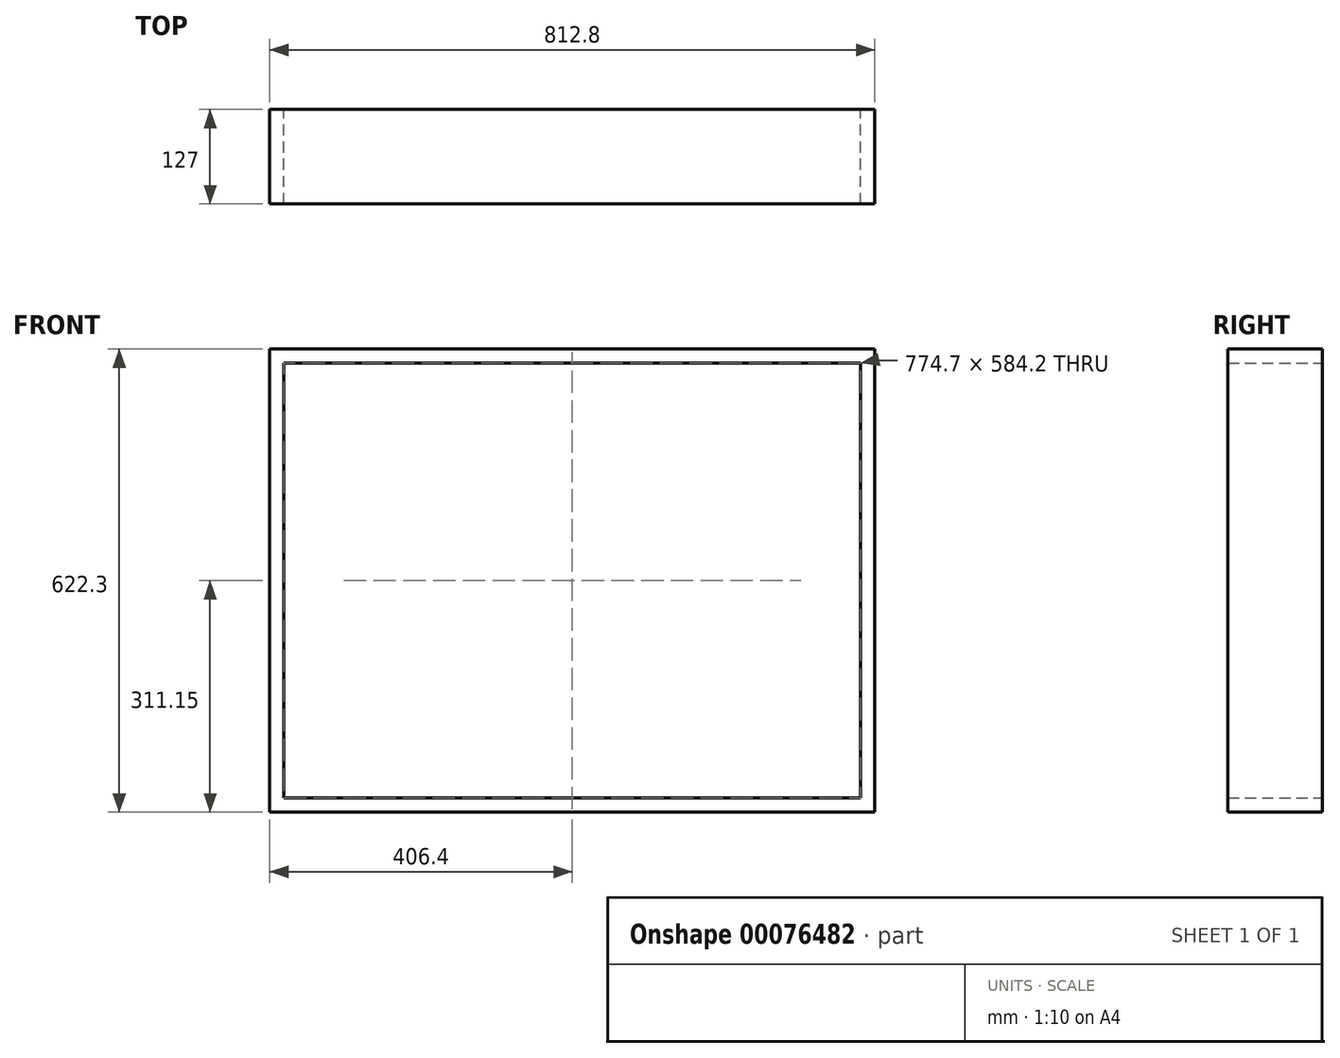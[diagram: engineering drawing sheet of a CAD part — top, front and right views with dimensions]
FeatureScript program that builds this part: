
annotation { "Feature Type Name" : "Feature", "Feature Type Description" : "" }
export const myFeature = defineFeature(function(context is Context, id is Id, definition is map)
    precondition{}
    {
        {
            var Q0;
            Q0=qCreatedBy(makeId("Front.planeOp"),FACE);
            var sketch = newSketch(context, id + "F0", { "sketchPlane" : qUnion([Q0])});
            skLineSegment(sketch, "E0.bottom", {"start": v(0, 0) * mm, "end": v(812.8, 0) * mm});
            skLineSegment(sketch, "E0.top", {"start": v(0, 622.3) * mm, "end": v(812.8, 622.3) * mm});
            skLineSegment(sketch, "E0.left", {"start": v(0, 0) * mm, "end": v(0, 622.3) * mm});
            skLineSegment(sketch, "E0.right", {"start": v(812.8, 0) * mm, "end": v(812.8, 622.3) * mm});
            skLineSegment(sketch, "E1.bottom", {"start": v(19.05, 19.05) * mm, "end": v(793.75, 19.05) * mm});
            skLineSegment(sketch, "E1.top", {"start": v(19.05, 603.25) * mm, "end": v(793.75, 603.25) * mm});
            skLineSegment(sketch, "E1.left", {"start": v(19.05, 19.05) * mm, "end": v(19.05, 603.25) * mm});
            skLineSegment(sketch, "E1.right", {"start": v(793.75, 19.05) * mm, "end": v(793.75, 603.25) * mm});
            skPoint(sketch, "E2", {"position": v(35.15, 34.19) * mm});
            skPoint(sketch, "E3.0.1.0", {"position": v(35.15, 45.97) * mm});
            skPoint(sketch, "E3.0.2.0", {"position": v(35.15, 57.76) * mm});
            skPoint(sketch, "E3.1.0.0", {"position": v(46.94, 34.19) * mm});
            skPoint(sketch, "E3.1.1.0", {"position": v(46.94, 45.97) * mm});
            skPoint(sketch, "E3.1.2.0", {"position": v(46.94, 57.76) * mm});
            skPoint(sketch, "E3.2.0.0", {"position": v(58.72, 34.19) * mm});
            skPoint(sketch, "E3.2.1.0", {"position": v(58.72, 45.97) * mm});
            skPoint(sketch, "E3.2.2.0", {"position": v(58.72, 57.76) * mm});
            skLineSegment(sketch, "E3.direction1", {"start": v(35.15, 34.19) * mm, "end": v(46.94, 34.19) * mm, "construction": true});
            skLineSegment(sketch, "E3.direction2", {"start": v(35.15, 34.19) * mm, "end": v(35.15, 45.97) * mm, "construction": true});
            skPoint(sketch, "E4.0.0.3", {"position": v(35.15, 69.54) * mm});
            skPoint(sketch, "E4.0.0.4", {"position": v(35.15, 81.33) * mm});
            skPoint(sketch, "E4.0.0.5", {"position": v(35.15, 93.11) * mm});
            skPoint(sketch, "E4.0.0.6", {"position": v(35.15, 104.9) * mm});
            skPoint(sketch, "E4.0.0.7", {"position": v(35.15, 116.68) * mm});
            skPoint(sketch, "E4.0.0.8", {"position": v(35.15, 128.47) * mm});
            skPoint(sketch, "E4.0.0.9", {"position": v(35.15, 140.25) * mm});
            skPoint(sketch, "E4.0.0.10", {"position": v(35.15, 152.04) * mm});
            skPoint(sketch, "E4.0.0.11", {"position": v(35.15, 163.82) * mm});
            skPoint(sketch, "E4.0.0.12", {"position": v(35.15, 175.6) * mm});
            skPoint(sketch, "E4.0.0.13", {"position": v(35.15, 187.4) * mm});
            skPoint(sketch, "E4.0.0.14", {"position": v(35.15, 199.18) * mm});
            skPoint(sketch, "E4.0.0.15", {"position": v(35.15, 210.97) * mm});
            skPoint(sketch, "E4.0.0.16", {"position": v(35.15, 222.75) * mm});
            skPoint(sketch, "E4.0.0.17", {"position": v(35.15, 234.54) * mm});
            skPoint(sketch, "E4.0.0.18", {"position": v(35.15, 246.32) * mm});
            skPoint(sketch, "E4.0.0.19", {"position": v(35.15, 258.1) * mm});
            skPoint(sketch, "E4.0.0.20", {"position": v(35.15, 269.9) * mm});
            skPoint(sketch, "E4.0.0.21", {"position": v(35.15, 281.68) * mm});
            skPoint(sketch, "E4.0.0.22", {"position": v(35.15, 293.46) * mm});
            skPoint(sketch, "E4.0.0.23", {"position": v(35.15, 305.25) * mm});
            skPoint(sketch, "E4.0.0.24", {"position": v(35.15, 317.03) * mm});
            skPoint(sketch, "E4.0.0.25", {"position": v(35.15, 328.82) * mm});
            skPoint(sketch, "E4.0.0.26", {"position": v(35.15, 340.6) * mm});
            skPoint(sketch, "E4.0.0.27", {"position": v(35.15, 352.39) * mm});
            skPoint(sketch, "E4.0.0.28", {"position": v(35.15, 364.17) * mm});
            skPoint(sketch, "E4.0.0.29", {"position": v(35.15, 375.96) * mm});
            skPoint(sketch, "E4.0.0.30", {"position": v(35.15, 387.74) * mm});
            skPoint(sketch, "E4.0.0.31", {"position": v(35.15, 399.53) * mm});
            skPoint(sketch, "E4.0.0.32", {"position": v(35.15, 411.31) * mm});
            skPoint(sketch, "E4.0.0.33", {"position": v(35.15, 423.1) * mm});
            skPoint(sketch, "E4.0.0.34", {"position": v(35.15, 434.88) * mm});
            skPoint(sketch, "E4.0.0.35", {"position": v(35.15, 446.67) * mm});
            skPoint(sketch, "E4.0.0.36", {"position": v(35.15, 458.45) * mm});
            skPoint(sketch, "E4.0.0.37", {"position": v(35.15, 470.24) * mm});
            skPoint(sketch, "E4.0.0.38", {"position": v(35.15, 482.02) * mm});
            skPoint(sketch, "E4.0.0.39", {"position": v(35.15, 493.8) * mm});
            skPoint(sketch, "E4.0.0.40", {"position": v(35.15, 505.6) * mm});
            skPoint(sketch, "E4.0.0.41", {"position": v(35.15, 517.38) * mm});
            skPoint(sketch, "E4.0.0.42", {"position": v(35.15, 529.16) * mm});
            skPoint(sketch, "E4.0.0.43", {"position": v(35.15, 540.95) * mm});
            skPoint(sketch, "E4.0.0.44", {"position": v(35.15, 552.73) * mm});
            skPoint(sketch, "E4.0.0.45", {"position": v(35.15, 564.52) * mm});
            skPoint(sketch, "E4.0.0.46", {"position": v(35.15, 576.3) * mm});
            skPoint(sketch, "E4.0.0.47", {"position": v(35.15, 588.09) * mm});
            skPoint(sketch, "E4.0.1.3", {"position": v(46.94, 69.54) * mm});
            skPoint(sketch, "E4.0.1.4", {"position": v(46.94, 81.33) * mm});
            skPoint(sketch, "E4.0.1.5", {"position": v(46.94, 93.11) * mm});
            skPoint(sketch, "E4.0.1.6", {"position": v(46.94, 104.9) * mm});
            skPoint(sketch, "E4.0.1.7", {"position": v(46.94, 116.68) * mm});
            skPoint(sketch, "E4.0.1.8", {"position": v(46.94, 128.47) * mm});
            skPoint(sketch, "E4.0.1.9", {"position": v(46.94, 140.25) * mm});
            skPoint(sketch, "E4.0.1.10", {"position": v(46.94, 152.04) * mm});
            skPoint(sketch, "E4.0.1.11", {"position": v(46.94, 163.82) * mm});
            skPoint(sketch, "E4.0.1.12", {"position": v(46.94, 175.6) * mm});
            skPoint(sketch, "E4.0.1.13", {"position": v(46.94, 187.4) * mm});
            skPoint(sketch, "E4.0.1.14", {"position": v(46.94, 199.18) * mm});
            skPoint(sketch, "E4.0.1.15", {"position": v(46.94, 210.97) * mm});
            skPoint(sketch, "E4.0.1.16", {"position": v(46.94, 222.75) * mm});
            skPoint(sketch, "E4.0.1.17", {"position": v(46.94, 234.54) * mm});
            skPoint(sketch, "E4.0.1.18", {"position": v(46.94, 246.32) * mm});
            skPoint(sketch, "E4.0.1.19", {"position": v(46.94, 258.1) * mm});
            skPoint(sketch, "E4.0.1.20", {"position": v(46.94, 269.9) * mm});
            skPoint(sketch, "E4.0.1.21", {"position": v(46.94, 281.68) * mm});
            skPoint(sketch, "E4.0.1.22", {"position": v(46.94, 293.46) * mm});
            skPoint(sketch, "E4.0.1.23", {"position": v(46.94, 305.25) * mm});
            skPoint(sketch, "E4.0.1.24", {"position": v(46.94, 317.03) * mm});
            skPoint(sketch, "E4.0.1.25", {"position": v(46.94, 328.82) * mm});
            skPoint(sketch, "E4.0.1.26", {"position": v(46.94, 340.6) * mm});
            skPoint(sketch, "E4.0.1.27", {"position": v(46.94, 352.39) * mm});
            skPoint(sketch, "E4.0.1.28", {"position": v(46.94, 364.17) * mm});
            skPoint(sketch, "E4.0.1.29", {"position": v(46.94, 375.96) * mm});
            skPoint(sketch, "E4.0.1.30", {"position": v(46.94, 387.74) * mm});
            skPoint(sketch, "E4.0.1.31", {"position": v(46.94, 399.53) * mm});
            skPoint(sketch, "E4.0.1.32", {"position": v(46.94, 411.31) * mm});
            skPoint(sketch, "E4.0.1.33", {"position": v(46.94, 423.1) * mm});
            skPoint(sketch, "E4.0.1.34", {"position": v(46.94, 434.88) * mm});
            skPoint(sketch, "E4.0.1.35", {"position": v(46.94, 446.67) * mm});
            skPoint(sketch, "E4.0.1.36", {"position": v(46.94, 458.45) * mm});
            skPoint(sketch, "E4.0.1.37", {"position": v(46.94, 470.24) * mm});
            skPoint(sketch, "E4.0.1.38", {"position": v(46.94, 482.02) * mm});
            skPoint(sketch, "E4.0.1.39", {"position": v(46.94, 493.8) * mm});
            skPoint(sketch, "E4.0.1.40", {"position": v(46.94, 505.6) * mm});
            skPoint(sketch, "E4.0.1.41", {"position": v(46.94, 517.38) * mm});
            skPoint(sketch, "E4.0.1.42", {"position": v(46.94, 529.16) * mm});
            skPoint(sketch, "E4.0.1.43", {"position": v(46.94, 540.95) * mm});
            skPoint(sketch, "E4.0.1.44", {"position": v(46.94, 552.73) * mm});
            skPoint(sketch, "E4.0.1.45", {"position": v(46.94, 564.52) * mm});
            skPoint(sketch, "E4.0.1.46", {"position": v(46.94, 576.3) * mm});
            skPoint(sketch, "E4.0.1.47", {"position": v(46.94, 588.09) * mm});
            skPoint(sketch, "E4.0.2.3", {"position": v(58.72, 69.54) * mm});
            skPoint(sketch, "E4.0.2.4", {"position": v(58.72, 81.33) * mm});
            skPoint(sketch, "E4.0.2.5", {"position": v(58.72, 93.11) * mm});
            skPoint(sketch, "E4.0.2.6", {"position": v(58.72, 104.9) * mm});
            skPoint(sketch, "E4.0.2.7", {"position": v(58.72, 116.68) * mm});
            skPoint(sketch, "E4.0.2.8", {"position": v(58.72, 128.47) * mm});
            skPoint(sketch, "E4.0.2.9", {"position": v(58.72, 140.25) * mm});
            skPoint(sketch, "E4.0.2.10", {"position": v(58.72, 152.04) * mm});
            skPoint(sketch, "E4.0.2.11", {"position": v(58.72, 163.82) * mm});
            skPoint(sketch, "E4.0.2.12", {"position": v(58.72, 175.6) * mm});
            skPoint(sketch, "E4.0.2.13", {"position": v(58.72, 187.4) * mm});
            skPoint(sketch, "E4.0.2.14", {"position": v(58.72, 199.18) * mm});
            skPoint(sketch, "E4.0.2.15", {"position": v(58.72, 210.97) * mm});
            skPoint(sketch, "E4.0.2.16", {"position": v(58.72, 222.75) * mm});
            skPoint(sketch, "E4.0.2.17", {"position": v(58.72, 234.54) * mm});
            skPoint(sketch, "E4.0.2.18", {"position": v(58.72, 246.32) * mm});
            skPoint(sketch, "E4.0.2.19", {"position": v(58.72, 258.1) * mm});
            skPoint(sketch, "E4.0.2.20", {"position": v(58.72, 269.9) * mm});
            skPoint(sketch, "E4.0.2.21", {"position": v(58.72, 281.68) * mm});
            skPoint(sketch, "E4.0.2.22", {"position": v(58.72, 293.46) * mm});
            skPoint(sketch, "E4.0.2.23", {"position": v(58.72, 305.25) * mm});
            skPoint(sketch, "E4.0.2.24", {"position": v(58.72, 317.03) * mm});
            skPoint(sketch, "E4.0.2.25", {"position": v(58.72, 328.82) * mm});
            skPoint(sketch, "E4.0.2.26", {"position": v(58.72, 340.6) * mm});
            skPoint(sketch, "E4.0.2.27", {"position": v(58.72, 352.39) * mm});
            skPoint(sketch, "E4.0.2.28", {"position": v(58.72, 364.17) * mm});
            skPoint(sketch, "E4.0.2.29", {"position": v(58.72, 375.96) * mm});
            skPoint(sketch, "E4.0.2.30", {"position": v(58.72, 387.74) * mm});
            skPoint(sketch, "E4.0.2.31", {"position": v(58.72, 399.53) * mm});
            skPoint(sketch, "E4.0.2.32", {"position": v(58.72, 411.31) * mm});
            skPoint(sketch, "E4.0.2.33", {"position": v(58.72, 423.1) * mm});
            skPoint(sketch, "E4.0.2.34", {"position": v(58.72, 434.88) * mm});
            skPoint(sketch, "E4.0.2.35", {"position": v(58.72, 446.67) * mm});
            skPoint(sketch, "E4.0.2.36", {"position": v(58.72, 458.45) * mm});
            skPoint(sketch, "E4.0.2.37", {"position": v(58.72, 470.24) * mm});
            skPoint(sketch, "E4.0.2.38", {"position": v(58.72, 482.02) * mm});
            skPoint(sketch, "E4.0.2.39", {"position": v(58.72, 493.8) * mm});
            skPoint(sketch, "E4.0.2.40", {"position": v(58.72, 505.6) * mm});
            skPoint(sketch, "E4.0.2.41", {"position": v(58.72, 517.38) * mm});
            skPoint(sketch, "E4.0.2.42", {"position": v(58.72, 529.16) * mm});
            skPoint(sketch, "E4.0.2.43", {"position": v(58.72, 540.95) * mm});
            skPoint(sketch, "E4.0.2.44", {"position": v(58.72, 552.73) * mm});
            skPoint(sketch, "E4.0.2.45", {"position": v(58.72, 564.52) * mm});
            skPoint(sketch, "E4.0.2.46", {"position": v(58.72, 576.3) * mm});
            skPoint(sketch, "E4.0.2.47", {"position": v(58.72, 588.09) * mm});
            skPoint(sketch, "E5.0.3.0", {"position": v(70.5, 34.19) * mm});
            skPoint(sketch, "E5.0.3.1", {"position": v(70.5, 45.97) * mm});
            skPoint(sketch, "E5.0.3.2", {"position": v(70.5, 57.76) * mm});
            skPoint(sketch, "E5.0.3.3", {"position": v(70.5, 69.54) * mm});
            skPoint(sketch, "E5.0.3.4", {"position": v(70.5, 81.33) * mm});
            skPoint(sketch, "E5.0.3.5", {"position": v(70.5, 93.11) * mm});
            skPoint(sketch, "E5.0.3.6", {"position": v(70.5, 104.9) * mm});
            skPoint(sketch, "E5.0.3.7", {"position": v(70.5, 116.68) * mm});
            skPoint(sketch, "E5.0.3.8", {"position": v(70.5, 128.47) * mm});
            skPoint(sketch, "E5.0.3.9", {"position": v(70.5, 140.25) * mm});
            skPoint(sketch, "E5.0.3.10", {"position": v(70.5, 152.04) * mm});
            skPoint(sketch, "E5.0.3.11", {"position": v(70.5, 163.82) * mm});
            skPoint(sketch, "E5.0.3.12", {"position": v(70.5, 175.6) * mm});
            skPoint(sketch, "E5.0.3.13", {"position": v(70.5, 187.4) * mm});
            skPoint(sketch, "E5.0.3.14", {"position": v(70.5, 199.18) * mm});
            skPoint(sketch, "E5.0.3.15", {"position": v(70.5, 210.97) * mm});
            skPoint(sketch, "E5.0.3.16", {"position": v(70.5, 222.75) * mm});
            skPoint(sketch, "E5.0.3.17", {"position": v(70.5, 234.54) * mm});
            skPoint(sketch, "E5.0.3.18", {"position": v(70.5, 246.32) * mm});
            skPoint(sketch, "E5.0.3.19", {"position": v(70.5, 258.1) * mm});
            skPoint(sketch, "E5.0.3.20", {"position": v(70.5, 269.9) * mm});
            skPoint(sketch, "E5.0.3.21", {"position": v(70.5, 281.68) * mm});
            skPoint(sketch, "E5.0.3.22", {"position": v(70.5, 293.46) * mm});
            skPoint(sketch, "E5.0.3.23", {"position": v(70.5, 305.25) * mm});
            skPoint(sketch, "E5.0.3.24", {"position": v(70.5, 317.03) * mm});
            skPoint(sketch, "E5.0.3.25", {"position": v(70.5, 328.82) * mm});
            skPoint(sketch, "E5.0.3.26", {"position": v(70.5, 340.6) * mm});
            skPoint(sketch, "E5.0.3.27", {"position": v(70.5, 352.39) * mm});
            skPoint(sketch, "E5.0.3.28", {"position": v(70.5, 364.17) * mm});
            skPoint(sketch, "E5.0.3.29", {"position": v(70.5, 375.96) * mm});
            skPoint(sketch, "E5.0.3.30", {"position": v(70.5, 387.74) * mm});
            skPoint(sketch, "E5.0.3.31", {"position": v(70.5, 399.53) * mm});
            skPoint(sketch, "E5.0.3.32", {"position": v(70.5, 411.31) * mm});
            skPoint(sketch, "E5.0.3.33", {"position": v(70.5, 423.1) * mm});
            skPoint(sketch, "E5.0.3.34", {"position": v(70.5, 434.88) * mm});
            skPoint(sketch, "E5.0.3.35", {"position": v(70.5, 446.67) * mm});
            skPoint(sketch, "E5.0.3.36", {"position": v(70.5, 458.45) * mm});
            skPoint(sketch, "E5.0.3.37", {"position": v(70.5, 470.24) * mm});
            skPoint(sketch, "E5.0.3.38", {"position": v(70.5, 482.02) * mm});
            skPoint(sketch, "E5.0.3.39", {"position": v(70.5, 493.8) * mm});
            skPoint(sketch, "E5.0.3.40", {"position": v(70.5, 505.6) * mm});
            skPoint(sketch, "E5.0.3.41", {"position": v(70.5, 517.38) * mm});
            skPoint(sketch, "E5.0.3.42", {"position": v(70.5, 529.16) * mm});
            skPoint(sketch, "E5.0.3.43", {"position": v(70.5, 540.95) * mm});
            skPoint(sketch, "E5.0.3.44", {"position": v(70.5, 552.73) * mm});
            skPoint(sketch, "E5.0.3.45", {"position": v(70.5, 564.52) * mm});
            skPoint(sketch, "E5.0.3.46", {"position": v(70.5, 576.3) * mm});
            skPoint(sketch, "E5.0.3.47", {"position": v(70.5, 588.09) * mm});
            skPoint(sketch, "E5.0.4.0", {"position": v(82.3, 34.19) * mm});
            skPoint(sketch, "E5.0.4.1", {"position": v(82.3, 45.97) * mm});
            skPoint(sketch, "E5.0.4.2", {"position": v(82.3, 57.76) * mm});
            skPoint(sketch, "E5.0.4.3", {"position": v(82.3, 69.54) * mm});
            skPoint(sketch, "E5.0.4.4", {"position": v(82.3, 81.33) * mm});
            skPoint(sketch, "E5.0.4.5", {"position": v(82.3, 93.11) * mm});
            skPoint(sketch, "E5.0.4.6", {"position": v(82.3, 104.9) * mm});
            skPoint(sketch, "E5.0.4.7", {"position": v(82.3, 116.68) * mm});
            skPoint(sketch, "E5.0.4.8", {"position": v(82.3, 128.47) * mm});
            skPoint(sketch, "E5.0.4.9", {"position": v(82.3, 140.25) * mm});
            skPoint(sketch, "E5.0.4.10", {"position": v(82.3, 152.04) * mm});
            skPoint(sketch, "E5.0.4.11", {"position": v(82.3, 163.82) * mm});
            skPoint(sketch, "E5.0.4.12", {"position": v(82.3, 175.6) * mm});
            skPoint(sketch, "E5.0.4.13", {"position": v(82.3, 187.4) * mm});
            skPoint(sketch, "E5.0.4.14", {"position": v(82.3, 199.18) * mm});
            skPoint(sketch, "E5.0.4.15", {"position": v(82.3, 210.97) * mm});
            skPoint(sketch, "E5.0.4.16", {"position": v(82.3, 222.75) * mm});
            skPoint(sketch, "E5.0.4.17", {"position": v(82.3, 234.54) * mm});
            skPoint(sketch, "E5.0.4.18", {"position": v(82.3, 246.32) * mm});
            skPoint(sketch, "E5.0.4.19", {"position": v(82.3, 258.1) * mm});
            skPoint(sketch, "E5.0.4.20", {"position": v(82.3, 269.9) * mm});
            skPoint(sketch, "E5.0.4.21", {"position": v(82.3, 281.68) * mm});
            skPoint(sketch, "E5.0.4.22", {"position": v(82.3, 293.46) * mm});
            skPoint(sketch, "E5.0.4.23", {"position": v(82.3, 305.25) * mm});
            skPoint(sketch, "E5.0.4.24", {"position": v(82.3, 317.03) * mm});
            skPoint(sketch, "E5.0.4.25", {"position": v(82.3, 328.82) * mm});
            skPoint(sketch, "E5.0.4.26", {"position": v(82.3, 340.6) * mm});
            skPoint(sketch, "E5.0.4.27", {"position": v(82.3, 352.39) * mm});
            skPoint(sketch, "E5.0.4.28", {"position": v(82.3, 364.17) * mm});
            skPoint(sketch, "E5.0.4.29", {"position": v(82.3, 375.96) * mm});
            skPoint(sketch, "E5.0.4.30", {"position": v(82.3, 387.74) * mm});
            skPoint(sketch, "E5.0.4.31", {"position": v(82.3, 399.53) * mm});
            skPoint(sketch, "E5.0.4.32", {"position": v(82.3, 411.31) * mm});
            skPoint(sketch, "E5.0.4.33", {"position": v(82.3, 423.1) * mm});
            skPoint(sketch, "E5.0.4.34", {"position": v(82.3, 434.88) * mm});
            skPoint(sketch, "E5.0.4.35", {"position": v(82.3, 446.67) * mm});
            skPoint(sketch, "E5.0.4.36", {"position": v(82.3, 458.45) * mm});
            skPoint(sketch, "E5.0.4.37", {"position": v(82.3, 470.24) * mm});
            skPoint(sketch, "E5.0.4.38", {"position": v(82.3, 482.02) * mm});
            skPoint(sketch, "E5.0.4.39", {"position": v(82.3, 493.8) * mm});
            skPoint(sketch, "E5.0.4.40", {"position": v(82.3, 505.6) * mm});
            skPoint(sketch, "E5.0.4.41", {"position": v(82.3, 517.38) * mm});
            skPoint(sketch, "E5.0.4.42", {"position": v(82.3, 529.16) * mm});
            skPoint(sketch, "E5.0.4.43", {"position": v(82.3, 540.95) * mm});
            skPoint(sketch, "E5.0.4.44", {"position": v(82.3, 552.73) * mm});
            skPoint(sketch, "E5.0.4.45", {"position": v(82.3, 564.52) * mm});
            skPoint(sketch, "E5.0.4.46", {"position": v(82.3, 576.3) * mm});
            skPoint(sketch, "E5.0.4.47", {"position": v(82.3, 588.09) * mm});
            skPoint(sketch, "E5.0.5.0", {"position": v(94.08, 34.19) * mm});
            skPoint(sketch, "E5.0.5.1", {"position": v(94.08, 45.97) * mm});
            skPoint(sketch, "E5.0.5.2", {"position": v(94.08, 57.76) * mm});
            skPoint(sketch, "E5.0.5.3", {"position": v(94.08, 69.54) * mm});
            skPoint(sketch, "E5.0.5.4", {"position": v(94.08, 81.33) * mm});
            skPoint(sketch, "E5.0.5.5", {"position": v(94.08, 93.11) * mm});
            skPoint(sketch, "E5.0.5.6", {"position": v(94.08, 104.9) * mm});
            skPoint(sketch, "E5.0.5.7", {"position": v(94.08, 116.68) * mm});
            skPoint(sketch, "E5.0.5.8", {"position": v(94.08, 128.47) * mm});
            skPoint(sketch, "E5.0.5.9", {"position": v(94.08, 140.25) * mm});
            skPoint(sketch, "E5.0.5.10", {"position": v(94.08, 152.04) * mm});
            skPoint(sketch, "E5.0.5.11", {"position": v(94.08, 163.82) * mm});
            skPoint(sketch, "E5.0.5.12", {"position": v(94.08, 175.6) * mm});
            skPoint(sketch, "E5.0.5.13", {"position": v(94.08, 187.4) * mm});
            skPoint(sketch, "E5.0.5.14", {"position": v(94.08, 199.18) * mm});
            skPoint(sketch, "E5.0.5.15", {"position": v(94.08, 210.97) * mm});
            skPoint(sketch, "E5.0.5.16", {"position": v(94.08, 222.75) * mm});
            skPoint(sketch, "E5.0.5.17", {"position": v(94.08, 234.54) * mm});
            skPoint(sketch, "E5.0.5.18", {"position": v(94.08, 246.32) * mm});
            skPoint(sketch, "E5.0.5.19", {"position": v(94.08, 258.1) * mm});
            skPoint(sketch, "E5.0.5.20", {"position": v(94.08, 269.9) * mm});
            skPoint(sketch, "E5.0.5.21", {"position": v(94.08, 281.68) * mm});
            skPoint(sketch, "E5.0.5.22", {"position": v(94.08, 293.46) * mm});
            skPoint(sketch, "E5.0.5.23", {"position": v(94.08, 305.25) * mm});
            skPoint(sketch, "E5.0.5.24", {"position": v(94.08, 317.03) * mm});
            skPoint(sketch, "E5.0.5.25", {"position": v(94.08, 328.82) * mm});
            skPoint(sketch, "E5.0.5.26", {"position": v(94.08, 340.6) * mm});
            skPoint(sketch, "E5.0.5.27", {"position": v(94.08, 352.39) * mm});
            skPoint(sketch, "E5.0.5.28", {"position": v(94.08, 364.17) * mm});
            skPoint(sketch, "E5.0.5.29", {"position": v(94.08, 375.96) * mm});
            skPoint(sketch, "E5.0.5.30", {"position": v(94.08, 387.74) * mm});
            skPoint(sketch, "E5.0.5.31", {"position": v(94.08, 399.53) * mm});
            skPoint(sketch, "E5.0.5.32", {"position": v(94.08, 411.31) * mm});
            skPoint(sketch, "E5.0.5.33", {"position": v(94.08, 423.1) * mm});
            skPoint(sketch, "E5.0.5.34", {"position": v(94.08, 434.88) * mm});
            skPoint(sketch, "E5.0.5.35", {"position": v(94.08, 446.67) * mm});
            skPoint(sketch, "E5.0.5.36", {"position": v(94.08, 458.45) * mm});
            skPoint(sketch, "E5.0.5.37", {"position": v(94.08, 470.24) * mm});
            skPoint(sketch, "E5.0.5.38", {"position": v(94.08, 482.02) * mm});
            skPoint(sketch, "E5.0.5.39", {"position": v(94.08, 493.8) * mm});
            skPoint(sketch, "E5.0.5.40", {"position": v(94.08, 505.6) * mm});
            skPoint(sketch, "E5.0.5.41", {"position": v(94.08, 517.38) * mm});
            skPoint(sketch, "E5.0.5.42", {"position": v(94.08, 529.16) * mm});
            skPoint(sketch, "E5.0.5.43", {"position": v(94.08, 540.95) * mm});
            skPoint(sketch, "E5.0.5.44", {"position": v(94.08, 552.73) * mm});
            skPoint(sketch, "E5.0.5.45", {"position": v(94.08, 564.52) * mm});
            skPoint(sketch, "E5.0.5.46", {"position": v(94.08, 576.3) * mm});
            skPoint(sketch, "E5.0.5.47", {"position": v(94.08, 588.09) * mm});
            skPoint(sketch, "E5.0.6.0", {"position": v(105.86, 34.19) * mm});
            skPoint(sketch, "E5.0.6.1", {"position": v(105.86, 45.97) * mm});
            skPoint(sketch, "E5.0.6.2", {"position": v(105.86, 57.76) * mm});
            skPoint(sketch, "E5.0.6.3", {"position": v(105.86, 69.54) * mm});
            skPoint(sketch, "E5.0.6.4", {"position": v(105.86, 81.33) * mm});
            skPoint(sketch, "E5.0.6.5", {"position": v(105.86, 93.11) * mm});
            skPoint(sketch, "E5.0.6.6", {"position": v(105.86, 104.9) * mm});
            skPoint(sketch, "E5.0.6.7", {"position": v(105.86, 116.68) * mm});
            skPoint(sketch, "E5.0.6.8", {"position": v(105.86, 128.47) * mm});
            skPoint(sketch, "E5.0.6.9", {"position": v(105.86, 140.25) * mm});
            skPoint(sketch, "E5.0.6.10", {"position": v(105.86, 152.04) * mm});
            skPoint(sketch, "E5.0.6.11", {"position": v(105.86, 163.82) * mm});
            skPoint(sketch, "E5.0.6.12", {"position": v(105.86, 175.6) * mm});
            skPoint(sketch, "E5.0.6.13", {"position": v(105.86, 187.4) * mm});
            skPoint(sketch, "E5.0.6.14", {"position": v(105.86, 199.18) * mm});
            skPoint(sketch, "E5.0.6.15", {"position": v(105.86, 210.97) * mm});
            skPoint(sketch, "E5.0.6.16", {"position": v(105.86, 222.75) * mm});
            skPoint(sketch, "E5.0.6.17", {"position": v(105.86, 234.54) * mm});
            skPoint(sketch, "E5.0.6.18", {"position": v(105.86, 246.32) * mm});
            skPoint(sketch, "E5.0.6.19", {"position": v(105.86, 258.1) * mm});
            skPoint(sketch, "E5.0.6.20", {"position": v(105.86, 269.9) * mm});
            skPoint(sketch, "E5.0.6.21", {"position": v(105.86, 281.68) * mm});
            skPoint(sketch, "E5.0.6.22", {"position": v(105.86, 293.46) * mm});
            skPoint(sketch, "E5.0.6.23", {"position": v(105.86, 305.25) * mm});
            skPoint(sketch, "E5.0.6.24", {"position": v(105.86, 317.03) * mm});
            skPoint(sketch, "E5.0.6.25", {"position": v(105.86, 328.82) * mm});
            skPoint(sketch, "E5.0.6.26", {"position": v(105.86, 340.6) * mm});
            skPoint(sketch, "E5.0.6.27", {"position": v(105.86, 352.39) * mm});
            skPoint(sketch, "E5.0.6.28", {"position": v(105.86, 364.17) * mm});
            skPoint(sketch, "E5.0.6.29", {"position": v(105.86, 375.96) * mm});
            skPoint(sketch, "E5.0.6.30", {"position": v(105.86, 387.74) * mm});
            skPoint(sketch, "E5.0.6.31", {"position": v(105.86, 399.53) * mm});
            skPoint(sketch, "E5.0.6.32", {"position": v(105.86, 411.31) * mm});
            skPoint(sketch, "E5.0.6.33", {"position": v(105.86, 423.1) * mm});
            skPoint(sketch, "E5.0.6.34", {"position": v(105.86, 434.88) * mm});
            skPoint(sketch, "E5.0.6.35", {"position": v(105.86, 446.67) * mm});
            skPoint(sketch, "E5.0.6.36", {"position": v(105.86, 458.45) * mm});
            skPoint(sketch, "E5.0.6.37", {"position": v(105.86, 470.24) * mm});
            skPoint(sketch, "E5.0.6.38", {"position": v(105.86, 482.02) * mm});
            skPoint(sketch, "E5.0.6.39", {"position": v(105.86, 493.8) * mm});
            skPoint(sketch, "E5.0.6.40", {"position": v(105.86, 505.6) * mm});
            skPoint(sketch, "E5.0.6.41", {"position": v(105.86, 517.38) * mm});
            skPoint(sketch, "E5.0.6.42", {"position": v(105.86, 529.16) * mm});
            skPoint(sketch, "E5.0.6.43", {"position": v(105.86, 540.95) * mm});
            skPoint(sketch, "E5.0.6.44", {"position": v(105.86, 552.73) * mm});
            skPoint(sketch, "E5.0.6.45", {"position": v(105.86, 564.52) * mm});
            skPoint(sketch, "E5.0.6.46", {"position": v(105.86, 576.3) * mm});
            skPoint(sketch, "E5.0.6.47", {"position": v(105.86, 588.09) * mm});
            skPoint(sketch, "E5.0.7.0", {"position": v(117.65, 34.19) * mm});
            skPoint(sketch, "E5.0.7.1", {"position": v(117.65, 45.97) * mm});
            skPoint(sketch, "E5.0.7.2", {"position": v(117.65, 57.76) * mm});
            skPoint(sketch, "E5.0.7.3", {"position": v(117.65, 69.54) * mm});
            skPoint(sketch, "E5.0.7.4", {"position": v(117.65, 81.33) * mm});
            skPoint(sketch, "E5.0.7.5", {"position": v(117.65, 93.11) * mm});
            skPoint(sketch, "E5.0.7.6", {"position": v(117.65, 104.9) * mm});
            skPoint(sketch, "E5.0.7.7", {"position": v(117.65, 116.68) * mm});
            skPoint(sketch, "E5.0.7.8", {"position": v(117.65, 128.47) * mm});
            skPoint(sketch, "E5.0.7.9", {"position": v(117.65, 140.25) * mm});
            skPoint(sketch, "E5.0.7.10", {"position": v(117.65, 152.04) * mm});
            skPoint(sketch, "E5.0.7.11", {"position": v(117.65, 163.82) * mm});
            skPoint(sketch, "E5.0.7.12", {"position": v(117.65, 175.6) * mm});
            skPoint(sketch, "E5.0.7.13", {"position": v(117.65, 187.4) * mm});
            skPoint(sketch, "E5.0.7.14", {"position": v(117.65, 199.18) * mm});
            skPoint(sketch, "E5.0.7.15", {"position": v(117.65, 210.97) * mm});
            skPoint(sketch, "E5.0.7.16", {"position": v(117.65, 222.75) * mm});
            skPoint(sketch, "E5.0.7.17", {"position": v(117.65, 234.54) * mm});
            skPoint(sketch, "E5.0.7.18", {"position": v(117.65, 246.32) * mm});
            skPoint(sketch, "E5.0.7.19", {"position": v(117.65, 258.1) * mm});
            skPoint(sketch, "E5.0.7.20", {"position": v(117.65, 269.9) * mm});
            skPoint(sketch, "E5.0.7.21", {"position": v(117.65, 281.68) * mm});
            skPoint(sketch, "E5.0.7.22", {"position": v(117.65, 293.46) * mm});
            skPoint(sketch, "E5.0.7.23", {"position": v(117.65, 305.25) * mm});
            skPoint(sketch, "E5.0.7.24", {"position": v(117.65, 317.03) * mm});
            skPoint(sketch, "E5.0.7.25", {"position": v(117.65, 328.82) * mm});
            skPoint(sketch, "E5.0.7.26", {"position": v(117.65, 340.6) * mm});
            skPoint(sketch, "E5.0.7.27", {"position": v(117.65, 352.39) * mm});
            skPoint(sketch, "E5.0.7.28", {"position": v(117.65, 364.17) * mm});
            skPoint(sketch, "E5.0.7.29", {"position": v(117.65, 375.96) * mm});
            skPoint(sketch, "E5.0.7.30", {"position": v(117.65, 387.74) * mm});
            skPoint(sketch, "E5.0.7.31", {"position": v(117.65, 399.53) * mm});
            skPoint(sketch, "E5.0.7.32", {"position": v(117.65, 411.31) * mm});
            skPoint(sketch, "E5.0.7.33", {"position": v(117.65, 423.1) * mm});
            skPoint(sketch, "E5.0.7.34", {"position": v(117.65, 434.88) * mm});
            skPoint(sketch, "E5.0.7.35", {"position": v(117.65, 446.67) * mm});
            skPoint(sketch, "E5.0.7.36", {"position": v(117.65, 458.45) * mm});
            skPoint(sketch, "E5.0.7.37", {"position": v(117.65, 470.24) * mm});
            skPoint(sketch, "E5.0.7.38", {"position": v(117.65, 482.02) * mm});
            skPoint(sketch, "E5.0.7.39", {"position": v(117.65, 493.8) * mm});
            skPoint(sketch, "E5.0.7.40", {"position": v(117.65, 505.6) * mm});
            skPoint(sketch, "E5.0.7.41", {"position": v(117.65, 517.38) * mm});
            skPoint(sketch, "E5.0.7.42", {"position": v(117.65, 529.16) * mm});
            skPoint(sketch, "E5.0.7.43", {"position": v(117.65, 540.95) * mm});
            skPoint(sketch, "E5.0.7.44", {"position": v(117.65, 552.73) * mm});
            skPoint(sketch, "E5.0.7.45", {"position": v(117.65, 564.52) * mm});
            skPoint(sketch, "E5.0.7.46", {"position": v(117.65, 576.3) * mm});
            skPoint(sketch, "E5.0.7.47", {"position": v(117.65, 588.09) * mm});
            skPoint(sketch, "E5.0.8.0", {"position": v(129.43, 34.19) * mm});
            skPoint(sketch, "E5.0.8.1", {"position": v(129.43, 45.97) * mm});
            skPoint(sketch, "E5.0.8.2", {"position": v(129.43, 57.76) * mm});
            skPoint(sketch, "E5.0.8.3", {"position": v(129.43, 69.54) * mm});
            skPoint(sketch, "E5.0.8.4", {"position": v(129.43, 81.33) * mm});
            skPoint(sketch, "E5.0.8.5", {"position": v(129.43, 93.11) * mm});
            skPoint(sketch, "E5.0.8.6", {"position": v(129.43, 104.9) * mm});
            skPoint(sketch, "E5.0.8.7", {"position": v(129.43, 116.68) * mm});
            skPoint(sketch, "E5.0.8.8", {"position": v(129.43, 128.47) * mm});
            skPoint(sketch, "E5.0.8.9", {"position": v(129.43, 140.25) * mm});
            skPoint(sketch, "E5.0.8.10", {"position": v(129.43, 152.04) * mm});
            skPoint(sketch, "E5.0.8.11", {"position": v(129.43, 163.82) * mm});
            skPoint(sketch, "E5.0.8.12", {"position": v(129.43, 175.6) * mm});
            skPoint(sketch, "E5.0.8.13", {"position": v(129.43, 187.4) * mm});
            skPoint(sketch, "E5.0.8.14", {"position": v(129.43, 199.18) * mm});
            skPoint(sketch, "E5.0.8.15", {"position": v(129.43, 210.97) * mm});
            skPoint(sketch, "E5.0.8.16", {"position": v(129.43, 222.75) * mm});
            skPoint(sketch, "E5.0.8.17", {"position": v(129.43, 234.54) * mm});
            skPoint(sketch, "E5.0.8.18", {"position": v(129.43, 246.32) * mm});
            skPoint(sketch, "E5.0.8.19", {"position": v(129.43, 258.1) * mm});
            skPoint(sketch, "E5.0.8.20", {"position": v(129.43, 269.9) * mm});
            skPoint(sketch, "E5.0.8.21", {"position": v(129.43, 281.68) * mm});
            skPoint(sketch, "E5.0.8.22", {"position": v(129.43, 293.46) * mm});
            skPoint(sketch, "E5.0.8.23", {"position": v(129.43, 305.25) * mm});
            skPoint(sketch, "E5.0.8.24", {"position": v(129.43, 317.03) * mm});
            skPoint(sketch, "E5.0.8.25", {"position": v(129.43, 328.82) * mm});
            skPoint(sketch, "E5.0.8.26", {"position": v(129.43, 340.6) * mm});
            skPoint(sketch, "E5.0.8.27", {"position": v(129.43, 352.39) * mm});
            skPoint(sketch, "E5.0.8.28", {"position": v(129.43, 364.17) * mm});
            skPoint(sketch, "E5.0.8.29", {"position": v(129.43, 375.96) * mm});
            skPoint(sketch, "E5.0.8.30", {"position": v(129.43, 387.74) * mm});
            skPoint(sketch, "E5.0.8.31", {"position": v(129.43, 399.53) * mm});
            skPoint(sketch, "E5.0.8.32", {"position": v(129.43, 411.31) * mm});
            skPoint(sketch, "E5.0.8.33", {"position": v(129.43, 423.1) * mm});
            skPoint(sketch, "E5.0.8.34", {"position": v(129.43, 434.88) * mm});
            skPoint(sketch, "E5.0.8.35", {"position": v(129.43, 446.67) * mm});
            skPoint(sketch, "E5.0.8.36", {"position": v(129.43, 458.45) * mm});
            skPoint(sketch, "E5.0.8.37", {"position": v(129.43, 470.24) * mm});
            skPoint(sketch, "E5.0.8.38", {"position": v(129.43, 482.02) * mm});
            skPoint(sketch, "E5.0.8.39", {"position": v(129.43, 493.8) * mm});
            skPoint(sketch, "E5.0.8.40", {"position": v(129.43, 505.6) * mm});
            skPoint(sketch, "E5.0.8.41", {"position": v(129.43, 517.38) * mm});
            skPoint(sketch, "E5.0.8.42", {"position": v(129.43, 529.16) * mm});
            skPoint(sketch, "E5.0.8.43", {"position": v(129.43, 540.95) * mm});
            skPoint(sketch, "E5.0.8.44", {"position": v(129.43, 552.73) * mm});
            skPoint(sketch, "E5.0.8.45", {"position": v(129.43, 564.52) * mm});
            skPoint(sketch, "E5.0.8.46", {"position": v(129.43, 576.3) * mm});
            skPoint(sketch, "E5.0.8.47", {"position": v(129.43, 588.09) * mm});
            skPoint(sketch, "E5.0.9.0", {"position": v(141.22, 34.19) * mm});
            skPoint(sketch, "E5.0.9.1", {"position": v(141.22, 45.97) * mm});
            skPoint(sketch, "E5.0.9.2", {"position": v(141.22, 57.76) * mm});
            skPoint(sketch, "E5.0.9.3", {"position": v(141.22, 69.54) * mm});
            skPoint(sketch, "E5.0.9.4", {"position": v(141.22, 81.33) * mm});
            skPoint(sketch, "E5.0.9.5", {"position": v(141.22, 93.11) * mm});
            skPoint(sketch, "E5.0.9.6", {"position": v(141.22, 104.9) * mm});
            skPoint(sketch, "E5.0.9.7", {"position": v(141.22, 116.68) * mm});
            skPoint(sketch, "E5.0.9.8", {"position": v(141.22, 128.47) * mm});
            skPoint(sketch, "E5.0.9.9", {"position": v(141.22, 140.25) * mm});
            skPoint(sketch, "E5.0.9.10", {"position": v(141.22, 152.04) * mm});
            skPoint(sketch, "E5.0.9.11", {"position": v(141.22, 163.82) * mm});
            skPoint(sketch, "E5.0.9.12", {"position": v(141.22, 175.6) * mm});
            skPoint(sketch, "E5.0.9.13", {"position": v(141.22, 187.4) * mm});
            skPoint(sketch, "E5.0.9.14", {"position": v(141.22, 199.18) * mm});
            skPoint(sketch, "E5.0.9.15", {"position": v(141.22, 210.97) * mm});
            skPoint(sketch, "E5.0.9.16", {"position": v(141.22, 222.75) * mm});
            skPoint(sketch, "E5.0.9.17", {"position": v(141.22, 234.54) * mm});
            skPoint(sketch, "E5.0.9.18", {"position": v(141.22, 246.32) * mm});
            skPoint(sketch, "E5.0.9.19", {"position": v(141.22, 258.1) * mm});
            skPoint(sketch, "E5.0.9.20", {"position": v(141.22, 269.9) * mm});
            skPoint(sketch, "E5.0.9.21", {"position": v(141.22, 281.68) * mm});
            skPoint(sketch, "E5.0.9.22", {"position": v(141.22, 293.46) * mm});
            skPoint(sketch, "E5.0.9.23", {"position": v(141.22, 305.25) * mm});
            skPoint(sketch, "E5.0.9.24", {"position": v(141.22, 317.03) * mm});
            skPoint(sketch, "E5.0.9.25", {"position": v(141.22, 328.82) * mm});
            skPoint(sketch, "E5.0.9.26", {"position": v(141.22, 340.6) * mm});
            skPoint(sketch, "E5.0.9.27", {"position": v(141.22, 352.39) * mm});
            skPoint(sketch, "E5.0.9.28", {"position": v(141.22, 364.17) * mm});
            skPoint(sketch, "E5.0.9.29", {"position": v(141.22, 375.96) * mm});
            skPoint(sketch, "E5.0.9.30", {"position": v(141.22, 387.74) * mm});
            skPoint(sketch, "E5.0.9.31", {"position": v(141.22, 399.53) * mm});
            skPoint(sketch, "E5.0.9.32", {"position": v(141.22, 411.31) * mm});
            skPoint(sketch, "E5.0.9.33", {"position": v(141.22, 423.1) * mm});
            skPoint(sketch, "E5.0.9.34", {"position": v(141.22, 434.88) * mm});
            skPoint(sketch, "E5.0.9.35", {"position": v(141.22, 446.67) * mm});
            skPoint(sketch, "E5.0.9.36", {"position": v(141.22, 458.45) * mm});
            skPoint(sketch, "E5.0.9.37", {"position": v(141.22, 470.24) * mm});
            skPoint(sketch, "E5.0.9.38", {"position": v(141.22, 482.02) * mm});
            skPoint(sketch, "E5.0.9.39", {"position": v(141.22, 493.8) * mm});
            skPoint(sketch, "E5.0.9.40", {"position": v(141.22, 505.6) * mm});
            skPoint(sketch, "E5.0.9.41", {"position": v(141.22, 517.38) * mm});
            skPoint(sketch, "E5.0.9.42", {"position": v(141.22, 529.16) * mm});
            skPoint(sketch, "E5.0.9.43", {"position": v(141.22, 540.95) * mm});
            skPoint(sketch, "E5.0.9.44", {"position": v(141.22, 552.73) * mm});
            skPoint(sketch, "E5.0.9.45", {"position": v(141.22, 564.52) * mm});
            skPoint(sketch, "E5.0.9.46", {"position": v(141.22, 576.3) * mm});
            skPoint(sketch, "E5.0.9.47", {"position": v(141.22, 588.09) * mm});
            skPoint(sketch, "E5.0.10.0", {"position": v(153, 34.19) * mm});
            skPoint(sketch, "E5.0.10.1", {"position": v(153, 45.97) * mm});
            skPoint(sketch, "E5.0.10.2", {"position": v(153, 57.76) * mm});
            skPoint(sketch, "E5.0.10.3", {"position": v(153, 69.54) * mm});
            skPoint(sketch, "E5.0.10.4", {"position": v(153, 81.33) * mm});
            skPoint(sketch, "E5.0.10.5", {"position": v(153, 93.11) * mm});
            skPoint(sketch, "E5.0.10.6", {"position": v(153, 104.9) * mm});
            skPoint(sketch, "E5.0.10.7", {"position": v(153, 116.68) * mm});
            skPoint(sketch, "E5.0.10.8", {"position": v(153, 128.47) * mm});
            skPoint(sketch, "E5.0.10.9", {"position": v(153, 140.25) * mm});
            skPoint(sketch, "E5.0.10.10", {"position": v(153, 152.04) * mm});
            skPoint(sketch, "E5.0.10.11", {"position": v(153, 163.82) * mm});
            skPoint(sketch, "E5.0.10.12", {"position": v(153, 175.6) * mm});
            skPoint(sketch, "E5.0.10.13", {"position": v(153, 187.4) * mm});
            skPoint(sketch, "E5.0.10.14", {"position": v(153, 199.18) * mm});
            skPoint(sketch, "E5.0.10.15", {"position": v(153, 210.97) * mm});
            skPoint(sketch, "E5.0.10.16", {"position": v(153, 222.75) * mm});
            skPoint(sketch, "E5.0.10.17", {"position": v(153, 234.54) * mm});
            skPoint(sketch, "E5.0.10.18", {"position": v(153, 246.32) * mm});
            skPoint(sketch, "E5.0.10.19", {"position": v(153, 258.1) * mm});
            skPoint(sketch, "E5.0.10.20", {"position": v(153, 269.9) * mm});
            skPoint(sketch, "E5.0.10.21", {"position": v(153, 281.68) * mm});
            skPoint(sketch, "E5.0.10.22", {"position": v(153, 293.46) * mm});
            skPoint(sketch, "E5.0.10.23", {"position": v(153, 305.25) * mm});
            skPoint(sketch, "E5.0.10.24", {"position": v(153, 317.03) * mm});
            skPoint(sketch, "E5.0.10.25", {"position": v(153, 328.82) * mm});
            skPoint(sketch, "E5.0.10.26", {"position": v(153, 340.6) * mm});
            skPoint(sketch, "E5.0.10.27", {"position": v(153, 352.39) * mm});
            skPoint(sketch, "E5.0.10.28", {"position": v(153, 364.17) * mm});
            skPoint(sketch, "E5.0.10.29", {"position": v(153, 375.96) * mm});
            skPoint(sketch, "E5.0.10.30", {"position": v(153, 387.74) * mm});
            skPoint(sketch, "E5.0.10.31", {"position": v(153, 399.53) * mm});
            skPoint(sketch, "E5.0.10.32", {"position": v(153, 411.31) * mm});
            skPoint(sketch, "E5.0.10.33", {"position": v(153, 423.1) * mm});
            skPoint(sketch, "E5.0.10.34", {"position": v(153, 434.88) * mm});
            skPoint(sketch, "E5.0.10.35", {"position": v(153, 446.67) * mm});
            skPoint(sketch, "E5.0.10.36", {"position": v(153, 458.45) * mm});
            skPoint(sketch, "E5.0.10.37", {"position": v(153, 470.24) * mm});
            skPoint(sketch, "E5.0.10.38", {"position": v(153, 482.02) * mm});
            skPoint(sketch, "E5.0.10.39", {"position": v(153, 493.8) * mm});
            skPoint(sketch, "E5.0.10.40", {"position": v(153, 505.6) * mm});
            skPoint(sketch, "E5.0.10.41", {"position": v(153, 517.38) * mm});
            skPoint(sketch, "E5.0.10.42", {"position": v(153, 529.16) * mm});
            skPoint(sketch, "E5.0.10.43", {"position": v(153, 540.95) * mm});
            skPoint(sketch, "E5.0.10.44", {"position": v(153, 552.73) * mm});
            skPoint(sketch, "E5.0.10.45", {"position": v(153, 564.52) * mm});
            skPoint(sketch, "E5.0.10.46", {"position": v(153, 576.3) * mm});
            skPoint(sketch, "E5.0.10.47", {"position": v(153, 588.09) * mm});
            skPoint(sketch, "E5.0.11.0", {"position": v(164.79, 34.19) * mm});
            skPoint(sketch, "E5.0.11.1", {"position": v(164.79, 45.97) * mm});
            skPoint(sketch, "E5.0.11.2", {"position": v(164.79, 57.76) * mm});
            skPoint(sketch, "E5.0.11.3", {"position": v(164.79, 69.54) * mm});
            skPoint(sketch, "E5.0.11.4", {"position": v(164.79, 81.33) * mm});
            skPoint(sketch, "E5.0.11.5", {"position": v(164.79, 93.11) * mm});
            skPoint(sketch, "E5.0.11.6", {"position": v(164.79, 104.9) * mm});
            skPoint(sketch, "E5.0.11.7", {"position": v(164.79, 116.68) * mm});
            skPoint(sketch, "E5.0.11.8", {"position": v(164.79, 128.47) * mm});
            skPoint(sketch, "E5.0.11.9", {"position": v(164.79, 140.25) * mm});
            skPoint(sketch, "E5.0.11.10", {"position": v(164.79, 152.04) * mm});
            skPoint(sketch, "E5.0.11.11", {"position": v(164.79, 163.82) * mm});
            skPoint(sketch, "E5.0.11.12", {"position": v(164.79, 175.6) * mm});
            skPoint(sketch, "E5.0.11.13", {"position": v(164.79, 187.4) * mm});
            skPoint(sketch, "E5.0.11.14", {"position": v(164.79, 199.18) * mm});
            skPoint(sketch, "E5.0.11.15", {"position": v(164.79, 210.97) * mm});
            skPoint(sketch, "E5.0.11.16", {"position": v(164.79, 222.75) * mm});
            skPoint(sketch, "E5.0.11.17", {"position": v(164.79, 234.54) * mm});
            skPoint(sketch, "E5.0.11.18", {"position": v(164.79, 246.32) * mm});
            skPoint(sketch, "E5.0.11.19", {"position": v(164.79, 258.1) * mm});
            skPoint(sketch, "E5.0.11.20", {"position": v(164.79, 269.9) * mm});
            skPoint(sketch, "E5.0.11.21", {"position": v(164.79, 281.68) * mm});
            skPoint(sketch, "E5.0.11.22", {"position": v(164.79, 293.46) * mm});
            skPoint(sketch, "E5.0.11.23", {"position": v(164.79, 305.25) * mm});
            skPoint(sketch, "E5.0.11.24", {"position": v(164.79, 317.03) * mm});
            skPoint(sketch, "E5.0.11.25", {"position": v(164.79, 328.82) * mm});
            skPoint(sketch, "E5.0.11.26", {"position": v(164.79, 340.6) * mm});
            skPoint(sketch, "E5.0.11.27", {"position": v(164.79, 352.39) * mm});
            skPoint(sketch, "E5.0.11.28", {"position": v(164.79, 364.17) * mm});
            skPoint(sketch, "E5.0.11.29", {"position": v(164.79, 375.96) * mm});
            skPoint(sketch, "E5.0.11.30", {"position": v(164.79, 387.74) * mm});
            skPoint(sketch, "E5.0.11.31", {"position": v(164.79, 399.53) * mm});
            skPoint(sketch, "E5.0.11.32", {"position": v(164.79, 411.31) * mm});
            skPoint(sketch, "E5.0.11.33", {"position": v(164.79, 423.1) * mm});
            skPoint(sketch, "E5.0.11.34", {"position": v(164.79, 434.88) * mm});
            skPoint(sketch, "E5.0.11.35", {"position": v(164.79, 446.67) * mm});
            skPoint(sketch, "E5.0.11.36", {"position": v(164.79, 458.45) * mm});
            skPoint(sketch, "E5.0.11.37", {"position": v(164.79, 470.24) * mm});
            skPoint(sketch, "E5.0.11.38", {"position": v(164.79, 482.02) * mm});
            skPoint(sketch, "E5.0.11.39", {"position": v(164.79, 493.8) * mm});
            skPoint(sketch, "E5.0.11.40", {"position": v(164.79, 505.6) * mm});
            skPoint(sketch, "E5.0.11.41", {"position": v(164.79, 517.38) * mm});
            skPoint(sketch, "E5.0.11.42", {"position": v(164.79, 529.16) * mm});
            skPoint(sketch, "E5.0.11.43", {"position": v(164.79, 540.95) * mm});
            skPoint(sketch, "E5.0.11.44", {"position": v(164.79, 552.73) * mm});
            skPoint(sketch, "E5.0.11.45", {"position": v(164.79, 564.52) * mm});
            skPoint(sketch, "E5.0.11.46", {"position": v(164.79, 576.3) * mm});
            skPoint(sketch, "E5.0.11.47", {"position": v(164.79, 588.09) * mm});
            skPoint(sketch, "E5.0.12.0", {"position": v(176.57, 34.19) * mm});
            skPoint(sketch, "E5.0.12.1", {"position": v(176.57, 45.97) * mm});
            skPoint(sketch, "E5.0.12.2", {"position": v(176.57, 57.76) * mm});
            skPoint(sketch, "E5.0.12.3", {"position": v(176.57, 69.54) * mm});
            skPoint(sketch, "E5.0.12.4", {"position": v(176.57, 81.33) * mm});
            skPoint(sketch, "E5.0.12.5", {"position": v(176.57, 93.11) * mm});
            skPoint(sketch, "E5.0.12.6", {"position": v(176.57, 104.9) * mm});
            skPoint(sketch, "E5.0.12.7", {"position": v(176.57, 116.68) * mm});
            skPoint(sketch, "E5.0.12.8", {"position": v(176.57, 128.47) * mm});
            skPoint(sketch, "E5.0.12.9", {"position": v(176.57, 140.25) * mm});
            skPoint(sketch, "E5.0.12.10", {"position": v(176.57, 152.04) * mm});
            skPoint(sketch, "E5.0.12.11", {"position": v(176.57, 163.82) * mm});
            skPoint(sketch, "E5.0.12.12", {"position": v(176.57, 175.6) * mm});
            skPoint(sketch, "E5.0.12.13", {"position": v(176.57, 187.4) * mm});
            skPoint(sketch, "E5.0.12.14", {"position": v(176.57, 199.18) * mm});
            skPoint(sketch, "E5.0.12.15", {"position": v(176.57, 210.97) * mm});
            skPoint(sketch, "E5.0.12.16", {"position": v(176.57, 222.75) * mm});
            skPoint(sketch, "E5.0.12.17", {"position": v(176.57, 234.54) * mm});
            skPoint(sketch, "E5.0.12.18", {"position": v(176.57, 246.32) * mm});
            skPoint(sketch, "E5.0.12.19", {"position": v(176.57, 258.1) * mm});
            skPoint(sketch, "E5.0.12.20", {"position": v(176.57, 269.9) * mm});
            skPoint(sketch, "E5.0.12.21", {"position": v(176.57, 281.68) * mm});
            skPoint(sketch, "E5.0.12.22", {"position": v(176.57, 293.46) * mm});
            skPoint(sketch, "E5.0.12.23", {"position": v(176.57, 305.25) * mm});
            skPoint(sketch, "E5.0.12.24", {"position": v(176.57, 317.03) * mm});
            skPoint(sketch, "E5.0.12.25", {"position": v(176.57, 328.82) * mm});
            skPoint(sketch, "E5.0.12.26", {"position": v(176.57, 340.6) * mm});
            skPoint(sketch, "E5.0.12.27", {"position": v(176.57, 352.39) * mm});
            skPoint(sketch, "E5.0.12.28", {"position": v(176.57, 364.17) * mm});
            skPoint(sketch, "E5.0.12.29", {"position": v(176.57, 375.96) * mm});
            skPoint(sketch, "E5.0.12.30", {"position": v(176.57, 387.74) * mm});
            skPoint(sketch, "E5.0.12.31", {"position": v(176.57, 399.53) * mm});
            skPoint(sketch, "E5.0.12.32", {"position": v(176.57, 411.31) * mm});
            skPoint(sketch, "E5.0.12.33", {"position": v(176.57, 423.1) * mm});
            skPoint(sketch, "E5.0.12.34", {"position": v(176.57, 434.88) * mm});
            skPoint(sketch, "E5.0.12.35", {"position": v(176.57, 446.67) * mm});
            skPoint(sketch, "E5.0.12.36", {"position": v(176.57, 458.45) * mm});
            skPoint(sketch, "E5.0.12.37", {"position": v(176.57, 470.24) * mm});
            skPoint(sketch, "E5.0.12.38", {"position": v(176.57, 482.02) * mm});
            skPoint(sketch, "E5.0.12.39", {"position": v(176.57, 493.8) * mm});
            skPoint(sketch, "E5.0.12.40", {"position": v(176.57, 505.6) * mm});
            skPoint(sketch, "E5.0.12.41", {"position": v(176.57, 517.38) * mm});
            skPoint(sketch, "E5.0.12.42", {"position": v(176.57, 529.16) * mm});
            skPoint(sketch, "E5.0.12.43", {"position": v(176.57, 540.95) * mm});
            skPoint(sketch, "E5.0.12.44", {"position": v(176.57, 552.73) * mm});
            skPoint(sketch, "E5.0.12.45", {"position": v(176.57, 564.52) * mm});
            skPoint(sketch, "E5.0.12.46", {"position": v(176.57, 576.3) * mm});
            skPoint(sketch, "E5.0.12.47", {"position": v(176.57, 588.09) * mm});
            skPoint(sketch, "E5.0.13.0", {"position": v(188.36, 34.19) * mm});
            skPoint(sketch, "E5.0.13.1", {"position": v(188.36, 45.97) * mm});
            skPoint(sketch, "E5.0.13.2", {"position": v(188.36, 57.76) * mm});
            skPoint(sketch, "E5.0.13.3", {"position": v(188.36, 69.54) * mm});
            skPoint(sketch, "E5.0.13.4", {"position": v(188.36, 81.33) * mm});
            skPoint(sketch, "E5.0.13.5", {"position": v(188.36, 93.11) * mm});
            skPoint(sketch, "E5.0.13.6", {"position": v(188.36, 104.9) * mm});
            skPoint(sketch, "E5.0.13.7", {"position": v(188.36, 116.68) * mm});
            skPoint(sketch, "E5.0.13.8", {"position": v(188.36, 128.47) * mm});
            skPoint(sketch, "E5.0.13.9", {"position": v(188.36, 140.25) * mm});
            skPoint(sketch, "E5.0.13.10", {"position": v(188.36, 152.04) * mm});
            skPoint(sketch, "E5.0.13.11", {"position": v(188.36, 163.82) * mm});
            skPoint(sketch, "E5.0.13.12", {"position": v(188.36, 175.6) * mm});
            skPoint(sketch, "E5.0.13.13", {"position": v(188.36, 187.4) * mm});
            skPoint(sketch, "E5.0.13.14", {"position": v(188.36, 199.18) * mm});
            skPoint(sketch, "E5.0.13.15", {"position": v(188.36, 210.97) * mm});
            skPoint(sketch, "E5.0.13.16", {"position": v(188.36, 222.75) * mm});
            skPoint(sketch, "E5.0.13.17", {"position": v(188.36, 234.54) * mm});
            skPoint(sketch, "E5.0.13.18", {"position": v(188.36, 246.32) * mm});
            skPoint(sketch, "E5.0.13.19", {"position": v(188.36, 258.1) * mm});
            skPoint(sketch, "E5.0.13.20", {"position": v(188.36, 269.9) * mm});
            skPoint(sketch, "E5.0.13.21", {"position": v(188.36, 281.68) * mm});
            skPoint(sketch, "E5.0.13.22", {"position": v(188.36, 293.46) * mm});
            skPoint(sketch, "E5.0.13.23", {"position": v(188.36, 305.25) * mm});
            skPoint(sketch, "E5.0.13.24", {"position": v(188.36, 317.03) * mm});
            skPoint(sketch, "E5.0.13.25", {"position": v(188.36, 328.82) * mm});
            skPoint(sketch, "E5.0.13.26", {"position": v(188.36, 340.6) * mm});
            skPoint(sketch, "E5.0.13.27", {"position": v(188.36, 352.39) * mm});
            skPoint(sketch, "E5.0.13.28", {"position": v(188.36, 364.17) * mm});
            skPoint(sketch, "E5.0.13.29", {"position": v(188.36, 375.96) * mm});
            skPoint(sketch, "E5.0.13.30", {"position": v(188.36, 387.74) * mm});
            skPoint(sketch, "E5.0.13.31", {"position": v(188.36, 399.53) * mm});
            skPoint(sketch, "E5.0.13.32", {"position": v(188.36, 411.31) * mm});
            skPoint(sketch, "E5.0.13.33", {"position": v(188.36, 423.1) * mm});
            skPoint(sketch, "E5.0.13.34", {"position": v(188.36, 434.88) * mm});
            skPoint(sketch, "E5.0.13.35", {"position": v(188.36, 446.67) * mm});
            skPoint(sketch, "E5.0.13.36", {"position": v(188.36, 458.45) * mm});
            skPoint(sketch, "E5.0.13.37", {"position": v(188.36, 470.24) * mm});
            skPoint(sketch, "E5.0.13.38", {"position": v(188.36, 482.02) * mm});
            skPoint(sketch, "E5.0.13.39", {"position": v(188.36, 493.8) * mm});
            skPoint(sketch, "E5.0.13.40", {"position": v(188.36, 505.6) * mm});
            skPoint(sketch, "E5.0.13.41", {"position": v(188.36, 517.38) * mm});
            skPoint(sketch, "E5.0.13.42", {"position": v(188.36, 529.16) * mm});
            skPoint(sketch, "E5.0.13.43", {"position": v(188.36, 540.95) * mm});
            skPoint(sketch, "E5.0.13.44", {"position": v(188.36, 552.73) * mm});
            skPoint(sketch, "E5.0.13.45", {"position": v(188.36, 564.52) * mm});
            skPoint(sketch, "E5.0.13.46", {"position": v(188.36, 576.3) * mm});
            skPoint(sketch, "E5.0.13.47", {"position": v(188.36, 588.09) * mm});
            skPoint(sketch, "E5.0.14.0", {"position": v(200.15, 34.19) * mm});
            skPoint(sketch, "E5.0.14.1", {"position": v(200.15, 45.97) * mm});
            skPoint(sketch, "E5.0.14.2", {"position": v(200.15, 57.76) * mm});
            skPoint(sketch, "E5.0.14.3", {"position": v(200.15, 69.54) * mm});
            skPoint(sketch, "E5.0.14.4", {"position": v(200.15, 81.33) * mm});
            skPoint(sketch, "E5.0.14.5", {"position": v(200.15, 93.11) * mm});
            skPoint(sketch, "E5.0.14.6", {"position": v(200.15, 104.9) * mm});
            skPoint(sketch, "E5.0.14.7", {"position": v(200.15, 116.68) * mm});
            skPoint(sketch, "E5.0.14.8", {"position": v(200.15, 128.47) * mm});
            skPoint(sketch, "E5.0.14.9", {"position": v(200.15, 140.25) * mm});
            skPoint(sketch, "E5.0.14.10", {"position": v(200.15, 152.04) * mm});
            skPoint(sketch, "E5.0.14.11", {"position": v(200.15, 163.82) * mm});
            skPoint(sketch, "E5.0.14.12", {"position": v(200.15, 175.6) * mm});
            skPoint(sketch, "E5.0.14.13", {"position": v(200.15, 187.4) * mm});
            skPoint(sketch, "E5.0.14.14", {"position": v(200.15, 199.18) * mm});
            skPoint(sketch, "E5.0.14.15", {"position": v(200.15, 210.97) * mm});
            skPoint(sketch, "E5.0.14.16", {"position": v(200.15, 222.75) * mm});
            skPoint(sketch, "E5.0.14.17", {"position": v(200.15, 234.54) * mm});
            skPoint(sketch, "E5.0.14.18", {"position": v(200.15, 246.32) * mm});
            skPoint(sketch, "E5.0.14.19", {"position": v(200.15, 258.1) * mm});
            skPoint(sketch, "E5.0.14.20", {"position": v(200.15, 269.9) * mm});
            skPoint(sketch, "E5.0.14.21", {"position": v(200.15, 281.68) * mm});
            skPoint(sketch, "E5.0.14.22", {"position": v(200.15, 293.46) * mm});
            skPoint(sketch, "E5.0.14.23", {"position": v(200.15, 305.25) * mm});
            skPoint(sketch, "E5.0.14.24", {"position": v(200.15, 317.03) * mm});
            skPoint(sketch, "E5.0.14.25", {"position": v(200.15, 328.82) * mm});
            skPoint(sketch, "E5.0.14.26", {"position": v(200.15, 340.6) * mm});
            skPoint(sketch, "E5.0.14.27", {"position": v(200.15, 352.39) * mm});
            skPoint(sketch, "E5.0.14.28", {"position": v(200.15, 364.17) * mm});
            skPoint(sketch, "E5.0.14.29", {"position": v(200.15, 375.96) * mm});
            skPoint(sketch, "E5.0.14.30", {"position": v(200.15, 387.74) * mm});
            skPoint(sketch, "E5.0.14.31", {"position": v(200.15, 399.53) * mm});
            skPoint(sketch, "E5.0.14.32", {"position": v(200.15, 411.31) * mm});
            skPoint(sketch, "E5.0.14.33", {"position": v(200.15, 423.1) * mm});
            skPoint(sketch, "E5.0.14.34", {"position": v(200.15, 434.88) * mm});
            skPoint(sketch, "E5.0.14.35", {"position": v(200.15, 446.67) * mm});
            skPoint(sketch, "E5.0.14.36", {"position": v(200.15, 458.45) * mm});
            skPoint(sketch, "E5.0.14.37", {"position": v(200.15, 470.24) * mm});
            skPoint(sketch, "E5.0.14.38", {"position": v(200.15, 482.02) * mm});
            skPoint(sketch, "E5.0.14.39", {"position": v(200.15, 493.8) * mm});
            skPoint(sketch, "E5.0.14.40", {"position": v(200.15, 505.6) * mm});
            skPoint(sketch, "E5.0.14.41", {"position": v(200.15, 517.38) * mm});
            skPoint(sketch, "E5.0.14.42", {"position": v(200.15, 529.16) * mm});
            skPoint(sketch, "E5.0.14.43", {"position": v(200.15, 540.95) * mm});
            skPoint(sketch, "E5.0.14.44", {"position": v(200.15, 552.73) * mm});
            skPoint(sketch, "E5.0.14.45", {"position": v(200.15, 564.52) * mm});
            skPoint(sketch, "E5.0.14.46", {"position": v(200.15, 576.3) * mm});
            skPoint(sketch, "E5.0.14.47", {"position": v(200.15, 588.09) * mm});
            skPoint(sketch, "E5.0.15.0", {"position": v(211.93, 34.19) * mm});
            skPoint(sketch, "E5.0.15.1", {"position": v(211.93, 45.97) * mm});
            skPoint(sketch, "E5.0.15.2", {"position": v(211.93, 57.76) * mm});
            skPoint(sketch, "E5.0.15.3", {"position": v(211.93, 69.54) * mm});
            skPoint(sketch, "E5.0.15.4", {"position": v(211.93, 81.33) * mm});
            skPoint(sketch, "E5.0.15.5", {"position": v(211.93, 93.11) * mm});
            skPoint(sketch, "E5.0.15.6", {"position": v(211.93, 104.9) * mm});
            skPoint(sketch, "E5.0.15.7", {"position": v(211.93, 116.68) * mm});
            skPoint(sketch, "E5.0.15.8", {"position": v(211.93, 128.47) * mm});
            skPoint(sketch, "E5.0.15.9", {"position": v(211.93, 140.25) * mm});
            skPoint(sketch, "E5.0.15.10", {"position": v(211.93, 152.04) * mm});
            skPoint(sketch, "E5.0.15.11", {"position": v(211.93, 163.82) * mm});
            skPoint(sketch, "E5.0.15.12", {"position": v(211.93, 175.6) * mm});
            skPoint(sketch, "E5.0.15.13", {"position": v(211.93, 187.4) * mm});
            skPoint(sketch, "E5.0.15.14", {"position": v(211.93, 199.18) * mm});
            skPoint(sketch, "E5.0.15.15", {"position": v(211.93, 210.97) * mm});
            skPoint(sketch, "E5.0.15.16", {"position": v(211.93, 222.75) * mm});
            skPoint(sketch, "E5.0.15.17", {"position": v(211.93, 234.54) * mm});
            skPoint(sketch, "E5.0.15.18", {"position": v(211.93, 246.32) * mm});
            skPoint(sketch, "E5.0.15.19", {"position": v(211.93, 258.1) * mm});
            skPoint(sketch, "E5.0.15.20", {"position": v(211.93, 269.9) * mm});
            skPoint(sketch, "E5.0.15.21", {"position": v(211.93, 281.68) * mm});
            skPoint(sketch, "E5.0.15.22", {"position": v(211.93, 293.46) * mm});
            skPoint(sketch, "E5.0.15.23", {"position": v(211.93, 305.25) * mm});
            skPoint(sketch, "E5.0.15.24", {"position": v(211.93, 317.03) * mm});
            skPoint(sketch, "E5.0.15.25", {"position": v(211.93, 328.82) * mm});
            skPoint(sketch, "E5.0.15.26", {"position": v(211.93, 340.6) * mm});
            skPoint(sketch, "E5.0.15.27", {"position": v(211.93, 352.39) * mm});
            skPoint(sketch, "E5.0.15.28", {"position": v(211.93, 364.17) * mm});
            skPoint(sketch, "E5.0.15.29", {"position": v(211.93, 375.96) * mm});
            skPoint(sketch, "E5.0.15.30", {"position": v(211.93, 387.74) * mm});
            skPoint(sketch, "E5.0.15.31", {"position": v(211.93, 399.53) * mm});
            skPoint(sketch, "E5.0.15.32", {"position": v(211.93, 411.31) * mm});
            skPoint(sketch, "E5.0.15.33", {"position": v(211.93, 423.1) * mm});
            skPoint(sketch, "E5.0.15.34", {"position": v(211.93, 434.88) * mm});
            skPoint(sketch, "E5.0.15.35", {"position": v(211.93, 446.67) * mm});
            skPoint(sketch, "E5.0.15.36", {"position": v(211.93, 458.45) * mm});
            skPoint(sketch, "E5.0.15.37", {"position": v(211.93, 470.24) * mm});
            skPoint(sketch, "E5.0.15.38", {"position": v(211.93, 482.02) * mm});
            skPoint(sketch, "E5.0.15.39", {"position": v(211.93, 493.8) * mm});
            skPoint(sketch, "E5.0.15.40", {"position": v(211.93, 505.6) * mm});
            skPoint(sketch, "E5.0.15.41", {"position": v(211.93, 517.38) * mm});
            skPoint(sketch, "E5.0.15.42", {"position": v(211.93, 529.16) * mm});
            skPoint(sketch, "E5.0.15.43", {"position": v(211.93, 540.95) * mm});
            skPoint(sketch, "E5.0.15.44", {"position": v(211.93, 552.73) * mm});
            skPoint(sketch, "E5.0.15.45", {"position": v(211.93, 564.52) * mm});
            skPoint(sketch, "E5.0.15.46", {"position": v(211.93, 576.3) * mm});
            skPoint(sketch, "E5.0.15.47", {"position": v(211.93, 588.09) * mm});
            skPoint(sketch, "E5.0.16.0", {"position": v(223.72, 34.19) * mm});
            skPoint(sketch, "E5.0.16.1", {"position": v(223.72, 45.97) * mm});
            skPoint(sketch, "E5.0.16.2", {"position": v(223.72, 57.76) * mm});
            skPoint(sketch, "E5.0.16.3", {"position": v(223.72, 69.54) * mm});
            skPoint(sketch, "E5.0.16.4", {"position": v(223.72, 81.33) * mm});
            skPoint(sketch, "E5.0.16.5", {"position": v(223.72, 93.11) * mm});
            skPoint(sketch, "E5.0.16.6", {"position": v(223.72, 104.9) * mm});
            skPoint(sketch, "E5.0.16.7", {"position": v(223.72, 116.68) * mm});
            skPoint(sketch, "E5.0.16.8", {"position": v(223.72, 128.47) * mm});
            skPoint(sketch, "E5.0.16.9", {"position": v(223.72, 140.25) * mm});
            skPoint(sketch, "E5.0.16.10", {"position": v(223.72, 152.04) * mm});
            skPoint(sketch, "E5.0.16.11", {"position": v(223.72, 163.82) * mm});
            skPoint(sketch, "E5.0.16.12", {"position": v(223.72, 175.6) * mm});
            skPoint(sketch, "E5.0.16.13", {"position": v(223.72, 187.4) * mm});
            skPoint(sketch, "E5.0.16.14", {"position": v(223.72, 199.18) * mm});
            skPoint(sketch, "E5.0.16.15", {"position": v(223.72, 210.97) * mm});
            skPoint(sketch, "E5.0.16.16", {"position": v(223.72, 222.75) * mm});
            skPoint(sketch, "E5.0.16.17", {"position": v(223.72, 234.54) * mm});
            skPoint(sketch, "E5.0.16.18", {"position": v(223.72, 246.32) * mm});
            skPoint(sketch, "E5.0.16.19", {"position": v(223.72, 258.1) * mm});
            skPoint(sketch, "E5.0.16.20", {"position": v(223.72, 269.9) * mm});
            skPoint(sketch, "E5.0.16.21", {"position": v(223.72, 281.68) * mm});
            skPoint(sketch, "E5.0.16.22", {"position": v(223.72, 293.46) * mm});
            skPoint(sketch, "E5.0.16.23", {"position": v(223.72, 305.25) * mm});
            skPoint(sketch, "E5.0.16.24", {"position": v(223.72, 317.03) * mm});
            skPoint(sketch, "E5.0.16.25", {"position": v(223.72, 328.82) * mm});
            skPoint(sketch, "E5.0.16.26", {"position": v(223.72, 340.6) * mm});
            skPoint(sketch, "E5.0.16.27", {"position": v(223.72, 352.39) * mm});
            skPoint(sketch, "E5.0.16.28", {"position": v(223.72, 364.17) * mm});
            skPoint(sketch, "E5.0.16.29", {"position": v(223.72, 375.96) * mm});
            skPoint(sketch, "E5.0.16.30", {"position": v(223.72, 387.74) * mm});
            skPoint(sketch, "E5.0.16.31", {"position": v(223.72, 399.53) * mm});
            skPoint(sketch, "E5.0.16.32", {"position": v(223.72, 411.31) * mm});
            skPoint(sketch, "E5.0.16.33", {"position": v(223.72, 423.1) * mm});
            skPoint(sketch, "E5.0.16.34", {"position": v(223.72, 434.88) * mm});
            skPoint(sketch, "E5.0.16.35", {"position": v(223.72, 446.67) * mm});
            skPoint(sketch, "E5.0.16.36", {"position": v(223.72, 458.45) * mm});
            skPoint(sketch, "E5.0.16.37", {"position": v(223.72, 470.24) * mm});
            skPoint(sketch, "E5.0.16.38", {"position": v(223.72, 482.02) * mm});
            skPoint(sketch, "E5.0.16.39", {"position": v(223.72, 493.8) * mm});
            skPoint(sketch, "E5.0.16.40", {"position": v(223.72, 505.6) * mm});
            skPoint(sketch, "E5.0.16.41", {"position": v(223.72, 517.38) * mm});
            skPoint(sketch, "E5.0.16.42", {"position": v(223.72, 529.16) * mm});
            skPoint(sketch, "E5.0.16.43", {"position": v(223.72, 540.95) * mm});
            skPoint(sketch, "E5.0.16.44", {"position": v(223.72, 552.73) * mm});
            skPoint(sketch, "E5.0.16.45", {"position": v(223.72, 564.52) * mm});
            skPoint(sketch, "E5.0.16.46", {"position": v(223.72, 576.3) * mm});
            skPoint(sketch, "E5.0.16.47", {"position": v(223.72, 588.09) * mm});
            skPoint(sketch, "E5.0.17.0", {"position": v(235.5, 34.19) * mm});
            skPoint(sketch, "E5.0.17.1", {"position": v(235.5, 45.97) * mm});
            skPoint(sketch, "E5.0.17.2", {"position": v(235.5, 57.76) * mm});
            skPoint(sketch, "E5.0.17.3", {"position": v(235.5, 69.54) * mm});
            skPoint(sketch, "E5.0.17.4", {"position": v(235.5, 81.33) * mm});
            skPoint(sketch, "E5.0.17.5", {"position": v(235.5, 93.11) * mm});
            skPoint(sketch, "E5.0.17.6", {"position": v(235.5, 104.9) * mm});
            skPoint(sketch, "E5.0.17.7", {"position": v(235.5, 116.68) * mm});
            skPoint(sketch, "E5.0.17.8", {"position": v(235.5, 128.47) * mm});
            skPoint(sketch, "E5.0.17.9", {"position": v(235.5, 140.25) * mm});
            skPoint(sketch, "E5.0.17.10", {"position": v(235.5, 152.04) * mm});
            skPoint(sketch, "E5.0.17.11", {"position": v(235.5, 163.82) * mm});
            skPoint(sketch, "E5.0.17.12", {"position": v(235.5, 175.6) * mm});
            skPoint(sketch, "E5.0.17.13", {"position": v(235.5, 187.4) * mm});
            skPoint(sketch, "E5.0.17.14", {"position": v(235.5, 199.18) * mm});
            skPoint(sketch, "E5.0.17.15", {"position": v(235.5, 210.97) * mm});
            skPoint(sketch, "E5.0.17.16", {"position": v(235.5, 222.75) * mm});
            skPoint(sketch, "E5.0.17.17", {"position": v(235.5, 234.54) * mm});
            skPoint(sketch, "E5.0.17.18", {"position": v(235.5, 246.32) * mm});
            skPoint(sketch, "E5.0.17.19", {"position": v(235.5, 258.1) * mm});
            skPoint(sketch, "E5.0.17.20", {"position": v(235.5, 269.9) * mm});
            skPoint(sketch, "E5.0.17.21", {"position": v(235.5, 281.68) * mm});
            skPoint(sketch, "E5.0.17.22", {"position": v(235.5, 293.46) * mm});
            skPoint(sketch, "E5.0.17.23", {"position": v(235.5, 305.25) * mm});
            skPoint(sketch, "E5.0.17.24", {"position": v(235.5, 317.03) * mm});
            skPoint(sketch, "E5.0.17.25", {"position": v(235.5, 328.82) * mm});
            skPoint(sketch, "E5.0.17.26", {"position": v(235.5, 340.6) * mm});
            skPoint(sketch, "E5.0.17.27", {"position": v(235.5, 352.39) * mm});
            skPoint(sketch, "E5.0.17.28", {"position": v(235.5, 364.17) * mm});
            skPoint(sketch, "E5.0.17.29", {"position": v(235.5, 375.96) * mm});
            skPoint(sketch, "E5.0.17.30", {"position": v(235.5, 387.74) * mm});
            skPoint(sketch, "E5.0.17.31", {"position": v(235.5, 399.53) * mm});
            skPoint(sketch, "E5.0.17.32", {"position": v(235.5, 411.31) * mm});
            skPoint(sketch, "E5.0.17.33", {"position": v(235.5, 423.1) * mm});
            skPoint(sketch, "E5.0.17.34", {"position": v(235.5, 434.88) * mm});
            skPoint(sketch, "E5.0.17.35", {"position": v(235.5, 446.67) * mm});
            skPoint(sketch, "E5.0.17.36", {"position": v(235.5, 458.45) * mm});
            skPoint(sketch, "E5.0.17.37", {"position": v(235.5, 470.24) * mm});
            skPoint(sketch, "E5.0.17.38", {"position": v(235.5, 482.02) * mm});
            skPoint(sketch, "E5.0.17.39", {"position": v(235.5, 493.8) * mm});
            skPoint(sketch, "E5.0.17.40", {"position": v(235.5, 505.6) * mm});
            skPoint(sketch, "E5.0.17.41", {"position": v(235.5, 517.38) * mm});
            skPoint(sketch, "E5.0.17.42", {"position": v(235.5, 529.16) * mm});
            skPoint(sketch, "E5.0.17.43", {"position": v(235.5, 540.95) * mm});
            skPoint(sketch, "E5.0.17.44", {"position": v(235.5, 552.73) * mm});
            skPoint(sketch, "E5.0.17.45", {"position": v(235.5, 564.52) * mm});
            skPoint(sketch, "E5.0.17.46", {"position": v(235.5, 576.3) * mm});
            skPoint(sketch, "E5.0.17.47", {"position": v(235.5, 588.09) * mm});
            skPoint(sketch, "E5.0.18.0", {"position": v(247.29, 34.19) * mm});
            skPoint(sketch, "E5.0.18.1", {"position": v(247.29, 45.97) * mm});
            skPoint(sketch, "E5.0.18.2", {"position": v(247.29, 57.76) * mm});
            skPoint(sketch, "E5.0.18.3", {"position": v(247.29, 69.54) * mm});
            skPoint(sketch, "E5.0.18.4", {"position": v(247.29, 81.33) * mm});
            skPoint(sketch, "E5.0.18.5", {"position": v(247.29, 93.11) * mm});
            skPoint(sketch, "E5.0.18.6", {"position": v(247.29, 104.9) * mm});
            skPoint(sketch, "E5.0.18.7", {"position": v(247.29, 116.68) * mm});
            skPoint(sketch, "E5.0.18.8", {"position": v(247.29, 128.47) * mm});
            skPoint(sketch, "E5.0.18.9", {"position": v(247.29, 140.25) * mm});
            skPoint(sketch, "E5.0.18.10", {"position": v(247.29, 152.04) * mm});
            skPoint(sketch, "E5.0.18.11", {"position": v(247.29, 163.82) * mm});
            skPoint(sketch, "E5.0.18.12", {"position": v(247.29, 175.6) * mm});
            skPoint(sketch, "E5.0.18.13", {"position": v(247.29, 187.4) * mm});
            skPoint(sketch, "E5.0.18.14", {"position": v(247.29, 199.18) * mm});
            skPoint(sketch, "E5.0.18.15", {"position": v(247.29, 210.97) * mm});
            skPoint(sketch, "E5.0.18.16", {"position": v(247.29, 222.75) * mm});
            skPoint(sketch, "E5.0.18.17", {"position": v(247.29, 234.54) * mm});
            skPoint(sketch, "E5.0.18.18", {"position": v(247.29, 246.32) * mm});
            skPoint(sketch, "E5.0.18.19", {"position": v(247.29, 258.1) * mm});
            skPoint(sketch, "E5.0.18.20", {"position": v(247.29, 269.9) * mm});
            skPoint(sketch, "E5.0.18.21", {"position": v(247.29, 281.68) * mm});
            skPoint(sketch, "E5.0.18.22", {"position": v(247.29, 293.46) * mm});
            skPoint(sketch, "E5.0.18.23", {"position": v(247.29, 305.25) * mm});
            skPoint(sketch, "E5.0.18.24", {"position": v(247.29, 317.03) * mm});
            skPoint(sketch, "E5.0.18.25", {"position": v(247.29, 328.82) * mm});
            skPoint(sketch, "E5.0.18.26", {"position": v(247.29, 340.6) * mm});
            skPoint(sketch, "E5.0.18.27", {"position": v(247.29, 352.39) * mm});
            skPoint(sketch, "E5.0.18.28", {"position": v(247.29, 364.17) * mm});
            skPoint(sketch, "E5.0.18.29", {"position": v(247.29, 375.96) * mm});
            skPoint(sketch, "E5.0.18.30", {"position": v(247.29, 387.74) * mm});
            skPoint(sketch, "E5.0.18.31", {"position": v(247.29, 399.53) * mm});
            skPoint(sketch, "E5.0.18.32", {"position": v(247.29, 411.31) * mm});
            skPoint(sketch, "E5.0.18.33", {"position": v(247.29, 423.1) * mm});
            skPoint(sketch, "E5.0.18.34", {"position": v(247.29, 434.88) * mm});
            skPoint(sketch, "E5.0.18.35", {"position": v(247.29, 446.67) * mm});
            skPoint(sketch, "E5.0.18.36", {"position": v(247.29, 458.45) * mm});
            skPoint(sketch, "E5.0.18.37", {"position": v(247.29, 470.24) * mm});
            skPoint(sketch, "E5.0.18.38", {"position": v(247.29, 482.02) * mm});
            skPoint(sketch, "E5.0.18.39", {"position": v(247.29, 493.8) * mm});
            skPoint(sketch, "E5.0.18.40", {"position": v(247.29, 505.6) * mm});
            skPoint(sketch, "E5.0.18.41", {"position": v(247.29, 517.38) * mm});
            skPoint(sketch, "E5.0.18.42", {"position": v(247.29, 529.16) * mm});
            skPoint(sketch, "E5.0.18.43", {"position": v(247.29, 540.95) * mm});
            skPoint(sketch, "E5.0.18.44", {"position": v(247.29, 552.73) * mm});
            skPoint(sketch, "E5.0.18.45", {"position": v(247.29, 564.52) * mm});
            skPoint(sketch, "E5.0.18.46", {"position": v(247.29, 576.3) * mm});
            skPoint(sketch, "E5.0.18.47", {"position": v(247.29, 588.09) * mm});
            skPoint(sketch, "E5.0.19.0", {"position": v(259.07, 34.19) * mm});
            skPoint(sketch, "E5.0.19.1", {"position": v(259.07, 45.97) * mm});
            skPoint(sketch, "E5.0.19.2", {"position": v(259.07, 57.76) * mm});
            skPoint(sketch, "E5.0.19.3", {"position": v(259.07, 69.54) * mm});
            skPoint(sketch, "E5.0.19.4", {"position": v(259.07, 81.33) * mm});
            skPoint(sketch, "E5.0.19.5", {"position": v(259.07, 93.11) * mm});
            skPoint(sketch, "E5.0.19.6", {"position": v(259.07, 104.9) * mm});
            skPoint(sketch, "E5.0.19.7", {"position": v(259.07, 116.68) * mm});
            skPoint(sketch, "E5.0.19.8", {"position": v(259.07, 128.47) * mm});
            skPoint(sketch, "E5.0.19.9", {"position": v(259.07, 140.25) * mm});
            skPoint(sketch, "E5.0.19.10", {"position": v(259.07, 152.04) * mm});
            skPoint(sketch, "E5.0.19.11", {"position": v(259.07, 163.82) * mm});
            skPoint(sketch, "E5.0.19.12", {"position": v(259.07, 175.6) * mm});
            skPoint(sketch, "E5.0.19.13", {"position": v(259.07, 187.4) * mm});
            skPoint(sketch, "E5.0.19.14", {"position": v(259.07, 199.18) * mm});
            skPoint(sketch, "E5.0.19.15", {"position": v(259.07, 210.97) * mm});
            skPoint(sketch, "E5.0.19.16", {"position": v(259.07, 222.75) * mm});
            skPoint(sketch, "E5.0.19.17", {"position": v(259.07, 234.54) * mm});
            skPoint(sketch, "E5.0.19.18", {"position": v(259.07, 246.32) * mm});
            skPoint(sketch, "E5.0.19.19", {"position": v(259.07, 258.1) * mm});
            skPoint(sketch, "E5.0.19.20", {"position": v(259.07, 269.9) * mm});
            skPoint(sketch, "E5.0.19.21", {"position": v(259.07, 281.68) * mm});
            skPoint(sketch, "E5.0.19.22", {"position": v(259.07, 293.46) * mm});
            skPoint(sketch, "E5.0.19.23", {"position": v(259.07, 305.25) * mm});
            skPoint(sketch, "E5.0.19.24", {"position": v(259.07, 317.03) * mm});
            skPoint(sketch, "E5.0.19.25", {"position": v(259.07, 328.82) * mm});
            skPoint(sketch, "E5.0.19.26", {"position": v(259.07, 340.6) * mm});
            skPoint(sketch, "E5.0.19.27", {"position": v(259.07, 352.39) * mm});
            skPoint(sketch, "E5.0.19.28", {"position": v(259.07, 364.17) * mm});
            skPoint(sketch, "E5.0.19.29", {"position": v(259.07, 375.96) * mm});
            skPoint(sketch, "E5.0.19.30", {"position": v(259.07, 387.74) * mm});
            skPoint(sketch, "E5.0.19.31", {"position": v(259.07, 399.53) * mm});
            skPoint(sketch, "E5.0.19.32", {"position": v(259.07, 411.31) * mm});
            skPoint(sketch, "E5.0.19.33", {"position": v(259.07, 423.1) * mm});
            skPoint(sketch, "E5.0.19.34", {"position": v(259.07, 434.88) * mm});
            skPoint(sketch, "E5.0.19.35", {"position": v(259.07, 446.67) * mm});
            skPoint(sketch, "E5.0.19.36", {"position": v(259.07, 458.45) * mm});
            skPoint(sketch, "E5.0.19.37", {"position": v(259.07, 470.24) * mm});
            skPoint(sketch, "E5.0.19.38", {"position": v(259.07, 482.02) * mm});
            skPoint(sketch, "E5.0.19.39", {"position": v(259.07, 493.8) * mm});
            skPoint(sketch, "E5.0.19.40", {"position": v(259.07, 505.6) * mm});
            skPoint(sketch, "E5.0.19.41", {"position": v(259.07, 517.38) * mm});
            skPoint(sketch, "E5.0.19.42", {"position": v(259.07, 529.16) * mm});
            skPoint(sketch, "E5.0.19.43", {"position": v(259.07, 540.95) * mm});
            skPoint(sketch, "E5.0.19.44", {"position": v(259.07, 552.73) * mm});
            skPoint(sketch, "E5.0.19.45", {"position": v(259.07, 564.52) * mm});
            skPoint(sketch, "E5.0.19.46", {"position": v(259.07, 576.3) * mm});
            skPoint(sketch, "E5.0.19.47", {"position": v(259.07, 588.09) * mm});
            skPoint(sketch, "E5.0.20.0", {"position": v(270.86, 34.19) * mm});
            skPoint(sketch, "E5.0.20.1", {"position": v(270.86, 45.97) * mm});
            skPoint(sketch, "E5.0.20.2", {"position": v(270.86, 57.76) * mm});
            skPoint(sketch, "E5.0.20.3", {"position": v(270.86, 69.54) * mm});
            skPoint(sketch, "E5.0.20.4", {"position": v(270.86, 81.33) * mm});
            skPoint(sketch, "E5.0.20.5", {"position": v(270.86, 93.11) * mm});
            skPoint(sketch, "E5.0.20.6", {"position": v(270.86, 104.9) * mm});
            skPoint(sketch, "E5.0.20.7", {"position": v(270.86, 116.68) * mm});
            skPoint(sketch, "E5.0.20.8", {"position": v(270.86, 128.47) * mm});
            skPoint(sketch, "E5.0.20.9", {"position": v(270.86, 140.25) * mm});
            skPoint(sketch, "E5.0.20.10", {"position": v(270.86, 152.04) * mm});
            skPoint(sketch, "E5.0.20.11", {"position": v(270.86, 163.82) * mm});
            skPoint(sketch, "E5.0.20.12", {"position": v(270.86, 175.6) * mm});
            skPoint(sketch, "E5.0.20.13", {"position": v(270.86, 187.4) * mm});
            skPoint(sketch, "E5.0.20.14", {"position": v(270.86, 199.18) * mm});
            skPoint(sketch, "E5.0.20.15", {"position": v(270.86, 210.97) * mm});
            skPoint(sketch, "E5.0.20.16", {"position": v(270.86, 222.75) * mm});
            skPoint(sketch, "E5.0.20.17", {"position": v(270.86, 234.54) * mm});
            skPoint(sketch, "E5.0.20.18", {"position": v(270.86, 246.32) * mm});
            skPoint(sketch, "E5.0.20.19", {"position": v(270.86, 258.1) * mm});
            skPoint(sketch, "E5.0.20.20", {"position": v(270.86, 269.9) * mm});
            skPoint(sketch, "E5.0.20.21", {"position": v(270.86, 281.68) * mm});
            skPoint(sketch, "E5.0.20.22", {"position": v(270.86, 293.46) * mm});
            skPoint(sketch, "E5.0.20.23", {"position": v(270.86, 305.25) * mm});
            skPoint(sketch, "E5.0.20.24", {"position": v(270.86, 317.03) * mm});
            skPoint(sketch, "E5.0.20.25", {"position": v(270.86, 328.82) * mm});
            skPoint(sketch, "E5.0.20.26", {"position": v(270.86, 340.6) * mm});
            skPoint(sketch, "E5.0.20.27", {"position": v(270.86, 352.39) * mm});
            skPoint(sketch, "E5.0.20.28", {"position": v(270.86, 364.17) * mm});
            skPoint(sketch, "E5.0.20.29", {"position": v(270.86, 375.96) * mm});
            skPoint(sketch, "E5.0.20.30", {"position": v(270.86, 387.74) * mm});
            skPoint(sketch, "E5.0.20.31", {"position": v(270.86, 399.53) * mm});
            skPoint(sketch, "E5.0.20.32", {"position": v(270.86, 411.31) * mm});
            skPoint(sketch, "E5.0.20.33", {"position": v(270.86, 423.1) * mm});
            skPoint(sketch, "E5.0.20.34", {"position": v(270.86, 434.88) * mm});
            skPoint(sketch, "E5.0.20.35", {"position": v(270.86, 446.67) * mm});
            skPoint(sketch, "E5.0.20.36", {"position": v(270.86, 458.45) * mm});
            skPoint(sketch, "E5.0.20.37", {"position": v(270.86, 470.24) * mm});
            skPoint(sketch, "E5.0.20.38", {"position": v(270.86, 482.02) * mm});
            skPoint(sketch, "E5.0.20.39", {"position": v(270.86, 493.8) * mm});
            skPoint(sketch, "E5.0.20.40", {"position": v(270.86, 505.6) * mm});
            skPoint(sketch, "E5.0.20.41", {"position": v(270.86, 517.38) * mm});
            skPoint(sketch, "E5.0.20.42", {"position": v(270.86, 529.16) * mm});
            skPoint(sketch, "E5.0.20.43", {"position": v(270.86, 540.95) * mm});
            skPoint(sketch, "E5.0.20.44", {"position": v(270.86, 552.73) * mm});
            skPoint(sketch, "E5.0.20.45", {"position": v(270.86, 564.52) * mm});
            skPoint(sketch, "E5.0.20.46", {"position": v(270.86, 576.3) * mm});
            skPoint(sketch, "E5.0.20.47", {"position": v(270.86, 588.09) * mm});
            skPoint(sketch, "E5.0.21.0", {"position": v(282.64, 34.19) * mm});
            skPoint(sketch, "E5.0.21.1", {"position": v(282.64, 45.97) * mm});
            skPoint(sketch, "E5.0.21.2", {"position": v(282.64, 57.76) * mm});
            skPoint(sketch, "E5.0.21.3", {"position": v(282.64, 69.54) * mm});
            skPoint(sketch, "E5.0.21.4", {"position": v(282.64, 81.33) * mm});
            skPoint(sketch, "E5.0.21.5", {"position": v(282.64, 93.11) * mm});
            skPoint(sketch, "E5.0.21.6", {"position": v(282.64, 104.9) * mm});
            skPoint(sketch, "E5.0.21.7", {"position": v(282.64, 116.68) * mm});
            skPoint(sketch, "E5.0.21.8", {"position": v(282.64, 128.47) * mm});
            skPoint(sketch, "E5.0.21.9", {"position": v(282.64, 140.25) * mm});
            skPoint(sketch, "E5.0.21.10", {"position": v(282.64, 152.04) * mm});
            skPoint(sketch, "E5.0.21.11", {"position": v(282.64, 163.82) * mm});
            skPoint(sketch, "E5.0.21.12", {"position": v(282.64, 175.6) * mm});
            skPoint(sketch, "E5.0.21.13", {"position": v(282.64, 187.4) * mm});
            skPoint(sketch, "E5.0.21.14", {"position": v(282.64, 199.18) * mm});
            skPoint(sketch, "E5.0.21.15", {"position": v(282.64, 210.97) * mm});
            skPoint(sketch, "E5.0.21.16", {"position": v(282.64, 222.75) * mm});
            skPoint(sketch, "E5.0.21.17", {"position": v(282.64, 234.54) * mm});
            skPoint(sketch, "E5.0.21.18", {"position": v(282.64, 246.32) * mm});
            skPoint(sketch, "E5.0.21.19", {"position": v(282.64, 258.1) * mm});
            skPoint(sketch, "E5.0.21.20", {"position": v(282.64, 269.9) * mm});
            skPoint(sketch, "E5.0.21.21", {"position": v(282.64, 281.68) * mm});
            skPoint(sketch, "E5.0.21.22", {"position": v(282.64, 293.46) * mm});
            skPoint(sketch, "E5.0.21.23", {"position": v(282.64, 305.25) * mm});
            skPoint(sketch, "E5.0.21.24", {"position": v(282.64, 317.03) * mm});
            skPoint(sketch, "E5.0.21.25", {"position": v(282.64, 328.82) * mm});
            skPoint(sketch, "E5.0.21.26", {"position": v(282.64, 340.6) * mm});
            skPoint(sketch, "E5.0.21.27", {"position": v(282.64, 352.39) * mm});
            skPoint(sketch, "E5.0.21.28", {"position": v(282.64, 364.17) * mm});
            skPoint(sketch, "E5.0.21.29", {"position": v(282.64, 375.96) * mm});
            skPoint(sketch, "E5.0.21.30", {"position": v(282.64, 387.74) * mm});
            skPoint(sketch, "E5.0.21.31", {"position": v(282.64, 399.53) * mm});
            skPoint(sketch, "E5.0.21.32", {"position": v(282.64, 411.31) * mm});
            skPoint(sketch, "E5.0.21.33", {"position": v(282.64, 423.1) * mm});
            skPoint(sketch, "E5.0.21.34", {"position": v(282.64, 434.88) * mm});
            skPoint(sketch, "E5.0.21.35", {"position": v(282.64, 446.67) * mm});
            skPoint(sketch, "E5.0.21.36", {"position": v(282.64, 458.45) * mm});
            skPoint(sketch, "E5.0.21.37", {"position": v(282.64, 470.24) * mm});
            skPoint(sketch, "E5.0.21.38", {"position": v(282.64, 482.02) * mm});
            skPoint(sketch, "E5.0.21.39", {"position": v(282.64, 493.8) * mm});
            skPoint(sketch, "E5.0.21.40", {"position": v(282.64, 505.6) * mm});
            skPoint(sketch, "E5.0.21.41", {"position": v(282.64, 517.38) * mm});
            skPoint(sketch, "E5.0.21.42", {"position": v(282.64, 529.16) * mm});
            skPoint(sketch, "E5.0.21.43", {"position": v(282.64, 540.95) * mm});
            skPoint(sketch, "E5.0.21.44", {"position": v(282.64, 552.73) * mm});
            skPoint(sketch, "E5.0.21.45", {"position": v(282.64, 564.52) * mm});
            skPoint(sketch, "E5.0.21.46", {"position": v(282.64, 576.3) * mm});
            skPoint(sketch, "E5.0.21.47", {"position": v(282.64, 588.09) * mm});
            skPoint(sketch, "E5.0.22.0", {"position": v(294.43, 34.19) * mm});
            skPoint(sketch, "E5.0.22.1", {"position": v(294.43, 45.97) * mm});
            skPoint(sketch, "E5.0.22.2", {"position": v(294.43, 57.76) * mm});
            skPoint(sketch, "E5.0.22.3", {"position": v(294.43, 69.54) * mm});
            skPoint(sketch, "E5.0.22.4", {"position": v(294.43, 81.33) * mm});
            skPoint(sketch, "E5.0.22.5", {"position": v(294.43, 93.11) * mm});
            skPoint(sketch, "E5.0.22.6", {"position": v(294.43, 104.9) * mm});
            skPoint(sketch, "E5.0.22.7", {"position": v(294.43, 116.68) * mm});
            skPoint(sketch, "E5.0.22.8", {"position": v(294.43, 128.47) * mm});
            skPoint(sketch, "E5.0.22.9", {"position": v(294.43, 140.25) * mm});
            skPoint(sketch, "E5.0.22.10", {"position": v(294.43, 152.04) * mm});
            skPoint(sketch, "E5.0.22.11", {"position": v(294.43, 163.82) * mm});
            skPoint(sketch, "E5.0.22.12", {"position": v(294.43, 175.6) * mm});
            skPoint(sketch, "E5.0.22.13", {"position": v(294.43, 187.4) * mm});
            skPoint(sketch, "E5.0.22.14", {"position": v(294.43, 199.18) * mm});
            skPoint(sketch, "E5.0.22.15", {"position": v(294.43, 210.97) * mm});
            skPoint(sketch, "E5.0.22.16", {"position": v(294.43, 222.75) * mm});
            skPoint(sketch, "E5.0.22.17", {"position": v(294.43, 234.54) * mm});
            skPoint(sketch, "E5.0.22.18", {"position": v(294.43, 246.32) * mm});
            skPoint(sketch, "E5.0.22.19", {"position": v(294.43, 258.1) * mm});
            skPoint(sketch, "E5.0.22.20", {"position": v(294.43, 269.9) * mm});
            skPoint(sketch, "E5.0.22.21", {"position": v(294.43, 281.68) * mm});
            skPoint(sketch, "E5.0.22.22", {"position": v(294.43, 293.46) * mm});
            skPoint(sketch, "E5.0.22.23", {"position": v(294.43, 305.25) * mm});
            skPoint(sketch, "E5.0.22.24", {"position": v(294.43, 317.03) * mm});
            skPoint(sketch, "E5.0.22.25", {"position": v(294.43, 328.82) * mm});
            skPoint(sketch, "E5.0.22.26", {"position": v(294.43, 340.6) * mm});
            skPoint(sketch, "E5.0.22.27", {"position": v(294.43, 352.39) * mm});
            skPoint(sketch, "E5.0.22.28", {"position": v(294.43, 364.17) * mm});
            skPoint(sketch, "E5.0.22.29", {"position": v(294.43, 375.96) * mm});
            skPoint(sketch, "E5.0.22.30", {"position": v(294.43, 387.74) * mm});
            skPoint(sketch, "E5.0.22.31", {"position": v(294.43, 399.53) * mm});
            skPoint(sketch, "E5.0.22.32", {"position": v(294.43, 411.31) * mm});
            skPoint(sketch, "E5.0.22.33", {"position": v(294.43, 423.1) * mm});
            skPoint(sketch, "E5.0.22.34", {"position": v(294.43, 434.88) * mm});
            skPoint(sketch, "E5.0.22.35", {"position": v(294.43, 446.67) * mm});
            skPoint(sketch, "E5.0.22.36", {"position": v(294.43, 458.45) * mm});
            skPoint(sketch, "E5.0.22.37", {"position": v(294.43, 470.24) * mm});
            skPoint(sketch, "E5.0.22.38", {"position": v(294.43, 482.02) * mm});
            skPoint(sketch, "E5.0.22.39", {"position": v(294.43, 493.8) * mm});
            skPoint(sketch, "E5.0.22.40", {"position": v(294.43, 505.6) * mm});
            skPoint(sketch, "E5.0.22.41", {"position": v(294.43, 517.38) * mm});
            skPoint(sketch, "E5.0.22.42", {"position": v(294.43, 529.16) * mm});
            skPoint(sketch, "E5.0.22.43", {"position": v(294.43, 540.95) * mm});
            skPoint(sketch, "E5.0.22.44", {"position": v(294.43, 552.73) * mm});
            skPoint(sketch, "E5.0.22.45", {"position": v(294.43, 564.52) * mm});
            skPoint(sketch, "E5.0.22.46", {"position": v(294.43, 576.3) * mm});
            skPoint(sketch, "E5.0.22.47", {"position": v(294.43, 588.09) * mm});
            skPoint(sketch, "E5.0.23.0", {"position": v(306.21, 34.19) * mm});
            skPoint(sketch, "E5.0.23.1", {"position": v(306.21, 45.97) * mm});
            skPoint(sketch, "E5.0.23.2", {"position": v(306.21, 57.76) * mm});
            skPoint(sketch, "E5.0.23.3", {"position": v(306.21, 69.54) * mm});
            skPoint(sketch, "E5.0.23.4", {"position": v(306.21, 81.33) * mm});
            skPoint(sketch, "E5.0.23.5", {"position": v(306.21, 93.11) * mm});
            skPoint(sketch, "E5.0.23.6", {"position": v(306.21, 104.9) * mm});
            skPoint(sketch, "E5.0.23.7", {"position": v(306.21, 116.68) * mm});
            skPoint(sketch, "E5.0.23.8", {"position": v(306.21, 128.47) * mm});
            skPoint(sketch, "E5.0.23.9", {"position": v(306.21, 140.25) * mm});
            skPoint(sketch, "E5.0.23.10", {"position": v(306.21, 152.04) * mm});
            skPoint(sketch, "E5.0.23.11", {"position": v(306.21, 163.82) * mm});
            skPoint(sketch, "E5.0.23.12", {"position": v(306.21, 175.6) * mm});
            skPoint(sketch, "E5.0.23.13", {"position": v(306.21, 187.4) * mm});
            skPoint(sketch, "E5.0.23.14", {"position": v(306.21, 199.18) * mm});
            skPoint(sketch, "E5.0.23.15", {"position": v(306.21, 210.97) * mm});
            skPoint(sketch, "E5.0.23.16", {"position": v(306.21, 222.75) * mm});
            skPoint(sketch, "E5.0.23.17", {"position": v(306.21, 234.54) * mm});
            skPoint(sketch, "E5.0.23.18", {"position": v(306.21, 246.32) * mm});
            skPoint(sketch, "E5.0.23.19", {"position": v(306.21, 258.1) * mm});
            skPoint(sketch, "E5.0.23.20", {"position": v(306.21, 269.9) * mm});
            skPoint(sketch, "E5.0.23.21", {"position": v(306.21, 281.68) * mm});
            skPoint(sketch, "E5.0.23.22", {"position": v(306.21, 293.46) * mm});
            skPoint(sketch, "E5.0.23.23", {"position": v(306.21, 305.25) * mm});
            skPoint(sketch, "E5.0.23.24", {"position": v(306.21, 317.03) * mm});
            skPoint(sketch, "E5.0.23.25", {"position": v(306.21, 328.82) * mm});
            skPoint(sketch, "E5.0.23.26", {"position": v(306.21, 340.6) * mm});
            skPoint(sketch, "E5.0.23.27", {"position": v(306.21, 352.39) * mm});
            skPoint(sketch, "E5.0.23.28", {"position": v(306.21, 364.17) * mm});
            skPoint(sketch, "E5.0.23.29", {"position": v(306.21, 375.96) * mm});
            skPoint(sketch, "E5.0.23.30", {"position": v(306.21, 387.74) * mm});
            skPoint(sketch, "E5.0.23.31", {"position": v(306.21, 399.53) * mm});
            skPoint(sketch, "E5.0.23.32", {"position": v(306.21, 411.31) * mm});
            skPoint(sketch, "E5.0.23.33", {"position": v(306.21, 423.1) * mm});
            skPoint(sketch, "E5.0.23.34", {"position": v(306.21, 434.88) * mm});
            skPoint(sketch, "E5.0.23.35", {"position": v(306.21, 446.67) * mm});
            skPoint(sketch, "E5.0.23.36", {"position": v(306.21, 458.45) * mm});
            skPoint(sketch, "E5.0.23.37", {"position": v(306.21, 470.24) * mm});
            skPoint(sketch, "E5.0.23.38", {"position": v(306.21, 482.02) * mm});
            skPoint(sketch, "E5.0.23.39", {"position": v(306.21, 493.8) * mm});
            skPoint(sketch, "E5.0.23.40", {"position": v(306.21, 505.6) * mm});
            skPoint(sketch, "E5.0.23.41", {"position": v(306.21, 517.38) * mm});
            skPoint(sketch, "E5.0.23.42", {"position": v(306.21, 529.16) * mm});
            skPoint(sketch, "E5.0.23.43", {"position": v(306.21, 540.95) * mm});
            skPoint(sketch, "E5.0.23.44", {"position": v(306.21, 552.73) * mm});
            skPoint(sketch, "E5.0.23.45", {"position": v(306.21, 564.52) * mm});
            skPoint(sketch, "E5.0.23.46", {"position": v(306.21, 576.3) * mm});
            skPoint(sketch, "E5.0.23.47", {"position": v(306.21, 588.09) * mm});
            skPoint(sketch, "E5.0.24.0", {"position": v(318, 34.19) * mm});
            skPoint(sketch, "E5.0.24.1", {"position": v(318, 45.97) * mm});
            skPoint(sketch, "E5.0.24.2", {"position": v(318, 57.76) * mm});
            skPoint(sketch, "E5.0.24.3", {"position": v(318, 69.54) * mm});
            skPoint(sketch, "E5.0.24.4", {"position": v(318, 81.33) * mm});
            skPoint(sketch, "E5.0.24.5", {"position": v(318, 93.11) * mm});
            skPoint(sketch, "E5.0.24.6", {"position": v(318, 104.9) * mm});
            skPoint(sketch, "E5.0.24.7", {"position": v(318, 116.68) * mm});
            skPoint(sketch, "E5.0.24.8", {"position": v(318, 128.47) * mm});
            skPoint(sketch, "E5.0.24.9", {"position": v(318, 140.25) * mm});
            skPoint(sketch, "E5.0.24.10", {"position": v(318, 152.04) * mm});
            skPoint(sketch, "E5.0.24.11", {"position": v(318, 163.82) * mm});
            skPoint(sketch, "E5.0.24.12", {"position": v(318, 175.6) * mm});
            skPoint(sketch, "E5.0.24.13", {"position": v(318, 187.4) * mm});
            skPoint(sketch, "E5.0.24.14", {"position": v(318, 199.18) * mm});
            skPoint(sketch, "E5.0.24.15", {"position": v(318, 210.97) * mm});
            skPoint(sketch, "E5.0.24.16", {"position": v(318, 222.75) * mm});
            skPoint(sketch, "E5.0.24.17", {"position": v(318, 234.54) * mm});
            skPoint(sketch, "E5.0.24.18", {"position": v(318, 246.32) * mm});
            skPoint(sketch, "E5.0.24.19", {"position": v(318, 258.1) * mm});
            skPoint(sketch, "E5.0.24.20", {"position": v(318, 269.9) * mm});
            skPoint(sketch, "E5.0.24.21", {"position": v(318, 281.68) * mm});
            skPoint(sketch, "E5.0.24.22", {"position": v(318, 293.46) * mm});
            skPoint(sketch, "E5.0.24.23", {"position": v(318, 305.25) * mm});
            skPoint(sketch, "E5.0.24.24", {"position": v(318, 317.03) * mm});
            skPoint(sketch, "E5.0.24.25", {"position": v(318, 328.82) * mm});
            skPoint(sketch, "E5.0.24.26", {"position": v(318, 340.6) * mm});
            skPoint(sketch, "E5.0.24.27", {"position": v(318, 352.39) * mm});
            skPoint(sketch, "E5.0.24.28", {"position": v(318, 364.17) * mm});
            skPoint(sketch, "E5.0.24.29", {"position": v(318, 375.96) * mm});
            skPoint(sketch, "E5.0.24.30", {"position": v(318, 387.74) * mm});
            skPoint(sketch, "E5.0.24.31", {"position": v(318, 399.53) * mm});
            skPoint(sketch, "E5.0.24.32", {"position": v(318, 411.31) * mm});
            skPoint(sketch, "E5.0.24.33", {"position": v(318, 423.1) * mm});
            skPoint(sketch, "E5.0.24.34", {"position": v(318, 434.88) * mm});
            skPoint(sketch, "E5.0.24.35", {"position": v(318, 446.67) * mm});
            skPoint(sketch, "E5.0.24.36", {"position": v(318, 458.45) * mm});
            skPoint(sketch, "E5.0.24.37", {"position": v(318, 470.24) * mm});
            skPoint(sketch, "E5.0.24.38", {"position": v(318, 482.02) * mm});
            skPoint(sketch, "E5.0.24.39", {"position": v(318, 493.8) * mm});
            skPoint(sketch, "E5.0.24.40", {"position": v(318, 505.6) * mm});
            skPoint(sketch, "E5.0.24.41", {"position": v(318, 517.38) * mm});
            skPoint(sketch, "E5.0.24.42", {"position": v(318, 529.16) * mm});
            skPoint(sketch, "E5.0.24.43", {"position": v(318, 540.95) * mm});
            skPoint(sketch, "E5.0.24.44", {"position": v(318, 552.73) * mm});
            skPoint(sketch, "E5.0.24.45", {"position": v(318, 564.52) * mm});
            skPoint(sketch, "E5.0.24.46", {"position": v(318, 576.3) * mm});
            skPoint(sketch, "E5.0.24.47", {"position": v(318, 588.09) * mm});
            skPoint(sketch, "E5.0.25.0", {"position": v(329.78, 34.19) * mm});
            skPoint(sketch, "E5.0.25.1", {"position": v(329.78, 45.97) * mm});
            skPoint(sketch, "E5.0.25.2", {"position": v(329.78, 57.76) * mm});
            skPoint(sketch, "E5.0.25.3", {"position": v(329.78, 69.54) * mm});
            skPoint(sketch, "E5.0.25.4", {"position": v(329.78, 81.33) * mm});
            skPoint(sketch, "E5.0.25.5", {"position": v(329.78, 93.11) * mm});
            skPoint(sketch, "E5.0.25.6", {"position": v(329.78, 104.9) * mm});
            skPoint(sketch, "E5.0.25.7", {"position": v(329.78, 116.68) * mm});
            skPoint(sketch, "E5.0.25.8", {"position": v(329.78, 128.47) * mm});
            skPoint(sketch, "E5.0.25.9", {"position": v(329.78, 140.25) * mm});
            skPoint(sketch, "E5.0.25.10", {"position": v(329.78, 152.04) * mm});
            skPoint(sketch, "E5.0.25.11", {"position": v(329.78, 163.82) * mm});
            skPoint(sketch, "E5.0.25.12", {"position": v(329.78, 175.6) * mm});
            skPoint(sketch, "E5.0.25.13", {"position": v(329.78, 187.4) * mm});
            skPoint(sketch, "E5.0.25.14", {"position": v(329.78, 199.18) * mm});
            skPoint(sketch, "E5.0.25.15", {"position": v(329.78, 210.97) * mm});
            skPoint(sketch, "E5.0.25.16", {"position": v(329.78, 222.75) * mm});
            skPoint(sketch, "E5.0.25.17", {"position": v(329.78, 234.54) * mm});
            skPoint(sketch, "E5.0.25.18", {"position": v(329.78, 246.32) * mm});
            skPoint(sketch, "E5.0.25.19", {"position": v(329.78, 258.1) * mm});
            skPoint(sketch, "E5.0.25.20", {"position": v(329.78, 269.9) * mm});
            skPoint(sketch, "E5.0.25.21", {"position": v(329.78, 281.68) * mm});
            skPoint(sketch, "E5.0.25.22", {"position": v(329.78, 293.46) * mm});
            skPoint(sketch, "E5.0.25.23", {"position": v(329.78, 305.25) * mm});
            skPoint(sketch, "E5.0.25.24", {"position": v(329.78, 317.03) * mm});
            skPoint(sketch, "E5.0.25.25", {"position": v(329.78, 328.82) * mm});
            skPoint(sketch, "E5.0.25.26", {"position": v(329.78, 340.6) * mm});
            skPoint(sketch, "E5.0.25.27", {"position": v(329.78, 352.39) * mm});
            skPoint(sketch, "E5.0.25.28", {"position": v(329.78, 364.17) * mm});
            skPoint(sketch, "E5.0.25.29", {"position": v(329.78, 375.96) * mm});
            skPoint(sketch, "E5.0.25.30", {"position": v(329.78, 387.74) * mm});
            skPoint(sketch, "E5.0.25.31", {"position": v(329.78, 399.53) * mm});
            skPoint(sketch, "E5.0.25.32", {"position": v(329.78, 411.31) * mm});
            skPoint(sketch, "E5.0.25.33", {"position": v(329.78, 423.1) * mm});
            skPoint(sketch, "E5.0.25.34", {"position": v(329.78, 434.88) * mm});
            skPoint(sketch, "E5.0.25.35", {"position": v(329.78, 446.67) * mm});
            skPoint(sketch, "E5.0.25.36", {"position": v(329.78, 458.45) * mm});
            skPoint(sketch, "E5.0.25.37", {"position": v(329.78, 470.24) * mm});
            skPoint(sketch, "E5.0.25.38", {"position": v(329.78, 482.02) * mm});
            skPoint(sketch, "E5.0.25.39", {"position": v(329.78, 493.8) * mm});
            skPoint(sketch, "E5.0.25.40", {"position": v(329.78, 505.6) * mm});
            skPoint(sketch, "E5.0.25.41", {"position": v(329.78, 517.38) * mm});
            skPoint(sketch, "E5.0.25.42", {"position": v(329.78, 529.16) * mm});
            skPoint(sketch, "E5.0.25.43", {"position": v(329.78, 540.95) * mm});
            skPoint(sketch, "E5.0.25.44", {"position": v(329.78, 552.73) * mm});
            skPoint(sketch, "E5.0.25.45", {"position": v(329.78, 564.52) * mm});
            skPoint(sketch, "E5.0.25.46", {"position": v(329.78, 576.3) * mm});
            skPoint(sketch, "E5.0.25.47", {"position": v(329.78, 588.09) * mm});
            skPoint(sketch, "E5.0.26.0", {"position": v(341.57, 34.19) * mm});
            skPoint(sketch, "E5.0.26.1", {"position": v(341.57, 45.97) * mm});
            skPoint(sketch, "E5.0.26.2", {"position": v(341.57, 57.76) * mm});
            skPoint(sketch, "E5.0.26.3", {"position": v(341.57, 69.54) * mm});
            skPoint(sketch, "E5.0.26.4", {"position": v(341.57, 81.33) * mm});
            skPoint(sketch, "E5.0.26.5", {"position": v(341.57, 93.11) * mm});
            skPoint(sketch, "E5.0.26.6", {"position": v(341.57, 104.9) * mm});
            skPoint(sketch, "E5.0.26.7", {"position": v(341.57, 116.68) * mm});
            skPoint(sketch, "E5.0.26.8", {"position": v(341.57, 128.47) * mm});
            skPoint(sketch, "E5.0.26.9", {"position": v(341.57, 140.25) * mm});
            skPoint(sketch, "E5.0.26.10", {"position": v(341.57, 152.04) * mm});
            skPoint(sketch, "E5.0.26.11", {"position": v(341.57, 163.82) * mm});
            skPoint(sketch, "E5.0.26.12", {"position": v(341.57, 175.6) * mm});
            skPoint(sketch, "E5.0.26.13", {"position": v(341.57, 187.4) * mm});
            skPoint(sketch, "E5.0.26.14", {"position": v(341.57, 199.18) * mm});
            skPoint(sketch, "E5.0.26.15", {"position": v(341.57, 210.97) * mm});
            skPoint(sketch, "E5.0.26.16", {"position": v(341.57, 222.75) * mm});
            skPoint(sketch, "E5.0.26.17", {"position": v(341.57, 234.54) * mm});
            skPoint(sketch, "E5.0.26.18", {"position": v(341.57, 246.32) * mm});
            skPoint(sketch, "E5.0.26.19", {"position": v(341.57, 258.1) * mm});
            skPoint(sketch, "E5.0.26.20", {"position": v(341.57, 269.9) * mm});
            skPoint(sketch, "E5.0.26.21", {"position": v(341.57, 281.68) * mm});
            skPoint(sketch, "E5.0.26.22", {"position": v(341.57, 293.46) * mm});
            skPoint(sketch, "E5.0.26.23", {"position": v(341.57, 305.25) * mm});
            skPoint(sketch, "E5.0.26.24", {"position": v(341.57, 317.03) * mm});
            skPoint(sketch, "E5.0.26.25", {"position": v(341.57, 328.82) * mm});
            skPoint(sketch, "E5.0.26.26", {"position": v(341.57, 340.6) * mm});
            skPoint(sketch, "E5.0.26.27", {"position": v(341.57, 352.39) * mm});
            skPoint(sketch, "E5.0.26.28", {"position": v(341.57, 364.17) * mm});
            skPoint(sketch, "E5.0.26.29", {"position": v(341.57, 375.96) * mm});
            skPoint(sketch, "E5.0.26.30", {"position": v(341.57, 387.74) * mm});
            skPoint(sketch, "E5.0.26.31", {"position": v(341.57, 399.53) * mm});
            skPoint(sketch, "E5.0.26.32", {"position": v(341.57, 411.31) * mm});
            skPoint(sketch, "E5.0.26.33", {"position": v(341.57, 423.1) * mm});
            skPoint(sketch, "E5.0.26.34", {"position": v(341.57, 434.88) * mm});
            skPoint(sketch, "E5.0.26.35", {"position": v(341.57, 446.67) * mm});
            skPoint(sketch, "E5.0.26.36", {"position": v(341.57, 458.45) * mm});
            skPoint(sketch, "E5.0.26.37", {"position": v(341.57, 470.24) * mm});
            skPoint(sketch, "E5.0.26.38", {"position": v(341.57, 482.02) * mm});
            skPoint(sketch, "E5.0.26.39", {"position": v(341.57, 493.8) * mm});
            skPoint(sketch, "E5.0.26.40", {"position": v(341.57, 505.6) * mm});
            skPoint(sketch, "E5.0.26.41", {"position": v(341.57, 517.38) * mm});
            skPoint(sketch, "E5.0.26.42", {"position": v(341.57, 529.16) * mm});
            skPoint(sketch, "E5.0.26.43", {"position": v(341.57, 540.95) * mm});
            skPoint(sketch, "E5.0.26.44", {"position": v(341.57, 552.73) * mm});
            skPoint(sketch, "E5.0.26.45", {"position": v(341.57, 564.52) * mm});
            skPoint(sketch, "E5.0.26.46", {"position": v(341.57, 576.3) * mm});
            skPoint(sketch, "E5.0.26.47", {"position": v(341.57, 588.09) * mm});
            skPoint(sketch, "E5.0.27.0", {"position": v(353.35, 34.19) * mm});
            skPoint(sketch, "E5.0.27.1", {"position": v(353.35, 45.97) * mm});
            skPoint(sketch, "E5.0.27.2", {"position": v(353.35, 57.76) * mm});
            skPoint(sketch, "E5.0.27.3", {"position": v(353.35, 69.54) * mm});
            skPoint(sketch, "E5.0.27.4", {"position": v(353.35, 81.33) * mm});
            skPoint(sketch, "E5.0.27.5", {"position": v(353.35, 93.11) * mm});
            skPoint(sketch, "E5.0.27.6", {"position": v(353.35, 104.9) * mm});
            skPoint(sketch, "E5.0.27.7", {"position": v(353.35, 116.68) * mm});
            skPoint(sketch, "E5.0.27.8", {"position": v(353.35, 128.47) * mm});
            skPoint(sketch, "E5.0.27.9", {"position": v(353.35, 140.25) * mm});
            skPoint(sketch, "E5.0.27.10", {"position": v(353.35, 152.04) * mm});
            skPoint(sketch, "E5.0.27.11", {"position": v(353.35, 163.82) * mm});
            skPoint(sketch, "E5.0.27.12", {"position": v(353.35, 175.6) * mm});
            skPoint(sketch, "E5.0.27.13", {"position": v(353.35, 187.4) * mm});
            skPoint(sketch, "E5.0.27.14", {"position": v(353.35, 199.18) * mm});
            skPoint(sketch, "E5.0.27.15", {"position": v(353.35, 210.97) * mm});
            skPoint(sketch, "E5.0.27.16", {"position": v(353.35, 222.75) * mm});
            skPoint(sketch, "E5.0.27.17", {"position": v(353.35, 234.54) * mm});
            skPoint(sketch, "E5.0.27.18", {"position": v(353.35, 246.32) * mm});
            skPoint(sketch, "E5.0.27.19", {"position": v(353.35, 258.1) * mm});
            skPoint(sketch, "E5.0.27.20", {"position": v(353.35, 269.9) * mm});
            skPoint(sketch, "E5.0.27.21", {"position": v(353.35, 281.68) * mm});
            skPoint(sketch, "E5.0.27.22", {"position": v(353.35, 293.46) * mm});
            skPoint(sketch, "E5.0.27.23", {"position": v(353.35, 305.25) * mm});
            skPoint(sketch, "E5.0.27.24", {"position": v(353.35, 317.03) * mm});
            skPoint(sketch, "E5.0.27.25", {"position": v(353.35, 328.82) * mm});
            skPoint(sketch, "E5.0.27.26", {"position": v(353.35, 340.6) * mm});
            skPoint(sketch, "E5.0.27.27", {"position": v(353.35, 352.39) * mm});
            skPoint(sketch, "E5.0.27.28", {"position": v(353.35, 364.17) * mm});
            skPoint(sketch, "E5.0.27.29", {"position": v(353.35, 375.96) * mm});
            skPoint(sketch, "E5.0.27.30", {"position": v(353.35, 387.74) * mm});
            skPoint(sketch, "E5.0.27.31", {"position": v(353.35, 399.53) * mm});
            skPoint(sketch, "E5.0.27.32", {"position": v(353.35, 411.31) * mm});
            skPoint(sketch, "E5.0.27.33", {"position": v(353.35, 423.1) * mm});
            skPoint(sketch, "E5.0.27.34", {"position": v(353.35, 434.88) * mm});
            skPoint(sketch, "E5.0.27.35", {"position": v(353.35, 446.67) * mm});
            skPoint(sketch, "E5.0.27.36", {"position": v(353.35, 458.45) * mm});
            skPoint(sketch, "E5.0.27.37", {"position": v(353.35, 470.24) * mm});
            skPoint(sketch, "E5.0.27.38", {"position": v(353.35, 482.02) * mm});
            skPoint(sketch, "E5.0.27.39", {"position": v(353.35, 493.8) * mm});
            skPoint(sketch, "E5.0.27.40", {"position": v(353.35, 505.6) * mm});
            skPoint(sketch, "E5.0.27.41", {"position": v(353.35, 517.38) * mm});
            skPoint(sketch, "E5.0.27.42", {"position": v(353.35, 529.16) * mm});
            skPoint(sketch, "E5.0.27.43", {"position": v(353.35, 540.95) * mm});
            skPoint(sketch, "E5.0.27.44", {"position": v(353.35, 552.73) * mm});
            skPoint(sketch, "E5.0.27.45", {"position": v(353.35, 564.52) * mm});
            skPoint(sketch, "E5.0.27.46", {"position": v(353.35, 576.3) * mm});
            skPoint(sketch, "E5.0.27.47", {"position": v(353.35, 588.09) * mm});
            skPoint(sketch, "E5.0.28.0", {"position": v(365.14, 34.19) * mm});
            skPoint(sketch, "E5.0.28.1", {"position": v(365.14, 45.97) * mm});
            skPoint(sketch, "E5.0.28.2", {"position": v(365.14, 57.76) * mm});
            skPoint(sketch, "E5.0.28.3", {"position": v(365.14, 69.54) * mm});
            skPoint(sketch, "E5.0.28.4", {"position": v(365.14, 81.33) * mm});
            skPoint(sketch, "E5.0.28.5", {"position": v(365.14, 93.11) * mm});
            skPoint(sketch, "E5.0.28.6", {"position": v(365.14, 104.9) * mm});
            skPoint(sketch, "E5.0.28.7", {"position": v(365.14, 116.68) * mm});
            skPoint(sketch, "E5.0.28.8", {"position": v(365.14, 128.47) * mm});
            skPoint(sketch, "E5.0.28.9", {"position": v(365.14, 140.25) * mm});
            skPoint(sketch, "E5.0.28.10", {"position": v(365.14, 152.04) * mm});
            skPoint(sketch, "E5.0.28.11", {"position": v(365.14, 163.82) * mm});
            skPoint(sketch, "E5.0.28.12", {"position": v(365.14, 175.6) * mm});
            skPoint(sketch, "E5.0.28.13", {"position": v(365.14, 187.4) * mm});
            skPoint(sketch, "E5.0.28.14", {"position": v(365.14, 199.18) * mm});
            skPoint(sketch, "E5.0.28.15", {"position": v(365.14, 210.97) * mm});
            skPoint(sketch, "E5.0.28.16", {"position": v(365.14, 222.75) * mm});
            skPoint(sketch, "E5.0.28.17", {"position": v(365.14, 234.54) * mm});
            skPoint(sketch, "E5.0.28.18", {"position": v(365.14, 246.32) * mm});
            skPoint(sketch, "E5.0.28.19", {"position": v(365.14, 258.1) * mm});
            skPoint(sketch, "E5.0.28.20", {"position": v(365.14, 269.9) * mm});
            skPoint(sketch, "E5.0.28.21", {"position": v(365.14, 281.68) * mm});
            skPoint(sketch, "E5.0.28.22", {"position": v(365.14, 293.46) * mm});
            skPoint(sketch, "E5.0.28.23", {"position": v(365.14, 305.25) * mm});
            skPoint(sketch, "E5.0.28.24", {"position": v(365.14, 317.03) * mm});
            skPoint(sketch, "E5.0.28.25", {"position": v(365.14, 328.82) * mm});
            skPoint(sketch, "E5.0.28.26", {"position": v(365.14, 340.6) * mm});
            skPoint(sketch, "E5.0.28.27", {"position": v(365.14, 352.39) * mm});
            skPoint(sketch, "E5.0.28.28", {"position": v(365.14, 364.17) * mm});
            skPoint(sketch, "E5.0.28.29", {"position": v(365.14, 375.96) * mm});
            skPoint(sketch, "E5.0.28.30", {"position": v(365.14, 387.74) * mm});
            skPoint(sketch, "E5.0.28.31", {"position": v(365.14, 399.53) * mm});
            skPoint(sketch, "E5.0.28.32", {"position": v(365.14, 411.31) * mm});
            skPoint(sketch, "E5.0.28.33", {"position": v(365.14, 423.1) * mm});
            skPoint(sketch, "E5.0.28.34", {"position": v(365.14, 434.88) * mm});
            skPoint(sketch, "E5.0.28.35", {"position": v(365.14, 446.67) * mm});
            skPoint(sketch, "E5.0.28.36", {"position": v(365.14, 458.45) * mm});
            skPoint(sketch, "E5.0.28.37", {"position": v(365.14, 470.24) * mm});
            skPoint(sketch, "E5.0.28.38", {"position": v(365.14, 482.02) * mm});
            skPoint(sketch, "E5.0.28.39", {"position": v(365.14, 493.8) * mm});
            skPoint(sketch, "E5.0.28.40", {"position": v(365.14, 505.6) * mm});
            skPoint(sketch, "E5.0.28.41", {"position": v(365.14, 517.38) * mm});
            skPoint(sketch, "E5.0.28.42", {"position": v(365.14, 529.16) * mm});
            skPoint(sketch, "E5.0.28.43", {"position": v(365.14, 540.95) * mm});
            skPoint(sketch, "E5.0.28.44", {"position": v(365.14, 552.73) * mm});
            skPoint(sketch, "E5.0.28.45", {"position": v(365.14, 564.52) * mm});
            skPoint(sketch, "E5.0.28.46", {"position": v(365.14, 576.3) * mm});
            skPoint(sketch, "E5.0.28.47", {"position": v(365.14, 588.09) * mm});
            skPoint(sketch, "E5.0.29.0", {"position": v(376.92, 34.19) * mm});
            skPoint(sketch, "E5.0.29.1", {"position": v(376.92, 45.97) * mm});
            skPoint(sketch, "E5.0.29.2", {"position": v(376.92, 57.76) * mm});
            skPoint(sketch, "E5.0.29.3", {"position": v(376.92, 69.54) * mm});
            skPoint(sketch, "E5.0.29.4", {"position": v(376.92, 81.33) * mm});
            skPoint(sketch, "E5.0.29.5", {"position": v(376.92, 93.11) * mm});
            skPoint(sketch, "E5.0.29.6", {"position": v(376.92, 104.9) * mm});
            skPoint(sketch, "E5.0.29.7", {"position": v(376.92, 116.68) * mm});
            skPoint(sketch, "E5.0.29.8", {"position": v(376.92, 128.47) * mm});
            skPoint(sketch, "E5.0.29.9", {"position": v(376.92, 140.25) * mm});
            skPoint(sketch, "E5.0.29.10", {"position": v(376.92, 152.04) * mm});
            skPoint(sketch, "E5.0.29.11", {"position": v(376.92, 163.82) * mm});
            skPoint(sketch, "E5.0.29.12", {"position": v(376.92, 175.6) * mm});
            skPoint(sketch, "E5.0.29.13", {"position": v(376.92, 187.4) * mm});
            skPoint(sketch, "E5.0.29.14", {"position": v(376.92, 199.18) * mm});
            skPoint(sketch, "E5.0.29.15", {"position": v(376.92, 210.97) * mm});
            skPoint(sketch, "E5.0.29.16", {"position": v(376.92, 222.75) * mm});
            skPoint(sketch, "E5.0.29.17", {"position": v(376.92, 234.54) * mm});
            skPoint(sketch, "E5.0.29.18", {"position": v(376.92, 246.32) * mm});
            skPoint(sketch, "E5.0.29.19", {"position": v(376.92, 258.1) * mm});
            skPoint(sketch, "E5.0.29.20", {"position": v(376.92, 269.9) * mm});
            skPoint(sketch, "E5.0.29.21", {"position": v(376.92, 281.68) * mm});
            skPoint(sketch, "E5.0.29.22", {"position": v(376.92, 293.46) * mm});
            skPoint(sketch, "E5.0.29.23", {"position": v(376.92, 305.25) * mm});
            skPoint(sketch, "E5.0.29.24", {"position": v(376.92, 317.03) * mm});
            skPoint(sketch, "E5.0.29.25", {"position": v(376.92, 328.82) * mm});
            skPoint(sketch, "E5.0.29.26", {"position": v(376.92, 340.6) * mm});
            skPoint(sketch, "E5.0.29.27", {"position": v(376.92, 352.39) * mm});
            skPoint(sketch, "E5.0.29.28", {"position": v(376.92, 364.17) * mm});
            skPoint(sketch, "E5.0.29.29", {"position": v(376.92, 375.96) * mm});
            skPoint(sketch, "E5.0.29.30", {"position": v(376.92, 387.74) * mm});
            skPoint(sketch, "E5.0.29.31", {"position": v(376.92, 399.53) * mm});
            skPoint(sketch, "E5.0.29.32", {"position": v(376.92, 411.31) * mm});
            skPoint(sketch, "E5.0.29.33", {"position": v(376.92, 423.1) * mm});
            skPoint(sketch, "E5.0.29.34", {"position": v(376.92, 434.88) * mm});
            skPoint(sketch, "E5.0.29.35", {"position": v(376.92, 446.67) * mm});
            skPoint(sketch, "E5.0.29.36", {"position": v(376.92, 458.45) * mm});
            skPoint(sketch, "E5.0.29.37", {"position": v(376.92, 470.24) * mm});
            skPoint(sketch, "E5.0.29.38", {"position": v(376.92, 482.02) * mm});
            skPoint(sketch, "E5.0.29.39", {"position": v(376.92, 493.8) * mm});
            skPoint(sketch, "E5.0.29.40", {"position": v(376.92, 505.6) * mm});
            skPoint(sketch, "E5.0.29.41", {"position": v(376.92, 517.38) * mm});
            skPoint(sketch, "E5.0.29.42", {"position": v(376.92, 529.16) * mm});
            skPoint(sketch, "E5.0.29.43", {"position": v(376.92, 540.95) * mm});
            skPoint(sketch, "E5.0.29.44", {"position": v(376.92, 552.73) * mm});
            skPoint(sketch, "E5.0.29.45", {"position": v(376.92, 564.52) * mm});
            skPoint(sketch, "E5.0.29.46", {"position": v(376.92, 576.3) * mm});
            skPoint(sketch, "E5.0.29.47", {"position": v(376.92, 588.09) * mm});
            skPoint(sketch, "E5.0.30.0", {"position": v(388.7, 34.19) * mm});
            skPoint(sketch, "E5.0.30.1", {"position": v(388.7, 45.97) * mm});
            skPoint(sketch, "E5.0.30.2", {"position": v(388.7, 57.76) * mm});
            skPoint(sketch, "E5.0.30.3", {"position": v(388.7, 69.54) * mm});
            skPoint(sketch, "E5.0.30.4", {"position": v(388.7, 81.33) * mm});
            skPoint(sketch, "E5.0.30.5", {"position": v(388.7, 93.11) * mm});
            skPoint(sketch, "E5.0.30.6", {"position": v(388.7, 104.9) * mm});
            skPoint(sketch, "E5.0.30.7", {"position": v(388.7, 116.68) * mm});
            skPoint(sketch, "E5.0.30.8", {"position": v(388.7, 128.47) * mm});
            skPoint(sketch, "E5.0.30.9", {"position": v(388.7, 140.25) * mm});
            skPoint(sketch, "E5.0.30.10", {"position": v(388.7, 152.04) * mm});
            skPoint(sketch, "E5.0.30.11", {"position": v(388.7, 163.82) * mm});
            skPoint(sketch, "E5.0.30.12", {"position": v(388.7, 175.6) * mm});
            skPoint(sketch, "E5.0.30.13", {"position": v(388.7, 187.4) * mm});
            skPoint(sketch, "E5.0.30.14", {"position": v(388.7, 199.18) * mm});
            skPoint(sketch, "E5.0.30.15", {"position": v(388.7, 210.97) * mm});
            skPoint(sketch, "E5.0.30.16", {"position": v(388.7, 222.75) * mm});
            skPoint(sketch, "E5.0.30.17", {"position": v(388.7, 234.54) * mm});
            skPoint(sketch, "E5.0.30.18", {"position": v(388.7, 246.32) * mm});
            skPoint(sketch, "E5.0.30.19", {"position": v(388.7, 258.1) * mm});
            skPoint(sketch, "E5.0.30.20", {"position": v(388.7, 269.9) * mm});
            skPoint(sketch, "E5.0.30.21", {"position": v(388.7, 281.68) * mm});
            skPoint(sketch, "E5.0.30.22", {"position": v(388.7, 293.46) * mm});
            skPoint(sketch, "E5.0.30.23", {"position": v(388.7, 305.25) * mm});
            skPoint(sketch, "E5.0.30.24", {"position": v(388.7, 317.03) * mm});
            skPoint(sketch, "E5.0.30.25", {"position": v(388.7, 328.82) * mm});
            skPoint(sketch, "E5.0.30.26", {"position": v(388.7, 340.6) * mm});
            skPoint(sketch, "E5.0.30.27", {"position": v(388.7, 352.39) * mm});
            skPoint(sketch, "E5.0.30.28", {"position": v(388.7, 364.17) * mm});
            skPoint(sketch, "E5.0.30.29", {"position": v(388.7, 375.96) * mm});
            skPoint(sketch, "E5.0.30.30", {"position": v(388.7, 387.74) * mm});
            skPoint(sketch, "E5.0.30.31", {"position": v(388.7, 399.53) * mm});
            skPoint(sketch, "E5.0.30.32", {"position": v(388.7, 411.31) * mm});
            skPoint(sketch, "E5.0.30.33", {"position": v(388.7, 423.1) * mm});
            skPoint(sketch, "E5.0.30.34", {"position": v(388.7, 434.88) * mm});
            skPoint(sketch, "E5.0.30.35", {"position": v(388.7, 446.67) * mm});
            skPoint(sketch, "E5.0.30.36", {"position": v(388.7, 458.45) * mm});
            skPoint(sketch, "E5.0.30.37", {"position": v(388.7, 470.24) * mm});
            skPoint(sketch, "E5.0.30.38", {"position": v(388.7, 482.02) * mm});
            skPoint(sketch, "E5.0.30.39", {"position": v(388.7, 493.8) * mm});
            skPoint(sketch, "E5.0.30.40", {"position": v(388.7, 505.6) * mm});
            skPoint(sketch, "E5.0.30.41", {"position": v(388.7, 517.38) * mm});
            skPoint(sketch, "E5.0.30.42", {"position": v(388.7, 529.16) * mm});
            skPoint(sketch, "E5.0.30.43", {"position": v(388.7, 540.95) * mm});
            skPoint(sketch, "E5.0.30.44", {"position": v(388.7, 552.73) * mm});
            skPoint(sketch, "E5.0.30.45", {"position": v(388.7, 564.52) * mm});
            skPoint(sketch, "E5.0.30.46", {"position": v(388.7, 576.3) * mm});
            skPoint(sketch, "E5.0.30.47", {"position": v(388.7, 588.09) * mm});
            skPoint(sketch, "E5.0.31.0", {"position": v(400.5, 34.19) * mm});
            skPoint(sketch, "E5.0.31.1", {"position": v(400.5, 45.97) * mm});
            skPoint(sketch, "E5.0.31.2", {"position": v(400.5, 57.76) * mm});
            skPoint(sketch, "E5.0.31.3", {"position": v(400.5, 69.54) * mm});
            skPoint(sketch, "E5.0.31.4", {"position": v(400.5, 81.33) * mm});
            skPoint(sketch, "E5.0.31.5", {"position": v(400.5, 93.11) * mm});
            skPoint(sketch, "E5.0.31.6", {"position": v(400.5, 104.9) * mm});
            skPoint(sketch, "E5.0.31.7", {"position": v(400.5, 116.68) * mm});
            skPoint(sketch, "E5.0.31.8", {"position": v(400.5, 128.47) * mm});
            skPoint(sketch, "E5.0.31.9", {"position": v(400.5, 140.25) * mm});
            skPoint(sketch, "E5.0.31.10", {"position": v(400.5, 152.04) * mm});
            skPoint(sketch, "E5.0.31.11", {"position": v(400.5, 163.82) * mm});
            skPoint(sketch, "E5.0.31.12", {"position": v(400.5, 175.6) * mm});
            skPoint(sketch, "E5.0.31.13", {"position": v(400.5, 187.4) * mm});
            skPoint(sketch, "E5.0.31.14", {"position": v(400.5, 199.18) * mm});
            skPoint(sketch, "E5.0.31.15", {"position": v(400.5, 210.97) * mm});
            skPoint(sketch, "E5.0.31.16", {"position": v(400.5, 222.75) * mm});
            skPoint(sketch, "E5.0.31.17", {"position": v(400.5, 234.54) * mm});
            skPoint(sketch, "E5.0.31.18", {"position": v(400.5, 246.32) * mm});
            skPoint(sketch, "E5.0.31.19", {"position": v(400.5, 258.1) * mm});
            skPoint(sketch, "E5.0.31.20", {"position": v(400.5, 269.9) * mm});
            skPoint(sketch, "E5.0.31.21", {"position": v(400.5, 281.68) * mm});
            skPoint(sketch, "E5.0.31.22", {"position": v(400.5, 293.46) * mm});
            skPoint(sketch, "E5.0.31.23", {"position": v(400.5, 305.25) * mm});
            skPoint(sketch, "E5.0.31.24", {"position": v(400.5, 317.03) * mm});
            skPoint(sketch, "E5.0.31.25", {"position": v(400.5, 328.82) * mm});
            skPoint(sketch, "E5.0.31.26", {"position": v(400.5, 340.6) * mm});
            skPoint(sketch, "E5.0.31.27", {"position": v(400.5, 352.39) * mm});
            skPoint(sketch, "E5.0.31.28", {"position": v(400.5, 364.17) * mm});
            skPoint(sketch, "E5.0.31.29", {"position": v(400.5, 375.96) * mm});
            skPoint(sketch, "E5.0.31.30", {"position": v(400.5, 387.74) * mm});
            skPoint(sketch, "E5.0.31.31", {"position": v(400.5, 399.53) * mm});
            skPoint(sketch, "E5.0.31.32", {"position": v(400.5, 411.31) * mm});
            skPoint(sketch, "E5.0.31.33", {"position": v(400.5, 423.1) * mm});
            skPoint(sketch, "E5.0.31.34", {"position": v(400.5, 434.88) * mm});
            skPoint(sketch, "E5.0.31.35", {"position": v(400.5, 446.67) * mm});
            skPoint(sketch, "E5.0.31.36", {"position": v(400.5, 458.45) * mm});
            skPoint(sketch, "E5.0.31.37", {"position": v(400.5, 470.24) * mm});
            skPoint(sketch, "E5.0.31.38", {"position": v(400.5, 482.02) * mm});
            skPoint(sketch, "E5.0.31.39", {"position": v(400.5, 493.8) * mm});
            skPoint(sketch, "E5.0.31.40", {"position": v(400.5, 505.6) * mm});
            skPoint(sketch, "E5.0.31.41", {"position": v(400.5, 517.38) * mm});
            skPoint(sketch, "E5.0.31.42", {"position": v(400.5, 529.16) * mm});
            skPoint(sketch, "E5.0.31.43", {"position": v(400.5, 540.95) * mm});
            skPoint(sketch, "E5.0.31.44", {"position": v(400.5, 552.73) * mm});
            skPoint(sketch, "E5.0.31.45", {"position": v(400.5, 564.52) * mm});
            skPoint(sketch, "E5.0.31.46", {"position": v(400.5, 576.3) * mm});
            skPoint(sketch, "E5.0.31.47", {"position": v(400.5, 588.09) * mm});
            skPoint(sketch, "E5.0.32.0", {"position": v(412.28, 34.19) * mm});
            skPoint(sketch, "E5.0.32.1", {"position": v(412.28, 45.97) * mm});
            skPoint(sketch, "E5.0.32.2", {"position": v(412.28, 57.76) * mm});
            skPoint(sketch, "E5.0.32.3", {"position": v(412.28, 69.54) * mm});
            skPoint(sketch, "E5.0.32.4", {"position": v(412.28, 81.33) * mm});
            skPoint(sketch, "E5.0.32.5", {"position": v(412.28, 93.11) * mm});
            skPoint(sketch, "E5.0.32.6", {"position": v(412.28, 104.9) * mm});
            skPoint(sketch, "E5.0.32.7", {"position": v(412.28, 116.68) * mm});
            skPoint(sketch, "E5.0.32.8", {"position": v(412.28, 128.47) * mm});
            skPoint(sketch, "E5.0.32.9", {"position": v(412.28, 140.25) * mm});
            skPoint(sketch, "E5.0.32.10", {"position": v(412.28, 152.04) * mm});
            skPoint(sketch, "E5.0.32.11", {"position": v(412.28, 163.82) * mm});
            skPoint(sketch, "E5.0.32.12", {"position": v(412.28, 175.6) * mm});
            skPoint(sketch, "E5.0.32.13", {"position": v(412.28, 187.4) * mm});
            skPoint(sketch, "E5.0.32.14", {"position": v(412.28, 199.18) * mm});
            skPoint(sketch, "E5.0.32.15", {"position": v(412.28, 210.97) * mm});
            skPoint(sketch, "E5.0.32.16", {"position": v(412.28, 222.75) * mm});
            skPoint(sketch, "E5.0.32.17", {"position": v(412.28, 234.54) * mm});
            skPoint(sketch, "E5.0.32.18", {"position": v(412.28, 246.32) * mm});
            skPoint(sketch, "E5.0.32.19", {"position": v(412.28, 258.1) * mm});
            skPoint(sketch, "E5.0.32.20", {"position": v(412.28, 269.9) * mm});
            skPoint(sketch, "E5.0.32.21", {"position": v(412.28, 281.68) * mm});
            skPoint(sketch, "E5.0.32.22", {"position": v(412.28, 293.46) * mm});
            skPoint(sketch, "E5.0.32.23", {"position": v(412.28, 305.25) * mm});
            skPoint(sketch, "E5.0.32.24", {"position": v(412.28, 317.03) * mm});
            skPoint(sketch, "E5.0.32.25", {"position": v(412.28, 328.82) * mm});
            skPoint(sketch, "E5.0.32.26", {"position": v(412.28, 340.6) * mm});
            skPoint(sketch, "E5.0.32.27", {"position": v(412.28, 352.39) * mm});
            skPoint(sketch, "E5.0.32.28", {"position": v(412.28, 364.17) * mm});
            skPoint(sketch, "E5.0.32.29", {"position": v(412.28, 375.96) * mm});
            skPoint(sketch, "E5.0.32.30", {"position": v(412.28, 387.74) * mm});
            skPoint(sketch, "E5.0.32.31", {"position": v(412.28, 399.53) * mm});
            skPoint(sketch, "E5.0.32.32", {"position": v(412.28, 411.31) * mm});
            skPoint(sketch, "E5.0.32.33", {"position": v(412.28, 423.1) * mm});
            skPoint(sketch, "E5.0.32.34", {"position": v(412.28, 434.88) * mm});
            skPoint(sketch, "E5.0.32.35", {"position": v(412.28, 446.67) * mm});
            skPoint(sketch, "E5.0.32.36", {"position": v(412.28, 458.45) * mm});
            skPoint(sketch, "E5.0.32.37", {"position": v(412.28, 470.24) * mm});
            skPoint(sketch, "E5.0.32.38", {"position": v(412.28, 482.02) * mm});
            skPoint(sketch, "E5.0.32.39", {"position": v(412.28, 493.8) * mm});
            skPoint(sketch, "E5.0.32.40", {"position": v(412.28, 505.6) * mm});
            skPoint(sketch, "E5.0.32.41", {"position": v(412.28, 517.38) * mm});
            skPoint(sketch, "E5.0.32.42", {"position": v(412.28, 529.16) * mm});
            skPoint(sketch, "E5.0.32.43", {"position": v(412.28, 540.95) * mm});
            skPoint(sketch, "E5.0.32.44", {"position": v(412.28, 552.73) * mm});
            skPoint(sketch, "E5.0.32.45", {"position": v(412.28, 564.52) * mm});
            skPoint(sketch, "E5.0.32.46", {"position": v(412.28, 576.3) * mm});
            skPoint(sketch, "E5.0.32.47", {"position": v(412.28, 588.09) * mm});
            skPoint(sketch, "E5.0.33.0", {"position": v(424.06, 34.19) * mm});
            skPoint(sketch, "E5.0.33.1", {"position": v(424.06, 45.97) * mm});
            skPoint(sketch, "E5.0.33.2", {"position": v(424.06, 57.76) * mm});
            skPoint(sketch, "E5.0.33.3", {"position": v(424.06, 69.54) * mm});
            skPoint(sketch, "E5.0.33.4", {"position": v(424.06, 81.33) * mm});
            skPoint(sketch, "E5.0.33.5", {"position": v(424.06, 93.11) * mm});
            skPoint(sketch, "E5.0.33.6", {"position": v(424.06, 104.9) * mm});
            skPoint(sketch, "E5.0.33.7", {"position": v(424.06, 116.68) * mm});
            skPoint(sketch, "E5.0.33.8", {"position": v(424.06, 128.47) * mm});
            skPoint(sketch, "E5.0.33.9", {"position": v(424.06, 140.25) * mm});
            skPoint(sketch, "E5.0.33.10", {"position": v(424.06, 152.04) * mm});
            skPoint(sketch, "E5.0.33.11", {"position": v(424.06, 163.82) * mm});
            skPoint(sketch, "E5.0.33.12", {"position": v(424.06, 175.6) * mm});
            skPoint(sketch, "E5.0.33.13", {"position": v(424.06, 187.4) * mm});
            skPoint(sketch, "E5.0.33.14", {"position": v(424.06, 199.18) * mm});
            skPoint(sketch, "E5.0.33.15", {"position": v(424.06, 210.97) * mm});
            skPoint(sketch, "E5.0.33.16", {"position": v(424.06, 222.75) * mm});
            skPoint(sketch, "E5.0.33.17", {"position": v(424.06, 234.54) * mm});
            skPoint(sketch, "E5.0.33.18", {"position": v(424.06, 246.32) * mm});
            skPoint(sketch, "E5.0.33.19", {"position": v(424.06, 258.1) * mm});
            skPoint(sketch, "E5.0.33.20", {"position": v(424.06, 269.9) * mm});
            skPoint(sketch, "E5.0.33.21", {"position": v(424.06, 281.68) * mm});
            skPoint(sketch, "E5.0.33.22", {"position": v(424.06, 293.46) * mm});
            skPoint(sketch, "E5.0.33.23", {"position": v(424.06, 305.25) * mm});
            skPoint(sketch, "E5.0.33.24", {"position": v(424.06, 317.03) * mm});
            skPoint(sketch, "E5.0.33.25", {"position": v(424.06, 328.82) * mm});
            skPoint(sketch, "E5.0.33.26", {"position": v(424.06, 340.6) * mm});
            skPoint(sketch, "E5.0.33.27", {"position": v(424.06, 352.39) * mm});
            skPoint(sketch, "E5.0.33.28", {"position": v(424.06, 364.17) * mm});
            skPoint(sketch, "E5.0.33.29", {"position": v(424.06, 375.96) * mm});
            skPoint(sketch, "E5.0.33.30", {"position": v(424.06, 387.74) * mm});
            skPoint(sketch, "E5.0.33.31", {"position": v(424.06, 399.53) * mm});
            skPoint(sketch, "E5.0.33.32", {"position": v(424.06, 411.31) * mm});
            skPoint(sketch, "E5.0.33.33", {"position": v(424.06, 423.1) * mm});
            skPoint(sketch, "E5.0.33.34", {"position": v(424.06, 434.88) * mm});
            skPoint(sketch, "E5.0.33.35", {"position": v(424.06, 446.67) * mm});
            skPoint(sketch, "E5.0.33.36", {"position": v(424.06, 458.45) * mm});
            skPoint(sketch, "E5.0.33.37", {"position": v(424.06, 470.24) * mm});
            skPoint(sketch, "E5.0.33.38", {"position": v(424.06, 482.02) * mm});
            skPoint(sketch, "E5.0.33.39", {"position": v(424.06, 493.8) * mm});
            skPoint(sketch, "E5.0.33.40", {"position": v(424.06, 505.6) * mm});
            skPoint(sketch, "E5.0.33.41", {"position": v(424.06, 517.38) * mm});
            skPoint(sketch, "E5.0.33.42", {"position": v(424.06, 529.16) * mm});
            skPoint(sketch, "E5.0.33.43", {"position": v(424.06, 540.95) * mm});
            skPoint(sketch, "E5.0.33.44", {"position": v(424.06, 552.73) * mm});
            skPoint(sketch, "E5.0.33.45", {"position": v(424.06, 564.52) * mm});
            skPoint(sketch, "E5.0.33.46", {"position": v(424.06, 576.3) * mm});
            skPoint(sketch, "E5.0.33.47", {"position": v(424.06, 588.09) * mm});
            skPoint(sketch, "E5.0.34.0", {"position": v(435.85, 34.19) * mm});
            skPoint(sketch, "E5.0.34.1", {"position": v(435.85, 45.97) * mm});
            skPoint(sketch, "E5.0.34.2", {"position": v(435.85, 57.76) * mm});
            skPoint(sketch, "E5.0.34.3", {"position": v(435.85, 69.54) * mm});
            skPoint(sketch, "E5.0.34.4", {"position": v(435.85, 81.33) * mm});
            skPoint(sketch, "E5.0.34.5", {"position": v(435.85, 93.11) * mm});
            skPoint(sketch, "E5.0.34.6", {"position": v(435.85, 104.9) * mm});
            skPoint(sketch, "E5.0.34.7", {"position": v(435.85, 116.68) * mm});
            skPoint(sketch, "E5.0.34.8", {"position": v(435.85, 128.47) * mm});
            skPoint(sketch, "E5.0.34.9", {"position": v(435.85, 140.25) * mm});
            skPoint(sketch, "E5.0.34.10", {"position": v(435.85, 152.04) * mm});
            skPoint(sketch, "E5.0.34.11", {"position": v(435.85, 163.82) * mm});
            skPoint(sketch, "E5.0.34.12", {"position": v(435.85, 175.6) * mm});
            skPoint(sketch, "E5.0.34.13", {"position": v(435.85, 187.4) * mm});
            skPoint(sketch, "E5.0.34.14", {"position": v(435.85, 199.18) * mm});
            skPoint(sketch, "E5.0.34.15", {"position": v(435.85, 210.97) * mm});
            skPoint(sketch, "E5.0.34.16", {"position": v(435.85, 222.75) * mm});
            skPoint(sketch, "E5.0.34.17", {"position": v(435.85, 234.54) * mm});
            skPoint(sketch, "E5.0.34.18", {"position": v(435.85, 246.32) * mm});
            skPoint(sketch, "E5.0.34.19", {"position": v(435.85, 258.1) * mm});
            skPoint(sketch, "E5.0.34.20", {"position": v(435.85, 269.9) * mm});
            skPoint(sketch, "E5.0.34.21", {"position": v(435.85, 281.68) * mm});
            skPoint(sketch, "E5.0.34.22", {"position": v(435.85, 293.46) * mm});
            skPoint(sketch, "E5.0.34.23", {"position": v(435.85, 305.25) * mm});
            skPoint(sketch, "E5.0.34.24", {"position": v(435.85, 317.03) * mm});
            skPoint(sketch, "E5.0.34.25", {"position": v(435.85, 328.82) * mm});
            skPoint(sketch, "E5.0.34.26", {"position": v(435.85, 340.6) * mm});
            skPoint(sketch, "E5.0.34.27", {"position": v(435.85, 352.39) * mm});
            skPoint(sketch, "E5.0.34.28", {"position": v(435.85, 364.17) * mm});
            skPoint(sketch, "E5.0.34.29", {"position": v(435.85, 375.96) * mm});
            skPoint(sketch, "E5.0.34.30", {"position": v(435.85, 387.74) * mm});
            skPoint(sketch, "E5.0.34.31", {"position": v(435.85, 399.53) * mm});
            skPoint(sketch, "E5.0.34.32", {"position": v(435.85, 411.31) * mm});
            skPoint(sketch, "E5.0.34.33", {"position": v(435.85, 423.1) * mm});
            skPoint(sketch, "E5.0.34.34", {"position": v(435.85, 434.88) * mm});
            skPoint(sketch, "E5.0.34.35", {"position": v(435.85, 446.67) * mm});
            skPoint(sketch, "E5.0.34.36", {"position": v(435.85, 458.45) * mm});
            skPoint(sketch, "E5.0.34.37", {"position": v(435.85, 470.24) * mm});
            skPoint(sketch, "E5.0.34.38", {"position": v(435.85, 482.02) * mm});
            skPoint(sketch, "E5.0.34.39", {"position": v(435.85, 493.8) * mm});
            skPoint(sketch, "E5.0.34.40", {"position": v(435.85, 505.6) * mm});
            skPoint(sketch, "E5.0.34.41", {"position": v(435.85, 517.38) * mm});
            skPoint(sketch, "E5.0.34.42", {"position": v(435.85, 529.16) * mm});
            skPoint(sketch, "E5.0.34.43", {"position": v(435.85, 540.95) * mm});
            skPoint(sketch, "E5.0.34.44", {"position": v(435.85, 552.73) * mm});
            skPoint(sketch, "E5.0.34.45", {"position": v(435.85, 564.52) * mm});
            skPoint(sketch, "E5.0.34.46", {"position": v(435.85, 576.3) * mm});
            skPoint(sketch, "E5.0.34.47", {"position": v(435.85, 588.09) * mm});
            skPoint(sketch, "E5.0.35.0", {"position": v(447.63, 34.19) * mm});
            skPoint(sketch, "E5.0.35.1", {"position": v(447.63, 45.97) * mm});
            skPoint(sketch, "E5.0.35.2", {"position": v(447.63, 57.76) * mm});
            skPoint(sketch, "E5.0.35.3", {"position": v(447.63, 69.54) * mm});
            skPoint(sketch, "E5.0.35.4", {"position": v(447.63, 81.33) * mm});
            skPoint(sketch, "E5.0.35.5", {"position": v(447.63, 93.11) * mm});
            skPoint(sketch, "E5.0.35.6", {"position": v(447.63, 104.9) * mm});
            skPoint(sketch, "E5.0.35.7", {"position": v(447.63, 116.68) * mm});
            skPoint(sketch, "E5.0.35.8", {"position": v(447.63, 128.47) * mm});
            skPoint(sketch, "E5.0.35.9", {"position": v(447.63, 140.25) * mm});
            skPoint(sketch, "E5.0.35.10", {"position": v(447.63, 152.04) * mm});
            skPoint(sketch, "E5.0.35.11", {"position": v(447.63, 163.82) * mm});
            skPoint(sketch, "E5.0.35.12", {"position": v(447.63, 175.6) * mm});
            skPoint(sketch, "E5.0.35.13", {"position": v(447.63, 187.4) * mm});
            skPoint(sketch, "E5.0.35.14", {"position": v(447.63, 199.18) * mm});
            skPoint(sketch, "E5.0.35.15", {"position": v(447.63, 210.97) * mm});
            skPoint(sketch, "E5.0.35.16", {"position": v(447.63, 222.75) * mm});
            skPoint(sketch, "E5.0.35.17", {"position": v(447.63, 234.54) * mm});
            skPoint(sketch, "E5.0.35.18", {"position": v(447.63, 246.32) * mm});
            skPoint(sketch, "E5.0.35.19", {"position": v(447.63, 258.1) * mm});
            skPoint(sketch, "E5.0.35.20", {"position": v(447.63, 269.9) * mm});
            skPoint(sketch, "E5.0.35.21", {"position": v(447.63, 281.68) * mm});
            skPoint(sketch, "E5.0.35.22", {"position": v(447.63, 293.46) * mm});
            skPoint(sketch, "E5.0.35.23", {"position": v(447.63, 305.25) * mm});
            skPoint(sketch, "E5.0.35.24", {"position": v(447.63, 317.03) * mm});
            skPoint(sketch, "E5.0.35.25", {"position": v(447.63, 328.82) * mm});
            skPoint(sketch, "E5.0.35.26", {"position": v(447.63, 340.6) * mm});
            skPoint(sketch, "E5.0.35.27", {"position": v(447.63, 352.39) * mm});
            skPoint(sketch, "E5.0.35.28", {"position": v(447.63, 364.17) * mm});
            skPoint(sketch, "E5.0.35.29", {"position": v(447.63, 375.96) * mm});
            skPoint(sketch, "E5.0.35.30", {"position": v(447.63, 387.74) * mm});
            skPoint(sketch, "E5.0.35.31", {"position": v(447.63, 399.53) * mm});
            skPoint(sketch, "E5.0.35.32", {"position": v(447.63, 411.31) * mm});
            skPoint(sketch, "E5.0.35.33", {"position": v(447.63, 423.1) * mm});
            skPoint(sketch, "E5.0.35.34", {"position": v(447.63, 434.88) * mm});
            skPoint(sketch, "E5.0.35.35", {"position": v(447.63, 446.67) * mm});
            skPoint(sketch, "E5.0.35.36", {"position": v(447.63, 458.45) * mm});
            skPoint(sketch, "E5.0.35.37", {"position": v(447.63, 470.24) * mm});
            skPoint(sketch, "E5.0.35.38", {"position": v(447.63, 482.02) * mm});
            skPoint(sketch, "E5.0.35.39", {"position": v(447.63, 493.8) * mm});
            skPoint(sketch, "E5.0.35.40", {"position": v(447.63, 505.6) * mm});
            skPoint(sketch, "E5.0.35.41", {"position": v(447.63, 517.38) * mm});
            skPoint(sketch, "E5.0.35.42", {"position": v(447.63, 529.16) * mm});
            skPoint(sketch, "E5.0.35.43", {"position": v(447.63, 540.95) * mm});
            skPoint(sketch, "E5.0.35.44", {"position": v(447.63, 552.73) * mm});
            skPoint(sketch, "E5.0.35.45", {"position": v(447.63, 564.52) * mm});
            skPoint(sketch, "E5.0.35.46", {"position": v(447.63, 576.3) * mm});
            skPoint(sketch, "E5.0.35.47", {"position": v(447.63, 588.09) * mm});
            skPoint(sketch, "E5.0.36.0", {"position": v(459.42, 34.19) * mm});
            skPoint(sketch, "E5.0.36.1", {"position": v(459.42, 45.97) * mm});
            skPoint(sketch, "E5.0.36.2", {"position": v(459.42, 57.76) * mm});
            skPoint(sketch, "E5.0.36.3", {"position": v(459.42, 69.54) * mm});
            skPoint(sketch, "E5.0.36.4", {"position": v(459.42, 81.33) * mm});
            skPoint(sketch, "E5.0.36.5", {"position": v(459.42, 93.11) * mm});
            skPoint(sketch, "E5.0.36.6", {"position": v(459.42, 104.9) * mm});
            skPoint(sketch, "E5.0.36.7", {"position": v(459.42, 116.68) * mm});
            skPoint(sketch, "E5.0.36.8", {"position": v(459.42, 128.47) * mm});
            skPoint(sketch, "E5.0.36.9", {"position": v(459.42, 140.25) * mm});
            skPoint(sketch, "E5.0.36.10", {"position": v(459.42, 152.04) * mm});
            skPoint(sketch, "E5.0.36.11", {"position": v(459.42, 163.82) * mm});
            skPoint(sketch, "E5.0.36.12", {"position": v(459.42, 175.6) * mm});
            skPoint(sketch, "E5.0.36.13", {"position": v(459.42, 187.4) * mm});
            skPoint(sketch, "E5.0.36.14", {"position": v(459.42, 199.18) * mm});
            skPoint(sketch, "E5.0.36.15", {"position": v(459.42, 210.97) * mm});
            skPoint(sketch, "E5.0.36.16", {"position": v(459.42, 222.75) * mm});
            skPoint(sketch, "E5.0.36.17", {"position": v(459.42, 234.54) * mm});
            skPoint(sketch, "E5.0.36.18", {"position": v(459.42, 246.32) * mm});
            skPoint(sketch, "E5.0.36.19", {"position": v(459.42, 258.1) * mm});
            skPoint(sketch, "E5.0.36.20", {"position": v(459.42, 269.9) * mm});
            skPoint(sketch, "E5.0.36.21", {"position": v(459.42, 281.68) * mm});
            skPoint(sketch, "E5.0.36.22", {"position": v(459.42, 293.46) * mm});
            skPoint(sketch, "E5.0.36.23", {"position": v(459.42, 305.25) * mm});
            skPoint(sketch, "E5.0.36.24", {"position": v(459.42, 317.03) * mm});
            skPoint(sketch, "E5.0.36.25", {"position": v(459.42, 328.82) * mm});
            skPoint(sketch, "E5.0.36.26", {"position": v(459.42, 340.6) * mm});
            skPoint(sketch, "E5.0.36.27", {"position": v(459.42, 352.39) * mm});
            skPoint(sketch, "E5.0.36.28", {"position": v(459.42, 364.17) * mm});
            skPoint(sketch, "E5.0.36.29", {"position": v(459.42, 375.96) * mm});
            skPoint(sketch, "E5.0.36.30", {"position": v(459.42, 387.74) * mm});
            skPoint(sketch, "E5.0.36.31", {"position": v(459.42, 399.53) * mm});
            skPoint(sketch, "E5.0.36.32", {"position": v(459.42, 411.31) * mm});
            skPoint(sketch, "E5.0.36.33", {"position": v(459.42, 423.1) * mm});
            skPoint(sketch, "E5.0.36.34", {"position": v(459.42, 434.88) * mm});
            skPoint(sketch, "E5.0.36.35", {"position": v(459.42, 446.67) * mm});
            skPoint(sketch, "E5.0.36.36", {"position": v(459.42, 458.45) * mm});
            skPoint(sketch, "E5.0.36.37", {"position": v(459.42, 470.24) * mm});
            skPoint(sketch, "E5.0.36.38", {"position": v(459.42, 482.02) * mm});
            skPoint(sketch, "E5.0.36.39", {"position": v(459.42, 493.8) * mm});
            skPoint(sketch, "E5.0.36.40", {"position": v(459.42, 505.6) * mm});
            skPoint(sketch, "E5.0.36.41", {"position": v(459.42, 517.38) * mm});
            skPoint(sketch, "E5.0.36.42", {"position": v(459.42, 529.16) * mm});
            skPoint(sketch, "E5.0.36.43", {"position": v(459.42, 540.95) * mm});
            skPoint(sketch, "E5.0.36.44", {"position": v(459.42, 552.73) * mm});
            skPoint(sketch, "E5.0.36.45", {"position": v(459.42, 564.52) * mm});
            skPoint(sketch, "E5.0.36.46", {"position": v(459.42, 576.3) * mm});
            skPoint(sketch, "E5.0.36.47", {"position": v(459.42, 588.09) * mm});
            skPoint(sketch, "E5.0.37.0", {"position": v(471.2, 34.19) * mm});
            skPoint(sketch, "E5.0.37.1", {"position": v(471.2, 45.97) * mm});
            skPoint(sketch, "E5.0.37.2", {"position": v(471.2, 57.76) * mm});
            skPoint(sketch, "E5.0.37.3", {"position": v(471.2, 69.54) * mm});
            skPoint(sketch, "E5.0.37.4", {"position": v(471.2, 81.33) * mm});
            skPoint(sketch, "E5.0.37.5", {"position": v(471.2, 93.11) * mm});
            skPoint(sketch, "E5.0.37.6", {"position": v(471.2, 104.9) * mm});
            skPoint(sketch, "E5.0.37.7", {"position": v(471.2, 116.68) * mm});
            skPoint(sketch, "E5.0.37.8", {"position": v(471.2, 128.47) * mm});
            skPoint(sketch, "E5.0.37.9", {"position": v(471.2, 140.25) * mm});
            skPoint(sketch, "E5.0.37.10", {"position": v(471.2, 152.04) * mm});
            skPoint(sketch, "E5.0.37.11", {"position": v(471.2, 163.82) * mm});
            skPoint(sketch, "E5.0.37.12", {"position": v(471.2, 175.6) * mm});
            skPoint(sketch, "E5.0.37.13", {"position": v(471.2, 187.4) * mm});
            skPoint(sketch, "E5.0.37.14", {"position": v(471.2, 199.18) * mm});
            skPoint(sketch, "E5.0.37.15", {"position": v(471.2, 210.97) * mm});
            skPoint(sketch, "E5.0.37.16", {"position": v(471.2, 222.75) * mm});
            skPoint(sketch, "E5.0.37.17", {"position": v(471.2, 234.54) * mm});
            skPoint(sketch, "E5.0.37.18", {"position": v(471.2, 246.32) * mm});
            skPoint(sketch, "E5.0.37.19", {"position": v(471.2, 258.1) * mm});
            skPoint(sketch, "E5.0.37.20", {"position": v(471.2, 269.9) * mm});
            skPoint(sketch, "E5.0.37.21", {"position": v(471.2, 281.68) * mm});
            skPoint(sketch, "E5.0.37.22", {"position": v(471.2, 293.46) * mm});
            skPoint(sketch, "E5.0.37.23", {"position": v(471.2, 305.25) * mm});
            skPoint(sketch, "E5.0.37.24", {"position": v(471.2, 317.03) * mm});
            skPoint(sketch, "E5.0.37.25", {"position": v(471.2, 328.82) * mm});
            skPoint(sketch, "E5.0.37.26", {"position": v(471.2, 340.6) * mm});
            skPoint(sketch, "E5.0.37.27", {"position": v(471.2, 352.39) * mm});
            skPoint(sketch, "E5.0.37.28", {"position": v(471.2, 364.17) * mm});
            skPoint(sketch, "E5.0.37.29", {"position": v(471.2, 375.96) * mm});
            skPoint(sketch, "E5.0.37.30", {"position": v(471.2, 387.74) * mm});
            skPoint(sketch, "E5.0.37.31", {"position": v(471.2, 399.53) * mm});
            skPoint(sketch, "E5.0.37.32", {"position": v(471.2, 411.31) * mm});
            skPoint(sketch, "E5.0.37.33", {"position": v(471.2, 423.1) * mm});
            skPoint(sketch, "E5.0.37.34", {"position": v(471.2, 434.88) * mm});
            skPoint(sketch, "E5.0.37.35", {"position": v(471.2, 446.67) * mm});
            skPoint(sketch, "E5.0.37.36", {"position": v(471.2, 458.45) * mm});
            skPoint(sketch, "E5.0.37.37", {"position": v(471.2, 470.24) * mm});
            skPoint(sketch, "E5.0.37.38", {"position": v(471.2, 482.02) * mm});
            skPoint(sketch, "E5.0.37.39", {"position": v(471.2, 493.8) * mm});
            skPoint(sketch, "E5.0.37.40", {"position": v(471.2, 505.6) * mm});
            skPoint(sketch, "E5.0.37.41", {"position": v(471.2, 517.38) * mm});
            skPoint(sketch, "E5.0.37.42", {"position": v(471.2, 529.16) * mm});
            skPoint(sketch, "E5.0.37.43", {"position": v(471.2, 540.95) * mm});
            skPoint(sketch, "E5.0.37.44", {"position": v(471.2, 552.73) * mm});
            skPoint(sketch, "E5.0.37.45", {"position": v(471.2, 564.52) * mm});
            skPoint(sketch, "E5.0.37.46", {"position": v(471.2, 576.3) * mm});
            skPoint(sketch, "E5.0.37.47", {"position": v(471.2, 588.09) * mm});
            skPoint(sketch, "E5.0.38.0", {"position": v(482.99, 34.19) * mm});
            skPoint(sketch, "E5.0.38.1", {"position": v(482.99, 45.97) * mm});
            skPoint(sketch, "E5.0.38.2", {"position": v(482.99, 57.76) * mm});
            skPoint(sketch, "E5.0.38.3", {"position": v(482.99, 69.54) * mm});
            skPoint(sketch, "E5.0.38.4", {"position": v(482.99, 81.33) * mm});
            skPoint(sketch, "E5.0.38.5", {"position": v(482.99, 93.11) * mm});
            skPoint(sketch, "E5.0.38.6", {"position": v(482.99, 104.9) * mm});
            skPoint(sketch, "E5.0.38.7", {"position": v(482.99, 116.68) * mm});
            skPoint(sketch, "E5.0.38.8", {"position": v(482.99, 128.47) * mm});
            skPoint(sketch, "E5.0.38.9", {"position": v(482.99, 140.25) * mm});
            skPoint(sketch, "E5.0.38.10", {"position": v(482.99, 152.04) * mm});
            skPoint(sketch, "E5.0.38.11", {"position": v(482.99, 163.82) * mm});
            skPoint(sketch, "E5.0.38.12", {"position": v(482.99, 175.6) * mm});
            skPoint(sketch, "E5.0.38.13", {"position": v(482.99, 187.4) * mm});
            skPoint(sketch, "E5.0.38.14", {"position": v(482.99, 199.18) * mm});
            skPoint(sketch, "E5.0.38.15", {"position": v(482.99, 210.97) * mm});
            skPoint(sketch, "E5.0.38.16", {"position": v(482.99, 222.75) * mm});
            skPoint(sketch, "E5.0.38.17", {"position": v(482.99, 234.54) * mm});
            skPoint(sketch, "E5.0.38.18", {"position": v(482.99, 246.32) * mm});
            skPoint(sketch, "E5.0.38.19", {"position": v(482.99, 258.1) * mm});
            skPoint(sketch, "E5.0.38.20", {"position": v(482.99, 269.9) * mm});
            skPoint(sketch, "E5.0.38.21", {"position": v(482.99, 281.68) * mm});
            skPoint(sketch, "E5.0.38.22", {"position": v(482.99, 293.46) * mm});
            skPoint(sketch, "E5.0.38.23", {"position": v(482.99, 305.25) * mm});
            skPoint(sketch, "E5.0.38.24", {"position": v(482.99, 317.03) * mm});
            skPoint(sketch, "E5.0.38.25", {"position": v(482.99, 328.82) * mm});
            skPoint(sketch, "E5.0.38.26", {"position": v(482.99, 340.6) * mm});
            skPoint(sketch, "E5.0.38.27", {"position": v(482.99, 352.39) * mm});
            skPoint(sketch, "E5.0.38.28", {"position": v(482.99, 364.17) * mm});
            skPoint(sketch, "E5.0.38.29", {"position": v(482.99, 375.96) * mm});
            skPoint(sketch, "E5.0.38.30", {"position": v(482.99, 387.74) * mm});
            skPoint(sketch, "E5.0.38.31", {"position": v(482.99, 399.53) * mm});
            skPoint(sketch, "E5.0.38.32", {"position": v(482.99, 411.31) * mm});
            skPoint(sketch, "E5.0.38.33", {"position": v(482.99, 423.1) * mm});
            skPoint(sketch, "E5.0.38.34", {"position": v(482.99, 434.88) * mm});
            skPoint(sketch, "E5.0.38.35", {"position": v(482.99, 446.67) * mm});
            skPoint(sketch, "E5.0.38.36", {"position": v(482.99, 458.45) * mm});
            skPoint(sketch, "E5.0.38.37", {"position": v(482.99, 470.24) * mm});
            skPoint(sketch, "E5.0.38.38", {"position": v(482.99, 482.02) * mm});
            skPoint(sketch, "E5.0.38.39", {"position": v(482.99, 493.8) * mm});
            skPoint(sketch, "E5.0.38.40", {"position": v(482.99, 505.6) * mm});
            skPoint(sketch, "E5.0.38.41", {"position": v(482.99, 517.38) * mm});
            skPoint(sketch, "E5.0.38.42", {"position": v(482.99, 529.16) * mm});
            skPoint(sketch, "E5.0.38.43", {"position": v(482.99, 540.95) * mm});
            skPoint(sketch, "E5.0.38.44", {"position": v(482.99, 552.73) * mm});
            skPoint(sketch, "E5.0.38.45", {"position": v(482.99, 564.52) * mm});
            skPoint(sketch, "E5.0.38.46", {"position": v(482.99, 576.3) * mm});
            skPoint(sketch, "E5.0.38.47", {"position": v(482.99, 588.09) * mm});
            skPoint(sketch, "E5.0.39.0", {"position": v(494.77, 34.19) * mm});
            skPoint(sketch, "E5.0.39.1", {"position": v(494.77, 45.97) * mm});
            skPoint(sketch, "E5.0.39.2", {"position": v(494.77, 57.76) * mm});
            skPoint(sketch, "E5.0.39.3", {"position": v(494.77, 69.54) * mm});
            skPoint(sketch, "E5.0.39.4", {"position": v(494.77, 81.33) * mm});
            skPoint(sketch, "E5.0.39.5", {"position": v(494.77, 93.11) * mm});
            skPoint(sketch, "E5.0.39.6", {"position": v(494.77, 104.9) * mm});
            skPoint(sketch, "E5.0.39.7", {"position": v(494.77, 116.68) * mm});
            skPoint(sketch, "E5.0.39.8", {"position": v(494.77, 128.47) * mm});
            skPoint(sketch, "E5.0.39.9", {"position": v(494.77, 140.25) * mm});
            skPoint(sketch, "E5.0.39.10", {"position": v(494.77, 152.04) * mm});
            skPoint(sketch, "E5.0.39.11", {"position": v(494.77, 163.82) * mm});
            skPoint(sketch, "E5.0.39.12", {"position": v(494.77, 175.6) * mm});
            skPoint(sketch, "E5.0.39.13", {"position": v(494.77, 187.4) * mm});
            skPoint(sketch, "E5.0.39.14", {"position": v(494.77, 199.18) * mm});
            skPoint(sketch, "E5.0.39.15", {"position": v(494.77, 210.97) * mm});
            skPoint(sketch, "E5.0.39.16", {"position": v(494.77, 222.75) * mm});
            skPoint(sketch, "E5.0.39.17", {"position": v(494.77, 234.54) * mm});
            skPoint(sketch, "E5.0.39.18", {"position": v(494.77, 246.32) * mm});
            skPoint(sketch, "E5.0.39.19", {"position": v(494.77, 258.1) * mm});
            skPoint(sketch, "E5.0.39.20", {"position": v(494.77, 269.9) * mm});
            skPoint(sketch, "E5.0.39.21", {"position": v(494.77, 281.68) * mm});
            skPoint(sketch, "E5.0.39.22", {"position": v(494.77, 293.46) * mm});
            skPoint(sketch, "E5.0.39.23", {"position": v(494.77, 305.25) * mm});
            skPoint(sketch, "E5.0.39.24", {"position": v(494.77, 317.03) * mm});
            skPoint(sketch, "E5.0.39.25", {"position": v(494.77, 328.82) * mm});
            skPoint(sketch, "E5.0.39.26", {"position": v(494.77, 340.6) * mm});
            skPoint(sketch, "E5.0.39.27", {"position": v(494.77, 352.39) * mm});
            skPoint(sketch, "E5.0.39.28", {"position": v(494.77, 364.17) * mm});
            skPoint(sketch, "E5.0.39.29", {"position": v(494.77, 375.96) * mm});
            skPoint(sketch, "E5.0.39.30", {"position": v(494.77, 387.74) * mm});
            skPoint(sketch, "E5.0.39.31", {"position": v(494.77, 399.53) * mm});
            skPoint(sketch, "E5.0.39.32", {"position": v(494.77, 411.31) * mm});
            skPoint(sketch, "E5.0.39.33", {"position": v(494.77, 423.1) * mm});
            skPoint(sketch, "E5.0.39.34", {"position": v(494.77, 434.88) * mm});
            skPoint(sketch, "E5.0.39.35", {"position": v(494.77, 446.67) * mm});
            skPoint(sketch, "E5.0.39.36", {"position": v(494.77, 458.45) * mm});
            skPoint(sketch, "E5.0.39.37", {"position": v(494.77, 470.24) * mm});
            skPoint(sketch, "E5.0.39.38", {"position": v(494.77, 482.02) * mm});
            skPoint(sketch, "E5.0.39.39", {"position": v(494.77, 493.8) * mm});
            skPoint(sketch, "E5.0.39.40", {"position": v(494.77, 505.6) * mm});
            skPoint(sketch, "E5.0.39.41", {"position": v(494.77, 517.38) * mm});
            skPoint(sketch, "E5.0.39.42", {"position": v(494.77, 529.16) * mm});
            skPoint(sketch, "E5.0.39.43", {"position": v(494.77, 540.95) * mm});
            skPoint(sketch, "E5.0.39.44", {"position": v(494.77, 552.73) * mm});
            skPoint(sketch, "E5.0.39.45", {"position": v(494.77, 564.52) * mm});
            skPoint(sketch, "E5.0.39.46", {"position": v(494.77, 576.3) * mm});
            skPoint(sketch, "E5.0.39.47", {"position": v(494.77, 588.09) * mm});
            skPoint(sketch, "E5.0.40.0", {"position": v(506.56, 34.19) * mm});
            skPoint(sketch, "E5.0.40.1", {"position": v(506.56, 45.97) * mm});
            skPoint(sketch, "E5.0.40.2", {"position": v(506.56, 57.76) * mm});
            skPoint(sketch, "E5.0.40.3", {"position": v(506.56, 69.54) * mm});
            skPoint(sketch, "E5.0.40.4", {"position": v(506.56, 81.33) * mm});
            skPoint(sketch, "E5.0.40.5", {"position": v(506.56, 93.11) * mm});
            skPoint(sketch, "E5.0.40.6", {"position": v(506.56, 104.9) * mm});
            skPoint(sketch, "E5.0.40.7", {"position": v(506.56, 116.68) * mm});
            skPoint(sketch, "E5.0.40.8", {"position": v(506.56, 128.47) * mm});
            skPoint(sketch, "E5.0.40.9", {"position": v(506.56, 140.25) * mm});
            skPoint(sketch, "E5.0.40.10", {"position": v(506.56, 152.04) * mm});
            skPoint(sketch, "E5.0.40.11", {"position": v(506.56, 163.82) * mm});
            skPoint(sketch, "E5.0.40.12", {"position": v(506.56, 175.6) * mm});
            skPoint(sketch, "E5.0.40.13", {"position": v(506.56, 187.4) * mm});
            skPoint(sketch, "E5.0.40.14", {"position": v(506.56, 199.18) * mm});
            skPoint(sketch, "E5.0.40.15", {"position": v(506.56, 210.97) * mm});
            skPoint(sketch, "E5.0.40.16", {"position": v(506.56, 222.75) * mm});
            skPoint(sketch, "E5.0.40.17", {"position": v(506.56, 234.54) * mm});
            skPoint(sketch, "E5.0.40.18", {"position": v(506.56, 246.32) * mm});
            skPoint(sketch, "E5.0.40.19", {"position": v(506.56, 258.1) * mm});
            skPoint(sketch, "E5.0.40.20", {"position": v(506.56, 269.9) * mm});
            skPoint(sketch, "E5.0.40.21", {"position": v(506.56, 281.68) * mm});
            skPoint(sketch, "E5.0.40.22", {"position": v(506.56, 293.46) * mm});
            skPoint(sketch, "E5.0.40.23", {"position": v(506.56, 305.25) * mm});
            skPoint(sketch, "E5.0.40.24", {"position": v(506.56, 317.03) * mm});
            skPoint(sketch, "E5.0.40.25", {"position": v(506.56, 328.82) * mm});
            skPoint(sketch, "E5.0.40.26", {"position": v(506.56, 340.6) * mm});
            skPoint(sketch, "E5.0.40.27", {"position": v(506.56, 352.39) * mm});
            skPoint(sketch, "E5.0.40.28", {"position": v(506.56, 364.17) * mm});
            skPoint(sketch, "E5.0.40.29", {"position": v(506.56, 375.96) * mm});
            skPoint(sketch, "E5.0.40.30", {"position": v(506.56, 387.74) * mm});
            skPoint(sketch, "E5.0.40.31", {"position": v(506.56, 399.53) * mm});
            skPoint(sketch, "E5.0.40.32", {"position": v(506.56, 411.31) * mm});
            skPoint(sketch, "E5.0.40.33", {"position": v(506.56, 423.1) * mm});
            skPoint(sketch, "E5.0.40.34", {"position": v(506.56, 434.88) * mm});
            skPoint(sketch, "E5.0.40.35", {"position": v(506.56, 446.67) * mm});
            skPoint(sketch, "E5.0.40.36", {"position": v(506.56, 458.45) * mm});
            skPoint(sketch, "E5.0.40.37", {"position": v(506.56, 470.24) * mm});
            skPoint(sketch, "E5.0.40.38", {"position": v(506.56, 482.02) * mm});
            skPoint(sketch, "E5.0.40.39", {"position": v(506.56, 493.8) * mm});
            skPoint(sketch, "E5.0.40.40", {"position": v(506.56, 505.6) * mm});
            skPoint(sketch, "E5.0.40.41", {"position": v(506.56, 517.38) * mm});
            skPoint(sketch, "E5.0.40.42", {"position": v(506.56, 529.16) * mm});
            skPoint(sketch, "E5.0.40.43", {"position": v(506.56, 540.95) * mm});
            skPoint(sketch, "E5.0.40.44", {"position": v(506.56, 552.73) * mm});
            skPoint(sketch, "E5.0.40.45", {"position": v(506.56, 564.52) * mm});
            skPoint(sketch, "E5.0.40.46", {"position": v(506.56, 576.3) * mm});
            skPoint(sketch, "E5.0.40.47", {"position": v(506.56, 588.09) * mm});
            skPoint(sketch, "E5.0.41.0", {"position": v(518.34, 34.19) * mm});
            skPoint(sketch, "E5.0.41.1", {"position": v(518.34, 45.97) * mm});
            skPoint(sketch, "E5.0.41.2", {"position": v(518.34, 57.76) * mm});
            skPoint(sketch, "E5.0.41.3", {"position": v(518.34, 69.54) * mm});
            skPoint(sketch, "E5.0.41.4", {"position": v(518.34, 81.33) * mm});
            skPoint(sketch, "E5.0.41.5", {"position": v(518.34, 93.11) * mm});
            skPoint(sketch, "E5.0.41.6", {"position": v(518.34, 104.9) * mm});
            skPoint(sketch, "E5.0.41.7", {"position": v(518.34, 116.68) * mm});
            skPoint(sketch, "E5.0.41.8", {"position": v(518.34, 128.47) * mm});
            skPoint(sketch, "E5.0.41.9", {"position": v(518.34, 140.25) * mm});
            skPoint(sketch, "E5.0.41.10", {"position": v(518.34, 152.04) * mm});
            skPoint(sketch, "E5.0.41.11", {"position": v(518.34, 163.82) * mm});
            skPoint(sketch, "E5.0.41.12", {"position": v(518.34, 175.6) * mm});
            skPoint(sketch, "E5.0.41.13", {"position": v(518.34, 187.4) * mm});
            skPoint(sketch, "E5.0.41.14", {"position": v(518.34, 199.18) * mm});
            skPoint(sketch, "E5.0.41.15", {"position": v(518.34, 210.97) * mm});
            skPoint(sketch, "E5.0.41.16", {"position": v(518.34, 222.75) * mm});
            skPoint(sketch, "E5.0.41.17", {"position": v(518.34, 234.54) * mm});
            skPoint(sketch, "E5.0.41.18", {"position": v(518.34, 246.32) * mm});
            skPoint(sketch, "E5.0.41.19", {"position": v(518.34, 258.1) * mm});
            skPoint(sketch, "E5.0.41.20", {"position": v(518.34, 269.9) * mm});
            skPoint(sketch, "E5.0.41.21", {"position": v(518.34, 281.68) * mm});
            skPoint(sketch, "E5.0.41.22", {"position": v(518.34, 293.46) * mm});
            skPoint(sketch, "E5.0.41.23", {"position": v(518.34, 305.25) * mm});
            skPoint(sketch, "E5.0.41.24", {"position": v(518.34, 317.03) * mm});
            skPoint(sketch, "E5.0.41.25", {"position": v(518.34, 328.82) * mm});
            skPoint(sketch, "E5.0.41.26", {"position": v(518.34, 340.6) * mm});
            skPoint(sketch, "E5.0.41.27", {"position": v(518.34, 352.39) * mm});
            skPoint(sketch, "E5.0.41.28", {"position": v(518.34, 364.17) * mm});
            skPoint(sketch, "E5.0.41.29", {"position": v(518.34, 375.96) * mm});
            skPoint(sketch, "E5.0.41.30", {"position": v(518.34, 387.74) * mm});
            skPoint(sketch, "E5.0.41.31", {"position": v(518.34, 399.53) * mm});
            skPoint(sketch, "E5.0.41.32", {"position": v(518.34, 411.31) * mm});
            skPoint(sketch, "E5.0.41.33", {"position": v(518.34, 423.1) * mm});
            skPoint(sketch, "E5.0.41.34", {"position": v(518.34, 434.88) * mm});
            skPoint(sketch, "E5.0.41.35", {"position": v(518.34, 446.67) * mm});
            skPoint(sketch, "E5.0.41.36", {"position": v(518.34, 458.45) * mm});
            skPoint(sketch, "E5.0.41.37", {"position": v(518.34, 470.24) * mm});
            skPoint(sketch, "E5.0.41.38", {"position": v(518.34, 482.02) * mm});
            skPoint(sketch, "E5.0.41.39", {"position": v(518.34, 493.8) * mm});
            skPoint(sketch, "E5.0.41.40", {"position": v(518.34, 505.6) * mm});
            skPoint(sketch, "E5.0.41.41", {"position": v(518.34, 517.38) * mm});
            skPoint(sketch, "E5.0.41.42", {"position": v(518.34, 529.16) * mm});
            skPoint(sketch, "E5.0.41.43", {"position": v(518.34, 540.95) * mm});
            skPoint(sketch, "E5.0.41.44", {"position": v(518.34, 552.73) * mm});
            skPoint(sketch, "E5.0.41.45", {"position": v(518.34, 564.52) * mm});
            skPoint(sketch, "E5.0.41.46", {"position": v(518.34, 576.3) * mm});
            skPoint(sketch, "E5.0.41.47", {"position": v(518.34, 588.09) * mm});
            skPoint(sketch, "E5.0.42.0", {"position": v(530.13, 34.19) * mm});
            skPoint(sketch, "E5.0.42.1", {"position": v(530.13, 45.97) * mm});
            skPoint(sketch, "E5.0.42.2", {"position": v(530.13, 57.76) * mm});
            skPoint(sketch, "E5.0.42.3", {"position": v(530.13, 69.54) * mm});
            skPoint(sketch, "E5.0.42.4", {"position": v(530.13, 81.33) * mm});
            skPoint(sketch, "E5.0.42.5", {"position": v(530.13, 93.11) * mm});
            skPoint(sketch, "E5.0.42.6", {"position": v(530.13, 104.9) * mm});
            skPoint(sketch, "E5.0.42.7", {"position": v(530.13, 116.68) * mm});
            skPoint(sketch, "E5.0.42.8", {"position": v(530.13, 128.47) * mm});
            skPoint(sketch, "E5.0.42.9", {"position": v(530.13, 140.25) * mm});
            skPoint(sketch, "E5.0.42.10", {"position": v(530.13, 152.04) * mm});
            skPoint(sketch, "E5.0.42.11", {"position": v(530.13, 163.82) * mm});
            skPoint(sketch, "E5.0.42.12", {"position": v(530.13, 175.6) * mm});
            skPoint(sketch, "E5.0.42.13", {"position": v(530.13, 187.4) * mm});
            skPoint(sketch, "E5.0.42.14", {"position": v(530.13, 199.18) * mm});
            skPoint(sketch, "E5.0.42.15", {"position": v(530.13, 210.97) * mm});
            skPoint(sketch, "E5.0.42.16", {"position": v(530.13, 222.75) * mm});
            skPoint(sketch, "E5.0.42.17", {"position": v(530.13, 234.54) * mm});
            skPoint(sketch, "E5.0.42.18", {"position": v(530.13, 246.32) * mm});
            skPoint(sketch, "E5.0.42.19", {"position": v(530.13, 258.1) * mm});
            skPoint(sketch, "E5.0.42.20", {"position": v(530.13, 269.9) * mm});
            skPoint(sketch, "E5.0.42.21", {"position": v(530.13, 281.68) * mm});
            skPoint(sketch, "E5.0.42.22", {"position": v(530.13, 293.46) * mm});
            skPoint(sketch, "E5.0.42.23", {"position": v(530.13, 305.25) * mm});
            skPoint(sketch, "E5.0.42.24", {"position": v(530.13, 317.03) * mm});
            skPoint(sketch, "E5.0.42.25", {"position": v(530.13, 328.82) * mm});
            skPoint(sketch, "E5.0.42.26", {"position": v(530.13, 340.6) * mm});
            skPoint(sketch, "E5.0.42.27", {"position": v(530.13, 352.39) * mm});
            skPoint(sketch, "E5.0.42.28", {"position": v(530.13, 364.17) * mm});
            skPoint(sketch, "E5.0.42.29", {"position": v(530.13, 375.96) * mm});
            skPoint(sketch, "E5.0.42.30", {"position": v(530.13, 387.74) * mm});
            skPoint(sketch, "E5.0.42.31", {"position": v(530.13, 399.53) * mm});
            skPoint(sketch, "E5.0.42.32", {"position": v(530.13, 411.31) * mm});
            skPoint(sketch, "E5.0.42.33", {"position": v(530.13, 423.1) * mm});
            skPoint(sketch, "E5.0.42.34", {"position": v(530.13, 434.88) * mm});
            skPoint(sketch, "E5.0.42.35", {"position": v(530.13, 446.67) * mm});
            skPoint(sketch, "E5.0.42.36", {"position": v(530.13, 458.45) * mm});
            skPoint(sketch, "E5.0.42.37", {"position": v(530.13, 470.24) * mm});
            skPoint(sketch, "E5.0.42.38", {"position": v(530.13, 482.02) * mm});
            skPoint(sketch, "E5.0.42.39", {"position": v(530.13, 493.8) * mm});
            skPoint(sketch, "E5.0.42.40", {"position": v(530.13, 505.6) * mm});
            skPoint(sketch, "E5.0.42.41", {"position": v(530.13, 517.38) * mm});
            skPoint(sketch, "E5.0.42.42", {"position": v(530.13, 529.16) * mm});
            skPoint(sketch, "E5.0.42.43", {"position": v(530.13, 540.95) * mm});
            skPoint(sketch, "E5.0.42.44", {"position": v(530.13, 552.73) * mm});
            skPoint(sketch, "E5.0.42.45", {"position": v(530.13, 564.52) * mm});
            skPoint(sketch, "E5.0.42.46", {"position": v(530.13, 576.3) * mm});
            skPoint(sketch, "E5.0.42.47", {"position": v(530.13, 588.09) * mm});
            skPoint(sketch, "E5.0.43.0", {"position": v(541.91, 34.19) * mm});
            skPoint(sketch, "E5.0.43.1", {"position": v(541.91, 45.97) * mm});
            skPoint(sketch, "E5.0.43.2", {"position": v(541.91, 57.76) * mm});
            skPoint(sketch, "E5.0.43.3", {"position": v(541.91, 69.54) * mm});
            skPoint(sketch, "E5.0.43.4", {"position": v(541.91, 81.33) * mm});
            skPoint(sketch, "E5.0.43.5", {"position": v(541.91, 93.11) * mm});
            skPoint(sketch, "E5.0.43.6", {"position": v(541.91, 104.9) * mm});
            skPoint(sketch, "E5.0.43.7", {"position": v(541.91, 116.68) * mm});
            skPoint(sketch, "E5.0.43.8", {"position": v(541.91, 128.47) * mm});
            skPoint(sketch, "E5.0.43.9", {"position": v(541.91, 140.25) * mm});
            skPoint(sketch, "E5.0.43.10", {"position": v(541.91, 152.04) * mm});
            skPoint(sketch, "E5.0.43.11", {"position": v(541.91, 163.82) * mm});
            skPoint(sketch, "E5.0.43.12", {"position": v(541.91, 175.6) * mm});
            skPoint(sketch, "E5.0.43.13", {"position": v(541.91, 187.4) * mm});
            skPoint(sketch, "E5.0.43.14", {"position": v(541.91, 199.18) * mm});
            skPoint(sketch, "E5.0.43.15", {"position": v(541.91, 210.97) * mm});
            skPoint(sketch, "E5.0.43.16", {"position": v(541.91, 222.75) * mm});
            skPoint(sketch, "E5.0.43.17", {"position": v(541.91, 234.54) * mm});
            skPoint(sketch, "E5.0.43.18", {"position": v(541.91, 246.32) * mm});
            skPoint(sketch, "E5.0.43.19", {"position": v(541.91, 258.1) * mm});
            skPoint(sketch, "E5.0.43.20", {"position": v(541.91, 269.9) * mm});
            skPoint(sketch, "E5.0.43.21", {"position": v(541.91, 281.68) * mm});
            skPoint(sketch, "E5.0.43.22", {"position": v(541.91, 293.46) * mm});
            skPoint(sketch, "E5.0.43.23", {"position": v(541.91, 305.25) * mm});
            skPoint(sketch, "E5.0.43.24", {"position": v(541.91, 317.03) * mm});
            skPoint(sketch, "E5.0.43.25", {"position": v(541.91, 328.82) * mm});
            skPoint(sketch, "E5.0.43.26", {"position": v(541.91, 340.6) * mm});
            skPoint(sketch, "E5.0.43.27", {"position": v(541.91, 352.39) * mm});
            skPoint(sketch, "E5.0.43.28", {"position": v(541.91, 364.17) * mm});
            skPoint(sketch, "E5.0.43.29", {"position": v(541.91, 375.96) * mm});
            skPoint(sketch, "E5.0.43.30", {"position": v(541.91, 387.74) * mm});
            skPoint(sketch, "E5.0.43.31", {"position": v(541.91, 399.53) * mm});
            skPoint(sketch, "E5.0.43.32", {"position": v(541.91, 411.31) * mm});
            skPoint(sketch, "E5.0.43.33", {"position": v(541.91, 423.1) * mm});
            skPoint(sketch, "E5.0.43.34", {"position": v(541.91, 434.88) * mm});
            skPoint(sketch, "E5.0.43.35", {"position": v(541.91, 446.67) * mm});
            skPoint(sketch, "E5.0.43.36", {"position": v(541.91, 458.45) * mm});
            skPoint(sketch, "E5.0.43.37", {"position": v(541.91, 470.24) * mm});
            skPoint(sketch, "E5.0.43.38", {"position": v(541.91, 482.02) * mm});
            skPoint(sketch, "E5.0.43.39", {"position": v(541.91, 493.8) * mm});
            skPoint(sketch, "E5.0.43.40", {"position": v(541.91, 505.6) * mm});
            skPoint(sketch, "E5.0.43.41", {"position": v(541.91, 517.38) * mm});
            skPoint(sketch, "E5.0.43.42", {"position": v(541.91, 529.16) * mm});
            skPoint(sketch, "E5.0.43.43", {"position": v(541.91, 540.95) * mm});
            skPoint(sketch, "E5.0.43.44", {"position": v(541.91, 552.73) * mm});
            skPoint(sketch, "E5.0.43.45", {"position": v(541.91, 564.52) * mm});
            skPoint(sketch, "E5.0.43.46", {"position": v(541.91, 576.3) * mm});
            skPoint(sketch, "E5.0.43.47", {"position": v(541.91, 588.09) * mm});
            skPoint(sketch, "E5.0.44.0", {"position": v(553.7, 34.19) * mm});
            skPoint(sketch, "E5.0.44.1", {"position": v(553.7, 45.97) * mm});
            skPoint(sketch, "E5.0.44.2", {"position": v(553.7, 57.76) * mm});
            skPoint(sketch, "E5.0.44.3", {"position": v(553.7, 69.54) * mm});
            skPoint(sketch, "E5.0.44.4", {"position": v(553.7, 81.33) * mm});
            skPoint(sketch, "E5.0.44.5", {"position": v(553.7, 93.11) * mm});
            skPoint(sketch, "E5.0.44.6", {"position": v(553.7, 104.9) * mm});
            skPoint(sketch, "E5.0.44.7", {"position": v(553.7, 116.68) * mm});
            skPoint(sketch, "E5.0.44.8", {"position": v(553.7, 128.47) * mm});
            skPoint(sketch, "E5.0.44.9", {"position": v(553.7, 140.25) * mm});
            skPoint(sketch, "E5.0.44.10", {"position": v(553.7, 152.04) * mm});
            skPoint(sketch, "E5.0.44.11", {"position": v(553.7, 163.82) * mm});
            skPoint(sketch, "E5.0.44.12", {"position": v(553.7, 175.6) * mm});
            skPoint(sketch, "E5.0.44.13", {"position": v(553.7, 187.4) * mm});
            skPoint(sketch, "E5.0.44.14", {"position": v(553.7, 199.18) * mm});
            skPoint(sketch, "E5.0.44.15", {"position": v(553.7, 210.97) * mm});
            skPoint(sketch, "E5.0.44.16", {"position": v(553.7, 222.75) * mm});
            skPoint(sketch, "E5.0.44.17", {"position": v(553.7, 234.54) * mm});
            skPoint(sketch, "E5.0.44.18", {"position": v(553.7, 246.32) * mm});
            skPoint(sketch, "E5.0.44.19", {"position": v(553.7, 258.1) * mm});
            skPoint(sketch, "E5.0.44.20", {"position": v(553.7, 269.9) * mm});
            skPoint(sketch, "E5.0.44.21", {"position": v(553.7, 281.68) * mm});
            skPoint(sketch, "E5.0.44.22", {"position": v(553.7, 293.46) * mm});
            skPoint(sketch, "E5.0.44.23", {"position": v(553.7, 305.25) * mm});
            skPoint(sketch, "E5.0.44.24", {"position": v(553.7, 317.03) * mm});
            skPoint(sketch, "E5.0.44.25", {"position": v(553.7, 328.82) * mm});
            skPoint(sketch, "E5.0.44.26", {"position": v(553.7, 340.6) * mm});
            skPoint(sketch, "E5.0.44.27", {"position": v(553.7, 352.39) * mm});
            skPoint(sketch, "E5.0.44.28", {"position": v(553.7, 364.17) * mm});
            skPoint(sketch, "E5.0.44.29", {"position": v(553.7, 375.96) * mm});
            skPoint(sketch, "E5.0.44.30", {"position": v(553.7, 387.74) * mm});
            skPoint(sketch, "E5.0.44.31", {"position": v(553.7, 399.53) * mm});
            skPoint(sketch, "E5.0.44.32", {"position": v(553.7, 411.31) * mm});
            skPoint(sketch, "E5.0.44.33", {"position": v(553.7, 423.1) * mm});
            skPoint(sketch, "E5.0.44.34", {"position": v(553.7, 434.88) * mm});
            skPoint(sketch, "E5.0.44.35", {"position": v(553.7, 446.67) * mm});
            skPoint(sketch, "E5.0.44.36", {"position": v(553.7, 458.45) * mm});
            skPoint(sketch, "E5.0.44.37", {"position": v(553.7, 470.24) * mm});
            skPoint(sketch, "E5.0.44.38", {"position": v(553.7, 482.02) * mm});
            skPoint(sketch, "E5.0.44.39", {"position": v(553.7, 493.8) * mm});
            skPoint(sketch, "E5.0.44.40", {"position": v(553.7, 505.6) * mm});
            skPoint(sketch, "E5.0.44.41", {"position": v(553.7, 517.38) * mm});
            skPoint(sketch, "E5.0.44.42", {"position": v(553.7, 529.16) * mm});
            skPoint(sketch, "E5.0.44.43", {"position": v(553.7, 540.95) * mm});
            skPoint(sketch, "E5.0.44.44", {"position": v(553.7, 552.73) * mm});
            skPoint(sketch, "E5.0.44.45", {"position": v(553.7, 564.52) * mm});
            skPoint(sketch, "E5.0.44.46", {"position": v(553.7, 576.3) * mm});
            skPoint(sketch, "E5.0.44.47", {"position": v(553.7, 588.09) * mm});
            skPoint(sketch, "E5.0.45.0", {"position": v(565.48, 34.19) * mm});
            skPoint(sketch, "E5.0.45.1", {"position": v(565.48, 45.97) * mm});
            skPoint(sketch, "E5.0.45.2", {"position": v(565.48, 57.76) * mm});
            skPoint(sketch, "E5.0.45.3", {"position": v(565.48, 69.54) * mm});
            skPoint(sketch, "E5.0.45.4", {"position": v(565.48, 81.33) * mm});
            skPoint(sketch, "E5.0.45.5", {"position": v(565.48, 93.11) * mm});
            skPoint(sketch, "E5.0.45.6", {"position": v(565.48, 104.9) * mm});
            skPoint(sketch, "E5.0.45.7", {"position": v(565.48, 116.68) * mm});
            skPoint(sketch, "E5.0.45.8", {"position": v(565.48, 128.47) * mm});
            skPoint(sketch, "E5.0.45.9", {"position": v(565.48, 140.25) * mm});
            skPoint(sketch, "E5.0.45.10", {"position": v(565.48, 152.04) * mm});
            skPoint(sketch, "E5.0.45.11", {"position": v(565.48, 163.82) * mm});
            skPoint(sketch, "E5.0.45.12", {"position": v(565.48, 175.6) * mm});
            skPoint(sketch, "E5.0.45.13", {"position": v(565.48, 187.4) * mm});
            skPoint(sketch, "E5.0.45.14", {"position": v(565.48, 199.18) * mm});
            skPoint(sketch, "E5.0.45.15", {"position": v(565.48, 210.97) * mm});
            skPoint(sketch, "E5.0.45.16", {"position": v(565.48, 222.75) * mm});
            skPoint(sketch, "E5.0.45.17", {"position": v(565.48, 234.54) * mm});
            skPoint(sketch, "E5.0.45.18", {"position": v(565.48, 246.32) * mm});
            skPoint(sketch, "E5.0.45.19", {"position": v(565.48, 258.1) * mm});
            skPoint(sketch, "E5.0.45.20", {"position": v(565.48, 269.9) * mm});
            skPoint(sketch, "E5.0.45.21", {"position": v(565.48, 281.68) * mm});
            skPoint(sketch, "E5.0.45.22", {"position": v(565.48, 293.46) * mm});
            skPoint(sketch, "E5.0.45.23", {"position": v(565.48, 305.25) * mm});
            skPoint(sketch, "E5.0.45.24", {"position": v(565.48, 317.03) * mm});
            skPoint(sketch, "E5.0.45.25", {"position": v(565.48, 328.82) * mm});
            skPoint(sketch, "E5.0.45.26", {"position": v(565.48, 340.6) * mm});
            skPoint(sketch, "E5.0.45.27", {"position": v(565.48, 352.39) * mm});
            skPoint(sketch, "E5.0.45.28", {"position": v(565.48, 364.17) * mm});
            skPoint(sketch, "E5.0.45.29", {"position": v(565.48, 375.96) * mm});
            skPoint(sketch, "E5.0.45.30", {"position": v(565.48, 387.74) * mm});
            skPoint(sketch, "E5.0.45.31", {"position": v(565.48, 399.53) * mm});
            skPoint(sketch, "E5.0.45.32", {"position": v(565.48, 411.31) * mm});
            skPoint(sketch, "E5.0.45.33", {"position": v(565.48, 423.1) * mm});
            skPoint(sketch, "E5.0.45.34", {"position": v(565.48, 434.88) * mm});
            skPoint(sketch, "E5.0.45.35", {"position": v(565.48, 446.67) * mm});
            skPoint(sketch, "E5.0.45.36", {"position": v(565.48, 458.45) * mm});
            skPoint(sketch, "E5.0.45.37", {"position": v(565.48, 470.24) * mm});
            skPoint(sketch, "E5.0.45.38", {"position": v(565.48, 482.02) * mm});
            skPoint(sketch, "E5.0.45.39", {"position": v(565.48, 493.8) * mm});
            skPoint(sketch, "E5.0.45.40", {"position": v(565.48, 505.6) * mm});
            skPoint(sketch, "E5.0.45.41", {"position": v(565.48, 517.38) * mm});
            skPoint(sketch, "E5.0.45.42", {"position": v(565.48, 529.16) * mm});
            skPoint(sketch, "E5.0.45.43", {"position": v(565.48, 540.95) * mm});
            skPoint(sketch, "E5.0.45.44", {"position": v(565.48, 552.73) * mm});
            skPoint(sketch, "E5.0.45.45", {"position": v(565.48, 564.52) * mm});
            skPoint(sketch, "E5.0.45.46", {"position": v(565.48, 576.3) * mm});
            skPoint(sketch, "E5.0.45.47", {"position": v(565.48, 588.09) * mm});
            skPoint(sketch, "E5.0.46.0", {"position": v(577.27, 34.19) * mm});
            skPoint(sketch, "E5.0.46.1", {"position": v(577.27, 45.97) * mm});
            skPoint(sketch, "E5.0.46.2", {"position": v(577.27, 57.76) * mm});
            skPoint(sketch, "E5.0.46.3", {"position": v(577.27, 69.54) * mm});
            skPoint(sketch, "E5.0.46.4", {"position": v(577.27, 81.33) * mm});
            skPoint(sketch, "E5.0.46.5", {"position": v(577.27, 93.11) * mm});
            skPoint(sketch, "E5.0.46.6", {"position": v(577.27, 104.9) * mm});
            skPoint(sketch, "E5.0.46.7", {"position": v(577.27, 116.68) * mm});
            skPoint(sketch, "E5.0.46.8", {"position": v(577.27, 128.47) * mm});
            skPoint(sketch, "E5.0.46.9", {"position": v(577.27, 140.25) * mm});
            skPoint(sketch, "E5.0.46.10", {"position": v(577.27, 152.04) * mm});
            skPoint(sketch, "E5.0.46.11", {"position": v(577.27, 163.82) * mm});
            skPoint(sketch, "E5.0.46.12", {"position": v(577.27, 175.6) * mm});
            skPoint(sketch, "E5.0.46.13", {"position": v(577.27, 187.4) * mm});
            skPoint(sketch, "E5.0.46.14", {"position": v(577.27, 199.18) * mm});
            skPoint(sketch, "E5.0.46.15", {"position": v(577.27, 210.97) * mm});
            skPoint(sketch, "E5.0.46.16", {"position": v(577.27, 222.75) * mm});
            skPoint(sketch, "E5.0.46.17", {"position": v(577.27, 234.54) * mm});
            skPoint(sketch, "E5.0.46.18", {"position": v(577.27, 246.32) * mm});
            skPoint(sketch, "E5.0.46.19", {"position": v(577.27, 258.1) * mm});
            skPoint(sketch, "E5.0.46.20", {"position": v(577.27, 269.9) * mm});
            skPoint(sketch, "E5.0.46.21", {"position": v(577.27, 281.68) * mm});
            skPoint(sketch, "E5.0.46.22", {"position": v(577.27, 293.46) * mm});
            skPoint(sketch, "E5.0.46.23", {"position": v(577.27, 305.25) * mm});
            skPoint(sketch, "E5.0.46.24", {"position": v(577.27, 317.03) * mm});
            skPoint(sketch, "E5.0.46.25", {"position": v(577.27, 328.82) * mm});
            skPoint(sketch, "E5.0.46.26", {"position": v(577.27, 340.6) * mm});
            skPoint(sketch, "E5.0.46.27", {"position": v(577.27, 352.39) * mm});
            skPoint(sketch, "E5.0.46.28", {"position": v(577.27, 364.17) * mm});
            skPoint(sketch, "E5.0.46.29", {"position": v(577.27, 375.96) * mm});
            skPoint(sketch, "E5.0.46.30", {"position": v(577.27, 387.74) * mm});
            skPoint(sketch, "E5.0.46.31", {"position": v(577.27, 399.53) * mm});
            skPoint(sketch, "E5.0.46.32", {"position": v(577.27, 411.31) * mm});
            skPoint(sketch, "E5.0.46.33", {"position": v(577.27, 423.1) * mm});
            skPoint(sketch, "E5.0.46.34", {"position": v(577.27, 434.88) * mm});
            skPoint(sketch, "E5.0.46.35", {"position": v(577.27, 446.67) * mm});
            skPoint(sketch, "E5.0.46.36", {"position": v(577.27, 458.45) * mm});
            skPoint(sketch, "E5.0.46.37", {"position": v(577.27, 470.24) * mm});
            skPoint(sketch, "E5.0.46.38", {"position": v(577.27, 482.02) * mm});
            skPoint(sketch, "E5.0.46.39", {"position": v(577.27, 493.8) * mm});
            skPoint(sketch, "E5.0.46.40", {"position": v(577.27, 505.6) * mm});
            skPoint(sketch, "E5.0.46.41", {"position": v(577.27, 517.38) * mm});
            skPoint(sketch, "E5.0.46.42", {"position": v(577.27, 529.16) * mm});
            skPoint(sketch, "E5.0.46.43", {"position": v(577.27, 540.95) * mm});
            skPoint(sketch, "E5.0.46.44", {"position": v(577.27, 552.73) * mm});
            skPoint(sketch, "E5.0.46.45", {"position": v(577.27, 564.52) * mm});
            skPoint(sketch, "E5.0.46.46", {"position": v(577.27, 576.3) * mm});
            skPoint(sketch, "E5.0.46.47", {"position": v(577.27, 588.09) * mm});
            skPoint(sketch, "E5.0.47.0", {"position": v(589.05, 34.19) * mm});
            skPoint(sketch, "E5.0.47.1", {"position": v(589.05, 45.97) * mm});
            skPoint(sketch, "E5.0.47.2", {"position": v(589.05, 57.76) * mm});
            skPoint(sketch, "E5.0.47.3", {"position": v(589.05, 69.54) * mm});
            skPoint(sketch, "E5.0.47.4", {"position": v(589.05, 81.33) * mm});
            skPoint(sketch, "E5.0.47.5", {"position": v(589.05, 93.11) * mm});
            skPoint(sketch, "E5.0.47.6", {"position": v(589.05, 104.9) * mm});
            skPoint(sketch, "E5.0.47.7", {"position": v(589.05, 116.68) * mm});
            skPoint(sketch, "E5.0.47.8", {"position": v(589.05, 128.47) * mm});
            skPoint(sketch, "E5.0.47.9", {"position": v(589.05, 140.25) * mm});
            skPoint(sketch, "E5.0.47.10", {"position": v(589.05, 152.04) * mm});
            skPoint(sketch, "E5.0.47.11", {"position": v(589.05, 163.82) * mm});
            skPoint(sketch, "E5.0.47.12", {"position": v(589.05, 175.6) * mm});
            skPoint(sketch, "E5.0.47.13", {"position": v(589.05, 187.4) * mm});
            skPoint(sketch, "E5.0.47.14", {"position": v(589.05, 199.18) * mm});
            skPoint(sketch, "E5.0.47.15", {"position": v(589.05, 210.97) * mm});
            skPoint(sketch, "E5.0.47.16", {"position": v(589.05, 222.75) * mm});
            skPoint(sketch, "E5.0.47.17", {"position": v(589.05, 234.54) * mm});
            skPoint(sketch, "E5.0.47.18", {"position": v(589.05, 246.32) * mm});
            skPoint(sketch, "E5.0.47.19", {"position": v(589.05, 258.1) * mm});
            skPoint(sketch, "E5.0.47.20", {"position": v(589.05, 269.9) * mm});
            skPoint(sketch, "E5.0.47.21", {"position": v(589.05, 281.68) * mm});
            skPoint(sketch, "E5.0.47.22", {"position": v(589.05, 293.46) * mm});
            skPoint(sketch, "E5.0.47.23", {"position": v(589.05, 305.25) * mm});
            skPoint(sketch, "E5.0.47.24", {"position": v(589.05, 317.03) * mm});
            skPoint(sketch, "E5.0.47.25", {"position": v(589.05, 328.82) * mm});
            skPoint(sketch, "E5.0.47.26", {"position": v(589.05, 340.6) * mm});
            skPoint(sketch, "E5.0.47.27", {"position": v(589.05, 352.39) * mm});
            skPoint(sketch, "E5.0.47.28", {"position": v(589.05, 364.17) * mm});
            skPoint(sketch, "E5.0.47.29", {"position": v(589.05, 375.96) * mm});
            skPoint(sketch, "E5.0.47.30", {"position": v(589.05, 387.74) * mm});
            skPoint(sketch, "E5.0.47.31", {"position": v(589.05, 399.53) * mm});
            skPoint(sketch, "E5.0.47.32", {"position": v(589.05, 411.31) * mm});
            skPoint(sketch, "E5.0.47.33", {"position": v(589.05, 423.1) * mm});
            skPoint(sketch, "E5.0.47.34", {"position": v(589.05, 434.88) * mm});
            skPoint(sketch, "E5.0.47.35", {"position": v(589.05, 446.67) * mm});
            skPoint(sketch, "E5.0.47.36", {"position": v(589.05, 458.45) * mm});
            skPoint(sketch, "E5.0.47.37", {"position": v(589.05, 470.24) * mm});
            skPoint(sketch, "E5.0.47.38", {"position": v(589.05, 482.02) * mm});
            skPoint(sketch, "E5.0.47.39", {"position": v(589.05, 493.8) * mm});
            skPoint(sketch, "E5.0.47.40", {"position": v(589.05, 505.6) * mm});
            skPoint(sketch, "E5.0.47.41", {"position": v(589.05, 517.38) * mm});
            skPoint(sketch, "E5.0.47.42", {"position": v(589.05, 529.16) * mm});
            skPoint(sketch, "E5.0.47.43", {"position": v(589.05, 540.95) * mm});
            skPoint(sketch, "E5.0.47.44", {"position": v(589.05, 552.73) * mm});
            skPoint(sketch, "E5.0.47.45", {"position": v(589.05, 564.52) * mm});
            skPoint(sketch, "E5.0.47.46", {"position": v(589.05, 576.3) * mm});
            skPoint(sketch, "E5.0.47.47", {"position": v(589.05, 588.09) * mm});
            skPoint(sketch, "E5.0.48.0", {"position": v(600.84, 34.19) * mm});
            skPoint(sketch, "E5.0.48.1", {"position": v(600.84, 45.97) * mm});
            skPoint(sketch, "E5.0.48.2", {"position": v(600.84, 57.76) * mm});
            skPoint(sketch, "E5.0.48.3", {"position": v(600.84, 69.54) * mm});
            skPoint(sketch, "E5.0.48.4", {"position": v(600.84, 81.33) * mm});
            skPoint(sketch, "E5.0.48.5", {"position": v(600.84, 93.11) * mm});
            skPoint(sketch, "E5.0.48.6", {"position": v(600.84, 104.9) * mm});
            skPoint(sketch, "E5.0.48.7", {"position": v(600.84, 116.68) * mm});
            skPoint(sketch, "E5.0.48.8", {"position": v(600.84, 128.47) * mm});
            skPoint(sketch, "E5.0.48.9", {"position": v(600.84, 140.25) * mm});
            skPoint(sketch, "E5.0.48.10", {"position": v(600.84, 152.04) * mm});
            skPoint(sketch, "E5.0.48.11", {"position": v(600.84, 163.82) * mm});
            skPoint(sketch, "E5.0.48.12", {"position": v(600.84, 175.6) * mm});
            skPoint(sketch, "E5.0.48.13", {"position": v(600.84, 187.4) * mm});
            skPoint(sketch, "E5.0.48.14", {"position": v(600.84, 199.18) * mm});
            skPoint(sketch, "E5.0.48.15", {"position": v(600.84, 210.97) * mm});
            skPoint(sketch, "E5.0.48.16", {"position": v(600.84, 222.75) * mm});
            skPoint(sketch, "E5.0.48.17", {"position": v(600.84, 234.54) * mm});
            skPoint(sketch, "E5.0.48.18", {"position": v(600.84, 246.32) * mm});
            skPoint(sketch, "E5.0.48.19", {"position": v(600.84, 258.1) * mm});
            skPoint(sketch, "E5.0.48.20", {"position": v(600.84, 269.9) * mm});
            skPoint(sketch, "E5.0.48.21", {"position": v(600.84, 281.68) * mm});
            skPoint(sketch, "E5.0.48.22", {"position": v(600.84, 293.46) * mm});
            skPoint(sketch, "E5.0.48.23", {"position": v(600.84, 305.25) * mm});
            skPoint(sketch, "E5.0.48.24", {"position": v(600.84, 317.03) * mm});
            skPoint(sketch, "E5.0.48.25", {"position": v(600.84, 328.82) * mm});
            skPoint(sketch, "E5.0.48.26", {"position": v(600.84, 340.6) * mm});
            skPoint(sketch, "E5.0.48.27", {"position": v(600.84, 352.39) * mm});
            skPoint(sketch, "E5.0.48.28", {"position": v(600.84, 364.17) * mm});
            skPoint(sketch, "E5.0.48.29", {"position": v(600.84, 375.96) * mm});
            skPoint(sketch, "E5.0.48.30", {"position": v(600.84, 387.74) * mm});
            skPoint(sketch, "E5.0.48.31", {"position": v(600.84, 399.53) * mm});
            skPoint(sketch, "E5.0.48.32", {"position": v(600.84, 411.31) * mm});
            skPoint(sketch, "E5.0.48.33", {"position": v(600.84, 423.1) * mm});
            skPoint(sketch, "E5.0.48.34", {"position": v(600.84, 434.88) * mm});
            skPoint(sketch, "E5.0.48.35", {"position": v(600.84, 446.67) * mm});
            skPoint(sketch, "E5.0.48.36", {"position": v(600.84, 458.45) * mm});
            skPoint(sketch, "E5.0.48.37", {"position": v(600.84, 470.24) * mm});
            skPoint(sketch, "E5.0.48.38", {"position": v(600.84, 482.02) * mm});
            skPoint(sketch, "E5.0.48.39", {"position": v(600.84, 493.8) * mm});
            skPoint(sketch, "E5.0.48.40", {"position": v(600.84, 505.6) * mm});
            skPoint(sketch, "E5.0.48.41", {"position": v(600.84, 517.38) * mm});
            skPoint(sketch, "E5.0.48.42", {"position": v(600.84, 529.16) * mm});
            skPoint(sketch, "E5.0.48.43", {"position": v(600.84, 540.95) * mm});
            skPoint(sketch, "E5.0.48.44", {"position": v(600.84, 552.73) * mm});
            skPoint(sketch, "E5.0.48.45", {"position": v(600.84, 564.52) * mm});
            skPoint(sketch, "E5.0.48.46", {"position": v(600.84, 576.3) * mm});
            skPoint(sketch, "E5.0.48.47", {"position": v(600.84, 588.09) * mm});
            skPoint(sketch, "E5.0.49.0", {"position": v(612.62, 34.19) * mm});
            skPoint(sketch, "E5.0.49.1", {"position": v(612.62, 45.97) * mm});
            skPoint(sketch, "E5.0.49.2", {"position": v(612.62, 57.76) * mm});
            skPoint(sketch, "E5.0.49.3", {"position": v(612.62, 69.54) * mm});
            skPoint(sketch, "E5.0.49.4", {"position": v(612.62, 81.33) * mm});
            skPoint(sketch, "E5.0.49.5", {"position": v(612.62, 93.11) * mm});
            skPoint(sketch, "E5.0.49.6", {"position": v(612.62, 104.9) * mm});
            skPoint(sketch, "E5.0.49.7", {"position": v(612.62, 116.68) * mm});
            skPoint(sketch, "E5.0.49.8", {"position": v(612.62, 128.47) * mm});
            skPoint(sketch, "E5.0.49.9", {"position": v(612.62, 140.25) * mm});
            skPoint(sketch, "E5.0.49.10", {"position": v(612.62, 152.04) * mm});
            skPoint(sketch, "E5.0.49.11", {"position": v(612.62, 163.82) * mm});
            skPoint(sketch, "E5.0.49.12", {"position": v(612.62, 175.6) * mm});
            skPoint(sketch, "E5.0.49.13", {"position": v(612.62, 187.4) * mm});
            skPoint(sketch, "E5.0.49.14", {"position": v(612.62, 199.18) * mm});
            skPoint(sketch, "E5.0.49.15", {"position": v(612.62, 210.97) * mm});
            skPoint(sketch, "E5.0.49.16", {"position": v(612.62, 222.75) * mm});
            skPoint(sketch, "E5.0.49.17", {"position": v(612.62, 234.54) * mm});
            skPoint(sketch, "E5.0.49.18", {"position": v(612.62, 246.32) * mm});
            skPoint(sketch, "E5.0.49.19", {"position": v(612.62, 258.1) * mm});
            skPoint(sketch, "E5.0.49.20", {"position": v(612.62, 269.9) * mm});
            skPoint(sketch, "E5.0.49.21", {"position": v(612.62, 281.68) * mm});
            skPoint(sketch, "E5.0.49.22", {"position": v(612.62, 293.46) * mm});
            skPoint(sketch, "E5.0.49.23", {"position": v(612.62, 305.25) * mm});
            skPoint(sketch, "E5.0.49.24", {"position": v(612.62, 317.03) * mm});
            skPoint(sketch, "E5.0.49.25", {"position": v(612.62, 328.82) * mm});
            skPoint(sketch, "E5.0.49.26", {"position": v(612.62, 340.6) * mm});
            skPoint(sketch, "E5.0.49.27", {"position": v(612.62, 352.39) * mm});
            skPoint(sketch, "E5.0.49.28", {"position": v(612.62, 364.17) * mm});
            skPoint(sketch, "E5.0.49.29", {"position": v(612.62, 375.96) * mm});
            skPoint(sketch, "E5.0.49.30", {"position": v(612.62, 387.74) * mm});
            skPoint(sketch, "E5.0.49.31", {"position": v(612.62, 399.53) * mm});
            skPoint(sketch, "E5.0.49.32", {"position": v(612.62, 411.31) * mm});
            skPoint(sketch, "E5.0.49.33", {"position": v(612.62, 423.1) * mm});
            skPoint(sketch, "E5.0.49.34", {"position": v(612.62, 434.88) * mm});
            skPoint(sketch, "E5.0.49.35", {"position": v(612.62, 446.67) * mm});
            skPoint(sketch, "E5.0.49.36", {"position": v(612.62, 458.45) * mm});
            skPoint(sketch, "E5.0.49.37", {"position": v(612.62, 470.24) * mm});
            skPoint(sketch, "E5.0.49.38", {"position": v(612.62, 482.02) * mm});
            skPoint(sketch, "E5.0.49.39", {"position": v(612.62, 493.8) * mm});
            skPoint(sketch, "E5.0.49.40", {"position": v(612.62, 505.6) * mm});
            skPoint(sketch, "E5.0.49.41", {"position": v(612.62, 517.38) * mm});
            skPoint(sketch, "E5.0.49.42", {"position": v(612.62, 529.16) * mm});
            skPoint(sketch, "E5.0.49.43", {"position": v(612.62, 540.95) * mm});
            skPoint(sketch, "E5.0.49.44", {"position": v(612.62, 552.73) * mm});
            skPoint(sketch, "E5.0.49.45", {"position": v(612.62, 564.52) * mm});
            skPoint(sketch, "E5.0.49.46", {"position": v(612.62, 576.3) * mm});
            skPoint(sketch, "E5.0.49.47", {"position": v(612.62, 588.09) * mm});
            skPoint(sketch, "E5.0.50.0", {"position": v(624.4, 34.19) * mm});
            skPoint(sketch, "E5.0.50.1", {"position": v(624.4, 45.97) * mm});
            skPoint(sketch, "E5.0.50.2", {"position": v(624.4, 57.76) * mm});
            skPoint(sketch, "E5.0.50.3", {"position": v(624.4, 69.54) * mm});
            skPoint(sketch, "E5.0.50.4", {"position": v(624.4, 81.33) * mm});
            skPoint(sketch, "E5.0.50.5", {"position": v(624.4, 93.11) * mm});
            skPoint(sketch, "E5.0.50.6", {"position": v(624.4, 104.9) * mm});
            skPoint(sketch, "E5.0.50.7", {"position": v(624.4, 116.68) * mm});
            skPoint(sketch, "E5.0.50.8", {"position": v(624.4, 128.47) * mm});
            skPoint(sketch, "E5.0.50.9", {"position": v(624.4, 140.25) * mm});
            skPoint(sketch, "E5.0.50.10", {"position": v(624.4, 152.04) * mm});
            skPoint(sketch, "E5.0.50.11", {"position": v(624.4, 163.82) * mm});
            skPoint(sketch, "E5.0.50.12", {"position": v(624.4, 175.6) * mm});
            skPoint(sketch, "E5.0.50.13", {"position": v(624.4, 187.4) * mm});
            skPoint(sketch, "E5.0.50.14", {"position": v(624.4, 199.18) * mm});
            skPoint(sketch, "E5.0.50.15", {"position": v(624.4, 210.97) * mm});
            skPoint(sketch, "E5.0.50.16", {"position": v(624.4, 222.75) * mm});
            skPoint(sketch, "E5.0.50.17", {"position": v(624.4, 234.54) * mm});
            skPoint(sketch, "E5.0.50.18", {"position": v(624.4, 246.32) * mm});
            skPoint(sketch, "E5.0.50.19", {"position": v(624.4, 258.1) * mm});
            skPoint(sketch, "E5.0.50.20", {"position": v(624.4, 269.9) * mm});
            skPoint(sketch, "E5.0.50.21", {"position": v(624.4, 281.68) * mm});
            skPoint(sketch, "E5.0.50.22", {"position": v(624.4, 293.46) * mm});
            skPoint(sketch, "E5.0.50.23", {"position": v(624.4, 305.25) * mm});
            skPoint(sketch, "E5.0.50.24", {"position": v(624.4, 317.03) * mm});
            skPoint(sketch, "E5.0.50.25", {"position": v(624.4, 328.82) * mm});
            skPoint(sketch, "E5.0.50.26", {"position": v(624.4, 340.6) * mm});
            skPoint(sketch, "E5.0.50.27", {"position": v(624.4, 352.39) * mm});
            skPoint(sketch, "E5.0.50.28", {"position": v(624.4, 364.17) * mm});
            skPoint(sketch, "E5.0.50.29", {"position": v(624.4, 375.96) * mm});
            skPoint(sketch, "E5.0.50.30", {"position": v(624.4, 387.74) * mm});
            skPoint(sketch, "E5.0.50.31", {"position": v(624.4, 399.53) * mm});
            skPoint(sketch, "E5.0.50.32", {"position": v(624.4, 411.31) * mm});
            skPoint(sketch, "E5.0.50.33", {"position": v(624.4, 423.1) * mm});
            skPoint(sketch, "E5.0.50.34", {"position": v(624.4, 434.88) * mm});
            skPoint(sketch, "E5.0.50.35", {"position": v(624.4, 446.67) * mm});
            skPoint(sketch, "E5.0.50.36", {"position": v(624.4, 458.45) * mm});
            skPoint(sketch, "E5.0.50.37", {"position": v(624.4, 470.24) * mm});
            skPoint(sketch, "E5.0.50.38", {"position": v(624.4, 482.02) * mm});
            skPoint(sketch, "E5.0.50.39", {"position": v(624.4, 493.8) * mm});
            skPoint(sketch, "E5.0.50.40", {"position": v(624.4, 505.6) * mm});
            skPoint(sketch, "E5.0.50.41", {"position": v(624.4, 517.38) * mm});
            skPoint(sketch, "E5.0.50.42", {"position": v(624.4, 529.16) * mm});
            skPoint(sketch, "E5.0.50.43", {"position": v(624.4, 540.95) * mm});
            skPoint(sketch, "E5.0.50.44", {"position": v(624.4, 552.73) * mm});
            skPoint(sketch, "E5.0.50.45", {"position": v(624.4, 564.52) * mm});
            skPoint(sketch, "E5.0.50.46", {"position": v(624.4, 576.3) * mm});
            skPoint(sketch, "E5.0.50.47", {"position": v(624.4, 588.09) * mm});
            skPoint(sketch, "E5.0.51.0", {"position": v(636.2, 34.19) * mm});
            skPoint(sketch, "E5.0.51.1", {"position": v(636.2, 45.97) * mm});
            skPoint(sketch, "E5.0.51.2", {"position": v(636.2, 57.76) * mm});
            skPoint(sketch, "E5.0.51.3", {"position": v(636.2, 69.54) * mm});
            skPoint(sketch, "E5.0.51.4", {"position": v(636.2, 81.33) * mm});
            skPoint(sketch, "E5.0.51.5", {"position": v(636.2, 93.11) * mm});
            skPoint(sketch, "E5.0.51.6", {"position": v(636.2, 104.9) * mm});
            skPoint(sketch, "E5.0.51.7", {"position": v(636.2, 116.68) * mm});
            skPoint(sketch, "E5.0.51.8", {"position": v(636.2, 128.47) * mm});
            skPoint(sketch, "E5.0.51.9", {"position": v(636.2, 140.25) * mm});
            skPoint(sketch, "E5.0.51.10", {"position": v(636.2, 152.04) * mm});
            skPoint(sketch, "E5.0.51.11", {"position": v(636.2, 163.82) * mm});
            skPoint(sketch, "E5.0.51.12", {"position": v(636.2, 175.6) * mm});
            skPoint(sketch, "E5.0.51.13", {"position": v(636.2, 187.4) * mm});
            skPoint(sketch, "E5.0.51.14", {"position": v(636.2, 199.18) * mm});
            skPoint(sketch, "E5.0.51.15", {"position": v(636.2, 210.97) * mm});
            skPoint(sketch, "E5.0.51.16", {"position": v(636.2, 222.75) * mm});
            skPoint(sketch, "E5.0.51.17", {"position": v(636.2, 234.54) * mm});
            skPoint(sketch, "E5.0.51.18", {"position": v(636.2, 246.32) * mm});
            skPoint(sketch, "E5.0.51.19", {"position": v(636.2, 258.1) * mm});
            skPoint(sketch, "E5.0.51.20", {"position": v(636.2, 269.9) * mm});
            skPoint(sketch, "E5.0.51.21", {"position": v(636.2, 281.68) * mm});
            skPoint(sketch, "E5.0.51.22", {"position": v(636.2, 293.46) * mm});
            skPoint(sketch, "E5.0.51.23", {"position": v(636.2, 305.25) * mm});
            skPoint(sketch, "E5.0.51.24", {"position": v(636.2, 317.03) * mm});
            skPoint(sketch, "E5.0.51.25", {"position": v(636.2, 328.82) * mm});
            skPoint(sketch, "E5.0.51.26", {"position": v(636.2, 340.6) * mm});
            skPoint(sketch, "E5.0.51.27", {"position": v(636.2, 352.39) * mm});
            skPoint(sketch, "E5.0.51.28", {"position": v(636.2, 364.17) * mm});
            skPoint(sketch, "E5.0.51.29", {"position": v(636.2, 375.96) * mm});
            skPoint(sketch, "E5.0.51.30", {"position": v(636.2, 387.74) * mm});
            skPoint(sketch, "E5.0.51.31", {"position": v(636.2, 399.53) * mm});
            skPoint(sketch, "E5.0.51.32", {"position": v(636.2, 411.31) * mm});
            skPoint(sketch, "E5.0.51.33", {"position": v(636.2, 423.1) * mm});
            skPoint(sketch, "E5.0.51.34", {"position": v(636.2, 434.88) * mm});
            skPoint(sketch, "E5.0.51.35", {"position": v(636.2, 446.67) * mm});
            skPoint(sketch, "E5.0.51.36", {"position": v(636.2, 458.45) * mm});
            skPoint(sketch, "E5.0.51.37", {"position": v(636.2, 470.24) * mm});
            skPoint(sketch, "E5.0.51.38", {"position": v(636.2, 482.02) * mm});
            skPoint(sketch, "E5.0.51.39", {"position": v(636.2, 493.8) * mm});
            skPoint(sketch, "E5.0.51.40", {"position": v(636.2, 505.6) * mm});
            skPoint(sketch, "E5.0.51.41", {"position": v(636.2, 517.38) * mm});
            skPoint(sketch, "E5.0.51.42", {"position": v(636.2, 529.16) * mm});
            skPoint(sketch, "E5.0.51.43", {"position": v(636.2, 540.95) * mm});
            skPoint(sketch, "E5.0.51.44", {"position": v(636.2, 552.73) * mm});
            skPoint(sketch, "E5.0.51.45", {"position": v(636.2, 564.52) * mm});
            skPoint(sketch, "E5.0.51.46", {"position": v(636.2, 576.3) * mm});
            skPoint(sketch, "E5.0.51.47", {"position": v(636.2, 588.09) * mm});
            skPoint(sketch, "E5.0.52.0", {"position": v(647.98, 34.19) * mm});
            skPoint(sketch, "E5.0.52.1", {"position": v(647.98, 45.97) * mm});
            skPoint(sketch, "E5.0.52.2", {"position": v(647.98, 57.76) * mm});
            skPoint(sketch, "E5.0.52.3", {"position": v(647.98, 69.54) * mm});
            skPoint(sketch, "E5.0.52.4", {"position": v(647.98, 81.33) * mm});
            skPoint(sketch, "E5.0.52.5", {"position": v(647.98, 93.11) * mm});
            skPoint(sketch, "E5.0.52.6", {"position": v(647.98, 104.9) * mm});
            skPoint(sketch, "E5.0.52.7", {"position": v(647.98, 116.68) * mm});
            skPoint(sketch, "E5.0.52.8", {"position": v(647.98, 128.47) * mm});
            skPoint(sketch, "E5.0.52.9", {"position": v(647.98, 140.25) * mm});
            skPoint(sketch, "E5.0.52.10", {"position": v(647.98, 152.04) * mm});
            skPoint(sketch, "E5.0.52.11", {"position": v(647.98, 163.82) * mm});
            skPoint(sketch, "E5.0.52.12", {"position": v(647.98, 175.6) * mm});
            skPoint(sketch, "E5.0.52.13", {"position": v(647.98, 187.4) * mm});
            skPoint(sketch, "E5.0.52.14", {"position": v(647.98, 199.18) * mm});
            skPoint(sketch, "E5.0.52.15", {"position": v(647.98, 210.97) * mm});
            skPoint(sketch, "E5.0.52.16", {"position": v(647.98, 222.75) * mm});
            skPoint(sketch, "E5.0.52.17", {"position": v(647.98, 234.54) * mm});
            skPoint(sketch, "E5.0.52.18", {"position": v(647.98, 246.32) * mm});
            skPoint(sketch, "E5.0.52.19", {"position": v(647.98, 258.1) * mm});
            skPoint(sketch, "E5.0.52.20", {"position": v(647.98, 269.9) * mm});
            skPoint(sketch, "E5.0.52.21", {"position": v(647.98, 281.68) * mm});
            skPoint(sketch, "E5.0.52.22", {"position": v(647.98, 293.46) * mm});
            skPoint(sketch, "E5.0.52.23", {"position": v(647.98, 305.25) * mm});
            skPoint(sketch, "E5.0.52.24", {"position": v(647.98, 317.03) * mm});
            skPoint(sketch, "E5.0.52.25", {"position": v(647.98, 328.82) * mm});
            skPoint(sketch, "E5.0.52.26", {"position": v(647.98, 340.6) * mm});
            skPoint(sketch, "E5.0.52.27", {"position": v(647.98, 352.39) * mm});
            skPoint(sketch, "E5.0.52.28", {"position": v(647.98, 364.17) * mm});
            skPoint(sketch, "E5.0.52.29", {"position": v(647.98, 375.96) * mm});
            skPoint(sketch, "E5.0.52.30", {"position": v(647.98, 387.74) * mm});
            skPoint(sketch, "E5.0.52.31", {"position": v(647.98, 399.53) * mm});
            skPoint(sketch, "E5.0.52.32", {"position": v(647.98, 411.31) * mm});
            skPoint(sketch, "E5.0.52.33", {"position": v(647.98, 423.1) * mm});
            skPoint(sketch, "E5.0.52.34", {"position": v(647.98, 434.88) * mm});
            skPoint(sketch, "E5.0.52.35", {"position": v(647.98, 446.67) * mm});
            skPoint(sketch, "E5.0.52.36", {"position": v(647.98, 458.45) * mm});
            skPoint(sketch, "E5.0.52.37", {"position": v(647.98, 470.24) * mm});
            skPoint(sketch, "E5.0.52.38", {"position": v(647.98, 482.02) * mm});
            skPoint(sketch, "E5.0.52.39", {"position": v(647.98, 493.8) * mm});
            skPoint(sketch, "E5.0.52.40", {"position": v(647.98, 505.6) * mm});
            skPoint(sketch, "E5.0.52.41", {"position": v(647.98, 517.38) * mm});
            skPoint(sketch, "E5.0.52.42", {"position": v(647.98, 529.16) * mm});
            skPoint(sketch, "E5.0.52.43", {"position": v(647.98, 540.95) * mm});
            skPoint(sketch, "E5.0.52.44", {"position": v(647.98, 552.73) * mm});
            skPoint(sketch, "E5.0.52.45", {"position": v(647.98, 564.52) * mm});
            skPoint(sketch, "E5.0.52.46", {"position": v(647.98, 576.3) * mm});
            skPoint(sketch, "E5.0.52.47", {"position": v(647.98, 588.09) * mm});
            skPoint(sketch, "E5.0.53.0", {"position": v(659.76, 34.19) * mm});
            skPoint(sketch, "E5.0.53.1", {"position": v(659.76, 45.97) * mm});
            skPoint(sketch, "E5.0.53.2", {"position": v(659.76, 57.76) * mm});
            skPoint(sketch, "E5.0.53.3", {"position": v(659.76, 69.54) * mm});
            skPoint(sketch, "E5.0.53.4", {"position": v(659.76, 81.33) * mm});
            skPoint(sketch, "E5.0.53.5", {"position": v(659.76, 93.11) * mm});
            skPoint(sketch, "E5.0.53.6", {"position": v(659.76, 104.9) * mm});
            skPoint(sketch, "E5.0.53.7", {"position": v(659.76, 116.68) * mm});
            skPoint(sketch, "E5.0.53.8", {"position": v(659.76, 128.47) * mm});
            skPoint(sketch, "E5.0.53.9", {"position": v(659.76, 140.25) * mm});
            skPoint(sketch, "E5.0.53.10", {"position": v(659.76, 152.04) * mm});
            skPoint(sketch, "E5.0.53.11", {"position": v(659.76, 163.82) * mm});
            skPoint(sketch, "E5.0.53.12", {"position": v(659.76, 175.6) * mm});
            skPoint(sketch, "E5.0.53.13", {"position": v(659.76, 187.4) * mm});
            skPoint(sketch, "E5.0.53.14", {"position": v(659.76, 199.18) * mm});
            skPoint(sketch, "E5.0.53.15", {"position": v(659.76, 210.97) * mm});
            skPoint(sketch, "E5.0.53.16", {"position": v(659.76, 222.75) * mm});
            skPoint(sketch, "E5.0.53.17", {"position": v(659.76, 234.54) * mm});
            skPoint(sketch, "E5.0.53.18", {"position": v(659.76, 246.32) * mm});
            skPoint(sketch, "E5.0.53.19", {"position": v(659.76, 258.1) * mm});
            skPoint(sketch, "E5.0.53.20", {"position": v(659.76, 269.9) * mm});
            skPoint(sketch, "E5.0.53.21", {"position": v(659.76, 281.68) * mm});
            skPoint(sketch, "E5.0.53.22", {"position": v(659.76, 293.46) * mm});
            skPoint(sketch, "E5.0.53.23", {"position": v(659.76, 305.25) * mm});
            skPoint(sketch, "E5.0.53.24", {"position": v(659.76, 317.03) * mm});
            skPoint(sketch, "E5.0.53.25", {"position": v(659.76, 328.82) * mm});
            skPoint(sketch, "E5.0.53.26", {"position": v(659.76, 340.6) * mm});
            skPoint(sketch, "E5.0.53.27", {"position": v(659.76, 352.39) * mm});
            skPoint(sketch, "E5.0.53.28", {"position": v(659.76, 364.17) * mm});
            skPoint(sketch, "E5.0.53.29", {"position": v(659.76, 375.96) * mm});
            skPoint(sketch, "E5.0.53.30", {"position": v(659.76, 387.74) * mm});
            skPoint(sketch, "E5.0.53.31", {"position": v(659.76, 399.53) * mm});
            skPoint(sketch, "E5.0.53.32", {"position": v(659.76, 411.31) * mm});
            skPoint(sketch, "E5.0.53.33", {"position": v(659.76, 423.1) * mm});
            skPoint(sketch, "E5.0.53.34", {"position": v(659.76, 434.88) * mm});
            skPoint(sketch, "E5.0.53.35", {"position": v(659.76, 446.67) * mm});
            skPoint(sketch, "E5.0.53.36", {"position": v(659.76, 458.45) * mm});
            skPoint(sketch, "E5.0.53.37", {"position": v(659.76, 470.24) * mm});
            skPoint(sketch, "E5.0.53.38", {"position": v(659.76, 482.02) * mm});
            skPoint(sketch, "E5.0.53.39", {"position": v(659.76, 493.8) * mm});
            skPoint(sketch, "E5.0.53.40", {"position": v(659.76, 505.6) * mm});
            skPoint(sketch, "E5.0.53.41", {"position": v(659.76, 517.38) * mm});
            skPoint(sketch, "E5.0.53.42", {"position": v(659.76, 529.16) * mm});
            skPoint(sketch, "E5.0.53.43", {"position": v(659.76, 540.95) * mm});
            skPoint(sketch, "E5.0.53.44", {"position": v(659.76, 552.73) * mm});
            skPoint(sketch, "E5.0.53.45", {"position": v(659.76, 564.52) * mm});
            skPoint(sketch, "E5.0.53.46", {"position": v(659.76, 576.3) * mm});
            skPoint(sketch, "E5.0.53.47", {"position": v(659.76, 588.09) * mm});
            skPoint(sketch, "E5.0.54.0", {"position": v(671.55, 34.19) * mm});
            skPoint(sketch, "E5.0.54.1", {"position": v(671.55, 45.97) * mm});
            skPoint(sketch, "E5.0.54.2", {"position": v(671.55, 57.76) * mm});
            skPoint(sketch, "E5.0.54.3", {"position": v(671.55, 69.54) * mm});
            skPoint(sketch, "E5.0.54.4", {"position": v(671.55, 81.33) * mm});
            skPoint(sketch, "E5.0.54.5", {"position": v(671.55, 93.11) * mm});
            skPoint(sketch, "E5.0.54.6", {"position": v(671.55, 104.9) * mm});
            skPoint(sketch, "E5.0.54.7", {"position": v(671.55, 116.68) * mm});
            skPoint(sketch, "E5.0.54.8", {"position": v(671.55, 128.47) * mm});
            skPoint(sketch, "E5.0.54.9", {"position": v(671.55, 140.25) * mm});
            skPoint(sketch, "E5.0.54.10", {"position": v(671.55, 152.04) * mm});
            skPoint(sketch, "E5.0.54.11", {"position": v(671.55, 163.82) * mm});
            skPoint(sketch, "E5.0.54.12", {"position": v(671.55, 175.6) * mm});
            skPoint(sketch, "E5.0.54.13", {"position": v(671.55, 187.4) * mm});
            skPoint(sketch, "E5.0.54.14", {"position": v(671.55, 199.18) * mm});
            skPoint(sketch, "E5.0.54.15", {"position": v(671.55, 210.97) * mm});
            skPoint(sketch, "E5.0.54.16", {"position": v(671.55, 222.75) * mm});
            skPoint(sketch, "E5.0.54.17", {"position": v(671.55, 234.54) * mm});
            skPoint(sketch, "E5.0.54.18", {"position": v(671.55, 246.32) * mm});
            skPoint(sketch, "E5.0.54.19", {"position": v(671.55, 258.1) * mm});
            skPoint(sketch, "E5.0.54.20", {"position": v(671.55, 269.9) * mm});
            skPoint(sketch, "E5.0.54.21", {"position": v(671.55, 281.68) * mm});
            skPoint(sketch, "E5.0.54.22", {"position": v(671.55, 293.46) * mm});
            skPoint(sketch, "E5.0.54.23", {"position": v(671.55, 305.25) * mm});
            skPoint(sketch, "E5.0.54.24", {"position": v(671.55, 317.03) * mm});
            skPoint(sketch, "E5.0.54.25", {"position": v(671.55, 328.82) * mm});
            skPoint(sketch, "E5.0.54.26", {"position": v(671.55, 340.6) * mm});
            skPoint(sketch, "E5.0.54.27", {"position": v(671.55, 352.39) * mm});
            skPoint(sketch, "E5.0.54.28", {"position": v(671.55, 364.17) * mm});
            skPoint(sketch, "E5.0.54.29", {"position": v(671.55, 375.96) * mm});
            skPoint(sketch, "E5.0.54.30", {"position": v(671.55, 387.74) * mm});
            skPoint(sketch, "E5.0.54.31", {"position": v(671.55, 399.53) * mm});
            skPoint(sketch, "E5.0.54.32", {"position": v(671.55, 411.31) * mm});
            skPoint(sketch, "E5.0.54.33", {"position": v(671.55, 423.1) * mm});
            skPoint(sketch, "E5.0.54.34", {"position": v(671.55, 434.88) * mm});
            skPoint(sketch, "E5.0.54.35", {"position": v(671.55, 446.67) * mm});
            skPoint(sketch, "E5.0.54.36", {"position": v(671.55, 458.45) * mm});
            skPoint(sketch, "E5.0.54.37", {"position": v(671.55, 470.24) * mm});
            skPoint(sketch, "E5.0.54.38", {"position": v(671.55, 482.02) * mm});
            skPoint(sketch, "E5.0.54.39", {"position": v(671.55, 493.8) * mm});
            skPoint(sketch, "E5.0.54.40", {"position": v(671.55, 505.6) * mm});
            skPoint(sketch, "E5.0.54.41", {"position": v(671.55, 517.38) * mm});
            skPoint(sketch, "E5.0.54.42", {"position": v(671.55, 529.16) * mm});
            skPoint(sketch, "E5.0.54.43", {"position": v(671.55, 540.95) * mm});
            skPoint(sketch, "E5.0.54.44", {"position": v(671.55, 552.73) * mm});
            skPoint(sketch, "E5.0.54.45", {"position": v(671.55, 564.52) * mm});
            skPoint(sketch, "E5.0.54.46", {"position": v(671.55, 576.3) * mm});
            skPoint(sketch, "E5.0.54.47", {"position": v(671.55, 588.09) * mm});
            skPoint(sketch, "E5.0.55.0", {"position": v(683.33, 34.19) * mm});
            skPoint(sketch, "E5.0.55.1", {"position": v(683.33, 45.97) * mm});
            skPoint(sketch, "E5.0.55.2", {"position": v(683.33, 57.76) * mm});
            skPoint(sketch, "E5.0.55.3", {"position": v(683.33, 69.54) * mm});
            skPoint(sketch, "E5.0.55.4", {"position": v(683.33, 81.33) * mm});
            skPoint(sketch, "E5.0.55.5", {"position": v(683.33, 93.11) * mm});
            skPoint(sketch, "E5.0.55.6", {"position": v(683.33, 104.9) * mm});
            skPoint(sketch, "E5.0.55.7", {"position": v(683.33, 116.68) * mm});
            skPoint(sketch, "E5.0.55.8", {"position": v(683.33, 128.47) * mm});
            skPoint(sketch, "E5.0.55.9", {"position": v(683.33, 140.25) * mm});
            skPoint(sketch, "E5.0.55.10", {"position": v(683.33, 152.04) * mm});
            skPoint(sketch, "E5.0.55.11", {"position": v(683.33, 163.82) * mm});
            skPoint(sketch, "E5.0.55.12", {"position": v(683.33, 175.6) * mm});
            skPoint(sketch, "E5.0.55.13", {"position": v(683.33, 187.4) * mm});
            skPoint(sketch, "E5.0.55.14", {"position": v(683.33, 199.18) * mm});
            skPoint(sketch, "E5.0.55.15", {"position": v(683.33, 210.97) * mm});
            skPoint(sketch, "E5.0.55.16", {"position": v(683.33, 222.75) * mm});
            skPoint(sketch, "E5.0.55.17", {"position": v(683.33, 234.54) * mm});
            skPoint(sketch, "E5.0.55.18", {"position": v(683.33, 246.32) * mm});
            skPoint(sketch, "E5.0.55.19", {"position": v(683.33, 258.1) * mm});
            skPoint(sketch, "E5.0.55.20", {"position": v(683.33, 269.9) * mm});
            skPoint(sketch, "E5.0.55.21", {"position": v(683.33, 281.68) * mm});
            skPoint(sketch, "E5.0.55.22", {"position": v(683.33, 293.46) * mm});
            skPoint(sketch, "E5.0.55.23", {"position": v(683.33, 305.25) * mm});
            skPoint(sketch, "E5.0.55.24", {"position": v(683.33, 317.03) * mm});
            skPoint(sketch, "E5.0.55.25", {"position": v(683.33, 328.82) * mm});
            skPoint(sketch, "E5.0.55.26", {"position": v(683.33, 340.6) * mm});
            skPoint(sketch, "E5.0.55.27", {"position": v(683.33, 352.39) * mm});
            skPoint(sketch, "E5.0.55.28", {"position": v(683.33, 364.17) * mm});
            skPoint(sketch, "E5.0.55.29", {"position": v(683.33, 375.96) * mm});
            skPoint(sketch, "E5.0.55.30", {"position": v(683.33, 387.74) * mm});
            skPoint(sketch, "E5.0.55.31", {"position": v(683.33, 399.53) * mm});
            skPoint(sketch, "E5.0.55.32", {"position": v(683.33, 411.31) * mm});
            skPoint(sketch, "E5.0.55.33", {"position": v(683.33, 423.1) * mm});
            skPoint(sketch, "E5.0.55.34", {"position": v(683.33, 434.88) * mm});
            skPoint(sketch, "E5.0.55.35", {"position": v(683.33, 446.67) * mm});
            skPoint(sketch, "E5.0.55.36", {"position": v(683.33, 458.45) * mm});
            skPoint(sketch, "E5.0.55.37", {"position": v(683.33, 470.24) * mm});
            skPoint(sketch, "E5.0.55.38", {"position": v(683.33, 482.02) * mm});
            skPoint(sketch, "E5.0.55.39", {"position": v(683.33, 493.8) * mm});
            skPoint(sketch, "E5.0.55.40", {"position": v(683.33, 505.6) * mm});
            skPoint(sketch, "E5.0.55.41", {"position": v(683.33, 517.38) * mm});
            skPoint(sketch, "E5.0.55.42", {"position": v(683.33, 529.16) * mm});
            skPoint(sketch, "E5.0.55.43", {"position": v(683.33, 540.95) * mm});
            skPoint(sketch, "E5.0.55.44", {"position": v(683.33, 552.73) * mm});
            skPoint(sketch, "E5.0.55.45", {"position": v(683.33, 564.52) * mm});
            skPoint(sketch, "E5.0.55.46", {"position": v(683.33, 576.3) * mm});
            skPoint(sketch, "E5.0.55.47", {"position": v(683.33, 588.09) * mm});
            skPoint(sketch, "E5.0.56.0", {"position": v(695.12, 34.19) * mm});
            skPoint(sketch, "E5.0.56.1", {"position": v(695.12, 45.97) * mm});
            skPoint(sketch, "E5.0.56.2", {"position": v(695.12, 57.76) * mm});
            skPoint(sketch, "E5.0.56.3", {"position": v(695.12, 69.54) * mm});
            skPoint(sketch, "E5.0.56.4", {"position": v(695.12, 81.33) * mm});
            skPoint(sketch, "E5.0.56.5", {"position": v(695.12, 93.11) * mm});
            skPoint(sketch, "E5.0.56.6", {"position": v(695.12, 104.9) * mm});
            skPoint(sketch, "E5.0.56.7", {"position": v(695.12, 116.68) * mm});
            skPoint(sketch, "E5.0.56.8", {"position": v(695.12, 128.47) * mm});
            skPoint(sketch, "E5.0.56.9", {"position": v(695.12, 140.25) * mm});
            skPoint(sketch, "E5.0.56.10", {"position": v(695.12, 152.04) * mm});
            skPoint(sketch, "E5.0.56.11", {"position": v(695.12, 163.82) * mm});
            skPoint(sketch, "E5.0.56.12", {"position": v(695.12, 175.6) * mm});
            skPoint(sketch, "E5.0.56.13", {"position": v(695.12, 187.4) * mm});
            skPoint(sketch, "E5.0.56.14", {"position": v(695.12, 199.18) * mm});
            skPoint(sketch, "E5.0.56.15", {"position": v(695.12, 210.97) * mm});
            skPoint(sketch, "E5.0.56.16", {"position": v(695.12, 222.75) * mm});
            skPoint(sketch, "E5.0.56.17", {"position": v(695.12, 234.54) * mm});
            skPoint(sketch, "E5.0.56.18", {"position": v(695.12, 246.32) * mm});
            skPoint(sketch, "E5.0.56.19", {"position": v(695.12, 258.1) * mm});
            skPoint(sketch, "E5.0.56.20", {"position": v(695.12, 269.9) * mm});
            skPoint(sketch, "E5.0.56.21", {"position": v(695.12, 281.68) * mm});
            skPoint(sketch, "E5.0.56.22", {"position": v(695.12, 293.46) * mm});
            skPoint(sketch, "E5.0.56.23", {"position": v(695.12, 305.25) * mm});
            skPoint(sketch, "E5.0.56.24", {"position": v(695.12, 317.03) * mm});
            skPoint(sketch, "E5.0.56.25", {"position": v(695.12, 328.82) * mm});
            skPoint(sketch, "E5.0.56.26", {"position": v(695.12, 340.6) * mm});
            skPoint(sketch, "E5.0.56.27", {"position": v(695.12, 352.39) * mm});
            skPoint(sketch, "E5.0.56.28", {"position": v(695.12, 364.17) * mm});
            skPoint(sketch, "E5.0.56.29", {"position": v(695.12, 375.96) * mm});
            skPoint(sketch, "E5.0.56.30", {"position": v(695.12, 387.74) * mm});
            skPoint(sketch, "E5.0.56.31", {"position": v(695.12, 399.53) * mm});
            skPoint(sketch, "E5.0.56.32", {"position": v(695.12, 411.31) * mm});
            skPoint(sketch, "E5.0.56.33", {"position": v(695.12, 423.1) * mm});
            skPoint(sketch, "E5.0.56.34", {"position": v(695.12, 434.88) * mm});
            skPoint(sketch, "E5.0.56.35", {"position": v(695.12, 446.67) * mm});
            skPoint(sketch, "E5.0.56.36", {"position": v(695.12, 458.45) * mm});
            skPoint(sketch, "E5.0.56.37", {"position": v(695.12, 470.24) * mm});
            skPoint(sketch, "E5.0.56.38", {"position": v(695.12, 482.02) * mm});
            skPoint(sketch, "E5.0.56.39", {"position": v(695.12, 493.8) * mm});
            skPoint(sketch, "E5.0.56.40", {"position": v(695.12, 505.6) * mm});
            skPoint(sketch, "E5.0.56.41", {"position": v(695.12, 517.38) * mm});
            skPoint(sketch, "E5.0.56.42", {"position": v(695.12, 529.16) * mm});
            skPoint(sketch, "E5.0.56.43", {"position": v(695.12, 540.95) * mm});
            skPoint(sketch, "E5.0.56.44", {"position": v(695.12, 552.73) * mm});
            skPoint(sketch, "E5.0.56.45", {"position": v(695.12, 564.52) * mm});
            skPoint(sketch, "E5.0.56.46", {"position": v(695.12, 576.3) * mm});
            skPoint(sketch, "E5.0.56.47", {"position": v(695.12, 588.09) * mm});
            skPoint(sketch, "E5.0.57.0", {"position": v(706.9, 34.19) * mm});
            skPoint(sketch, "E5.0.57.1", {"position": v(706.9, 45.97) * mm});
            skPoint(sketch, "E5.0.57.2", {"position": v(706.9, 57.76) * mm});
            skPoint(sketch, "E5.0.57.3", {"position": v(706.9, 69.54) * mm});
            skPoint(sketch, "E5.0.57.4", {"position": v(706.9, 81.33) * mm});
            skPoint(sketch, "E5.0.57.5", {"position": v(706.9, 93.11) * mm});
            skPoint(sketch, "E5.0.57.6", {"position": v(706.9, 104.9) * mm});
            skPoint(sketch, "E5.0.57.7", {"position": v(706.9, 116.68) * mm});
            skPoint(sketch, "E5.0.57.8", {"position": v(706.9, 128.47) * mm});
            skPoint(sketch, "E5.0.57.9", {"position": v(706.9, 140.25) * mm});
            skPoint(sketch, "E5.0.57.10", {"position": v(706.9, 152.04) * mm});
            skPoint(sketch, "E5.0.57.11", {"position": v(706.9, 163.82) * mm});
            skPoint(sketch, "E5.0.57.12", {"position": v(706.9, 175.6) * mm});
            skPoint(sketch, "E5.0.57.13", {"position": v(706.9, 187.4) * mm});
            skPoint(sketch, "E5.0.57.14", {"position": v(706.9, 199.18) * mm});
            skPoint(sketch, "E5.0.57.15", {"position": v(706.9, 210.97) * mm});
            skPoint(sketch, "E5.0.57.16", {"position": v(706.9, 222.75) * mm});
            skPoint(sketch, "E5.0.57.17", {"position": v(706.9, 234.54) * mm});
            skPoint(sketch, "E5.0.57.18", {"position": v(706.9, 246.32) * mm});
            skPoint(sketch, "E5.0.57.19", {"position": v(706.9, 258.1) * mm});
            skPoint(sketch, "E5.0.57.20", {"position": v(706.9, 269.9) * mm});
            skPoint(sketch, "E5.0.57.21", {"position": v(706.9, 281.68) * mm});
            skPoint(sketch, "E5.0.57.22", {"position": v(706.9, 293.46) * mm});
            skPoint(sketch, "E5.0.57.23", {"position": v(706.9, 305.25) * mm});
            skPoint(sketch, "E5.0.57.24", {"position": v(706.9, 317.03) * mm});
            skPoint(sketch, "E5.0.57.25", {"position": v(706.9, 328.82) * mm});
            skPoint(sketch, "E5.0.57.26", {"position": v(706.9, 340.6) * mm});
            skPoint(sketch, "E5.0.57.27", {"position": v(706.9, 352.39) * mm});
            skPoint(sketch, "E5.0.57.28", {"position": v(706.9, 364.17) * mm});
            skPoint(sketch, "E5.0.57.29", {"position": v(706.9, 375.96) * mm});
            skPoint(sketch, "E5.0.57.30", {"position": v(706.9, 387.74) * mm});
            skPoint(sketch, "E5.0.57.31", {"position": v(706.9, 399.53) * mm});
            skPoint(sketch, "E5.0.57.32", {"position": v(706.9, 411.31) * mm});
            skPoint(sketch, "E5.0.57.33", {"position": v(706.9, 423.1) * mm});
            skPoint(sketch, "E5.0.57.34", {"position": v(706.9, 434.88) * mm});
            skPoint(sketch, "E5.0.57.35", {"position": v(706.9, 446.67) * mm});
            skPoint(sketch, "E5.0.57.36", {"position": v(706.9, 458.45) * mm});
            skPoint(sketch, "E5.0.57.37", {"position": v(706.9, 470.24) * mm});
            skPoint(sketch, "E5.0.57.38", {"position": v(706.9, 482.02) * mm});
            skPoint(sketch, "E5.0.57.39", {"position": v(706.9, 493.8) * mm});
            skPoint(sketch, "E5.0.57.40", {"position": v(706.9, 505.6) * mm});
            skPoint(sketch, "E5.0.57.41", {"position": v(706.9, 517.38) * mm});
            skPoint(sketch, "E5.0.57.42", {"position": v(706.9, 529.16) * mm});
            skPoint(sketch, "E5.0.57.43", {"position": v(706.9, 540.95) * mm});
            skPoint(sketch, "E5.0.57.44", {"position": v(706.9, 552.73) * mm});
            skPoint(sketch, "E5.0.57.45", {"position": v(706.9, 564.52) * mm});
            skPoint(sketch, "E5.0.57.46", {"position": v(706.9, 576.3) * mm});
            skPoint(sketch, "E5.0.57.47", {"position": v(706.9, 588.09) * mm});
            skPoint(sketch, "E5.0.58.0", {"position": v(718.7, 34.19) * mm});
            skPoint(sketch, "E5.0.58.1", {"position": v(718.7, 45.97) * mm});
            skPoint(sketch, "E5.0.58.2", {"position": v(718.7, 57.76) * mm});
            skPoint(sketch, "E5.0.58.3", {"position": v(718.7, 69.54) * mm});
            skPoint(sketch, "E5.0.58.4", {"position": v(718.7, 81.33) * mm});
            skPoint(sketch, "E5.0.58.5", {"position": v(718.7, 93.11) * mm});
            skPoint(sketch, "E5.0.58.6", {"position": v(718.7, 104.9) * mm});
            skPoint(sketch, "E5.0.58.7", {"position": v(718.7, 116.68) * mm});
            skPoint(sketch, "E5.0.58.8", {"position": v(718.7, 128.47) * mm});
            skPoint(sketch, "E5.0.58.9", {"position": v(718.7, 140.25) * mm});
            skPoint(sketch, "E5.0.58.10", {"position": v(718.7, 152.04) * mm});
            skPoint(sketch, "E5.0.58.11", {"position": v(718.7, 163.82) * mm});
            skPoint(sketch, "E5.0.58.12", {"position": v(718.7, 175.6) * mm});
            skPoint(sketch, "E5.0.58.13", {"position": v(718.7, 187.4) * mm});
            skPoint(sketch, "E5.0.58.14", {"position": v(718.7, 199.18) * mm});
            skPoint(sketch, "E5.0.58.15", {"position": v(718.7, 210.97) * mm});
            skPoint(sketch, "E5.0.58.16", {"position": v(718.7, 222.75) * mm});
            skPoint(sketch, "E5.0.58.17", {"position": v(718.7, 234.54) * mm});
            skPoint(sketch, "E5.0.58.18", {"position": v(718.7, 246.32) * mm});
            skPoint(sketch, "E5.0.58.19", {"position": v(718.7, 258.1) * mm});
            skPoint(sketch, "E5.0.58.20", {"position": v(718.7, 269.9) * mm});
            skPoint(sketch, "E5.0.58.21", {"position": v(718.7, 281.68) * mm});
            skPoint(sketch, "E5.0.58.22", {"position": v(718.7, 293.46) * mm});
            skPoint(sketch, "E5.0.58.23", {"position": v(718.7, 305.25) * mm});
            skPoint(sketch, "E5.0.58.24", {"position": v(718.7, 317.03) * mm});
            skPoint(sketch, "E5.0.58.25", {"position": v(718.7, 328.82) * mm});
            skPoint(sketch, "E5.0.58.26", {"position": v(718.7, 340.6) * mm});
            skPoint(sketch, "E5.0.58.27", {"position": v(718.7, 352.39) * mm});
            skPoint(sketch, "E5.0.58.28", {"position": v(718.7, 364.17) * mm});
            skPoint(sketch, "E5.0.58.29", {"position": v(718.7, 375.96) * mm});
            skPoint(sketch, "E5.0.58.30", {"position": v(718.7, 387.74) * mm});
            skPoint(sketch, "E5.0.58.31", {"position": v(718.7, 399.53) * mm});
            skPoint(sketch, "E5.0.58.32", {"position": v(718.7, 411.31) * mm});
            skPoint(sketch, "E5.0.58.33", {"position": v(718.7, 423.1) * mm});
            skPoint(sketch, "E5.0.58.34", {"position": v(718.7, 434.88) * mm});
            skPoint(sketch, "E5.0.58.35", {"position": v(718.7, 446.67) * mm});
            skPoint(sketch, "E5.0.58.36", {"position": v(718.7, 458.45) * mm});
            skPoint(sketch, "E5.0.58.37", {"position": v(718.7, 470.24) * mm});
            skPoint(sketch, "E5.0.58.38", {"position": v(718.7, 482.02) * mm});
            skPoint(sketch, "E5.0.58.39", {"position": v(718.7, 493.8) * mm});
            skPoint(sketch, "E5.0.58.40", {"position": v(718.7, 505.6) * mm});
            skPoint(sketch, "E5.0.58.41", {"position": v(718.7, 517.38) * mm});
            skPoint(sketch, "E5.0.58.42", {"position": v(718.7, 529.16) * mm});
            skPoint(sketch, "E5.0.58.43", {"position": v(718.7, 540.95) * mm});
            skPoint(sketch, "E5.0.58.44", {"position": v(718.7, 552.73) * mm});
            skPoint(sketch, "E5.0.58.45", {"position": v(718.7, 564.52) * mm});
            skPoint(sketch, "E5.0.58.46", {"position": v(718.7, 576.3) * mm});
            skPoint(sketch, "E5.0.58.47", {"position": v(718.7, 588.09) * mm});
            skPoint(sketch, "E5.0.59.0", {"position": v(730.48, 34.19) * mm});
            skPoint(sketch, "E5.0.59.1", {"position": v(730.48, 45.97) * mm});
            skPoint(sketch, "E5.0.59.2", {"position": v(730.48, 57.76) * mm});
            skPoint(sketch, "E5.0.59.3", {"position": v(730.48, 69.54) * mm});
            skPoint(sketch, "E5.0.59.4", {"position": v(730.48, 81.33) * mm});
            skPoint(sketch, "E5.0.59.5", {"position": v(730.48, 93.11) * mm});
            skPoint(sketch, "E5.0.59.6", {"position": v(730.48, 104.9) * mm});
            skPoint(sketch, "E5.0.59.7", {"position": v(730.48, 116.68) * mm});
            skPoint(sketch, "E5.0.59.8", {"position": v(730.48, 128.47) * mm});
            skPoint(sketch, "E5.0.59.9", {"position": v(730.48, 140.25) * mm});
            skPoint(sketch, "E5.0.59.10", {"position": v(730.48, 152.04) * mm});
            skPoint(sketch, "E5.0.59.11", {"position": v(730.48, 163.82) * mm});
            skPoint(sketch, "E5.0.59.12", {"position": v(730.48, 175.6) * mm});
            skPoint(sketch, "E5.0.59.13", {"position": v(730.48, 187.4) * mm});
            skPoint(sketch, "E5.0.59.14", {"position": v(730.48, 199.18) * mm});
            skPoint(sketch, "E5.0.59.15", {"position": v(730.48, 210.97) * mm});
            skPoint(sketch, "E5.0.59.16", {"position": v(730.48, 222.75) * mm});
            skPoint(sketch, "E5.0.59.17", {"position": v(730.48, 234.54) * mm});
            skPoint(sketch, "E5.0.59.18", {"position": v(730.48, 246.32) * mm});
            skPoint(sketch, "E5.0.59.19", {"position": v(730.48, 258.1) * mm});
            skPoint(sketch, "E5.0.59.20", {"position": v(730.48, 269.9) * mm});
            skPoint(sketch, "E5.0.59.21", {"position": v(730.48, 281.68) * mm});
            skPoint(sketch, "E5.0.59.22", {"position": v(730.48, 293.46) * mm});
            skPoint(sketch, "E5.0.59.23", {"position": v(730.48, 305.25) * mm});
            skPoint(sketch, "E5.0.59.24", {"position": v(730.48, 317.03) * mm});
            skPoint(sketch, "E5.0.59.25", {"position": v(730.48, 328.82) * mm});
            skPoint(sketch, "E5.0.59.26", {"position": v(730.48, 340.6) * mm});
            skPoint(sketch, "E5.0.59.27", {"position": v(730.48, 352.39) * mm});
            skPoint(sketch, "E5.0.59.28", {"position": v(730.48, 364.17) * mm});
            skPoint(sketch, "E5.0.59.29", {"position": v(730.48, 375.96) * mm});
            skPoint(sketch, "E5.0.59.30", {"position": v(730.48, 387.74) * mm});
            skPoint(sketch, "E5.0.59.31", {"position": v(730.48, 399.53) * mm});
            skPoint(sketch, "E5.0.59.32", {"position": v(730.48, 411.31) * mm});
            skPoint(sketch, "E5.0.59.33", {"position": v(730.48, 423.1) * mm});
            skPoint(sketch, "E5.0.59.34", {"position": v(730.48, 434.88) * mm});
            skPoint(sketch, "E5.0.59.35", {"position": v(730.48, 446.67) * mm});
            skPoint(sketch, "E5.0.59.36", {"position": v(730.48, 458.45) * mm});
            skPoint(sketch, "E5.0.59.37", {"position": v(730.48, 470.24) * mm});
            skPoint(sketch, "E5.0.59.38", {"position": v(730.48, 482.02) * mm});
            skPoint(sketch, "E5.0.59.39", {"position": v(730.48, 493.8) * mm});
            skPoint(sketch, "E5.0.59.40", {"position": v(730.48, 505.6) * mm});
            skPoint(sketch, "E5.0.59.41", {"position": v(730.48, 517.38) * mm});
            skPoint(sketch, "E5.0.59.42", {"position": v(730.48, 529.16) * mm});
            skPoint(sketch, "E5.0.59.43", {"position": v(730.48, 540.95) * mm});
            skPoint(sketch, "E5.0.59.44", {"position": v(730.48, 552.73) * mm});
            skPoint(sketch, "E5.0.59.45", {"position": v(730.48, 564.52) * mm});
            skPoint(sketch, "E5.0.59.46", {"position": v(730.48, 576.3) * mm});
            skPoint(sketch, "E5.0.59.47", {"position": v(730.48, 588.09) * mm});
            skPoint(sketch, "E5.0.60.0", {"position": v(742.26, 34.19) * mm});
            skPoint(sketch, "E5.0.60.1", {"position": v(742.26, 45.97) * mm});
            skPoint(sketch, "E5.0.60.2", {"position": v(742.26, 57.76) * mm});
            skPoint(sketch, "E5.0.60.3", {"position": v(742.26, 69.54) * mm});
            skPoint(sketch, "E5.0.60.4", {"position": v(742.26, 81.33) * mm});
            skPoint(sketch, "E5.0.60.5", {"position": v(742.26, 93.11) * mm});
            skPoint(sketch, "E5.0.60.6", {"position": v(742.26, 104.9) * mm});
            skPoint(sketch, "E5.0.60.7", {"position": v(742.26, 116.68) * mm});
            skPoint(sketch, "E5.0.60.8", {"position": v(742.26, 128.47) * mm});
            skPoint(sketch, "E5.0.60.9", {"position": v(742.26, 140.25) * mm});
            skPoint(sketch, "E5.0.60.10", {"position": v(742.26, 152.04) * mm});
            skPoint(sketch, "E5.0.60.11", {"position": v(742.26, 163.82) * mm});
            skPoint(sketch, "E5.0.60.12", {"position": v(742.26, 175.6) * mm});
            skPoint(sketch, "E5.0.60.13", {"position": v(742.26, 187.4) * mm});
            skPoint(sketch, "E5.0.60.14", {"position": v(742.26, 199.18) * mm});
            skPoint(sketch, "E5.0.60.15", {"position": v(742.26, 210.97) * mm});
            skPoint(sketch, "E5.0.60.16", {"position": v(742.26, 222.75) * mm});
            skPoint(sketch, "E5.0.60.17", {"position": v(742.26, 234.54) * mm});
            skPoint(sketch, "E5.0.60.18", {"position": v(742.26, 246.32) * mm});
            skPoint(sketch, "E5.0.60.19", {"position": v(742.26, 258.1) * mm});
            skPoint(sketch, "E5.0.60.20", {"position": v(742.26, 269.9) * mm});
            skPoint(sketch, "E5.0.60.21", {"position": v(742.26, 281.68) * mm});
            skPoint(sketch, "E5.0.60.22", {"position": v(742.26, 293.46) * mm});
            skPoint(sketch, "E5.0.60.23", {"position": v(742.26, 305.25) * mm});
            skPoint(sketch, "E5.0.60.24", {"position": v(742.26, 317.03) * mm});
            skPoint(sketch, "E5.0.60.25", {"position": v(742.26, 328.82) * mm});
            skPoint(sketch, "E5.0.60.26", {"position": v(742.26, 340.6) * mm});
            skPoint(sketch, "E5.0.60.27", {"position": v(742.26, 352.39) * mm});
            skPoint(sketch, "E5.0.60.28", {"position": v(742.26, 364.17) * mm});
            skPoint(sketch, "E5.0.60.29", {"position": v(742.26, 375.96) * mm});
            skPoint(sketch, "E5.0.60.30", {"position": v(742.26, 387.74) * mm});
            skPoint(sketch, "E5.0.60.31", {"position": v(742.26, 399.53) * mm});
            skPoint(sketch, "E5.0.60.32", {"position": v(742.26, 411.31) * mm});
            skPoint(sketch, "E5.0.60.33", {"position": v(742.26, 423.1) * mm});
            skPoint(sketch, "E5.0.60.34", {"position": v(742.26, 434.88) * mm});
            skPoint(sketch, "E5.0.60.35", {"position": v(742.26, 446.67) * mm});
            skPoint(sketch, "E5.0.60.36", {"position": v(742.26, 458.45) * mm});
            skPoint(sketch, "E5.0.60.37", {"position": v(742.26, 470.24) * mm});
            skPoint(sketch, "E5.0.60.38", {"position": v(742.26, 482.02) * mm});
            skPoint(sketch, "E5.0.60.39", {"position": v(742.26, 493.8) * mm});
            skPoint(sketch, "E5.0.60.40", {"position": v(742.26, 505.6) * mm});
            skPoint(sketch, "E5.0.60.41", {"position": v(742.26, 517.38) * mm});
            skPoint(sketch, "E5.0.60.42", {"position": v(742.26, 529.16) * mm});
            skPoint(sketch, "E5.0.60.43", {"position": v(742.26, 540.95) * mm});
            skPoint(sketch, "E5.0.60.44", {"position": v(742.26, 552.73) * mm});
            skPoint(sketch, "E5.0.60.45", {"position": v(742.26, 564.52) * mm});
            skPoint(sketch, "E5.0.60.46", {"position": v(742.26, 576.3) * mm});
            skPoint(sketch, "E5.0.60.47", {"position": v(742.26, 588.09) * mm});
            skPoint(sketch, "E5.0.61.0", {"position": v(754.05, 34.19) * mm});
            skPoint(sketch, "E5.0.61.1", {"position": v(754.05, 45.97) * mm});
            skPoint(sketch, "E5.0.61.2", {"position": v(754.05, 57.76) * mm});
            skPoint(sketch, "E5.0.61.3", {"position": v(754.05, 69.54) * mm});
            skPoint(sketch, "E5.0.61.4", {"position": v(754.05, 81.33) * mm});
            skPoint(sketch, "E5.0.61.5", {"position": v(754.05, 93.11) * mm});
            skPoint(sketch, "E5.0.61.6", {"position": v(754.05, 104.9) * mm});
            skPoint(sketch, "E5.0.61.7", {"position": v(754.05, 116.68) * mm});
            skPoint(sketch, "E5.0.61.8", {"position": v(754.05, 128.47) * mm});
            skPoint(sketch, "E5.0.61.9", {"position": v(754.05, 140.25) * mm});
            skPoint(sketch, "E5.0.61.10", {"position": v(754.05, 152.04) * mm});
            skPoint(sketch, "E5.0.61.11", {"position": v(754.05, 163.82) * mm});
            skPoint(sketch, "E5.0.61.12", {"position": v(754.05, 175.6) * mm});
            skPoint(sketch, "E5.0.61.13", {"position": v(754.05, 187.4) * mm});
            skPoint(sketch, "E5.0.61.14", {"position": v(754.05, 199.18) * mm});
            skPoint(sketch, "E5.0.61.15", {"position": v(754.05, 210.97) * mm});
            skPoint(sketch, "E5.0.61.16", {"position": v(754.05, 222.75) * mm});
            skPoint(sketch, "E5.0.61.17", {"position": v(754.05, 234.54) * mm});
            skPoint(sketch, "E5.0.61.18", {"position": v(754.05, 246.32) * mm});
            skPoint(sketch, "E5.0.61.19", {"position": v(754.05, 258.1) * mm});
            skPoint(sketch, "E5.0.61.20", {"position": v(754.05, 269.9) * mm});
            skPoint(sketch, "E5.0.61.21", {"position": v(754.05, 281.68) * mm});
            skPoint(sketch, "E5.0.61.22", {"position": v(754.05, 293.46) * mm});
            skPoint(sketch, "E5.0.61.23", {"position": v(754.05, 305.25) * mm});
            skPoint(sketch, "E5.0.61.24", {"position": v(754.05, 317.03) * mm});
            skPoint(sketch, "E5.0.61.25", {"position": v(754.05, 328.82) * mm});
            skPoint(sketch, "E5.0.61.26", {"position": v(754.05, 340.6) * mm});
            skPoint(sketch, "E5.0.61.27", {"position": v(754.05, 352.39) * mm});
            skPoint(sketch, "E5.0.61.28", {"position": v(754.05, 364.17) * mm});
            skPoint(sketch, "E5.0.61.29", {"position": v(754.05, 375.96) * mm});
            skPoint(sketch, "E5.0.61.30", {"position": v(754.05, 387.74) * mm});
            skPoint(sketch, "E5.0.61.31", {"position": v(754.05, 399.53) * mm});
            skPoint(sketch, "E5.0.61.32", {"position": v(754.05, 411.31) * mm});
            skPoint(sketch, "E5.0.61.33", {"position": v(754.05, 423.1) * mm});
            skPoint(sketch, "E5.0.61.34", {"position": v(754.05, 434.88) * mm});
            skPoint(sketch, "E5.0.61.35", {"position": v(754.05, 446.67) * mm});
            skPoint(sketch, "E5.0.61.36", {"position": v(754.05, 458.45) * mm});
            skPoint(sketch, "E5.0.61.37", {"position": v(754.05, 470.24) * mm});
            skPoint(sketch, "E5.0.61.38", {"position": v(754.05, 482.02) * mm});
            skPoint(sketch, "E5.0.61.39", {"position": v(754.05, 493.8) * mm});
            skPoint(sketch, "E5.0.61.40", {"position": v(754.05, 505.6) * mm});
            skPoint(sketch, "E5.0.61.41", {"position": v(754.05, 517.38) * mm});
            skPoint(sketch, "E5.0.61.42", {"position": v(754.05, 529.16) * mm});
            skPoint(sketch, "E5.0.61.43", {"position": v(754.05, 540.95) * mm});
            skPoint(sketch, "E5.0.61.44", {"position": v(754.05, 552.73) * mm});
            skPoint(sketch, "E5.0.61.45", {"position": v(754.05, 564.52) * mm});
            skPoint(sketch, "E5.0.61.46", {"position": v(754.05, 576.3) * mm});
            skPoint(sketch, "E5.0.61.47", {"position": v(754.05, 588.09) * mm});
            skPoint(sketch, "E5.0.62.0", {"position": v(765.83, 34.19) * mm});
            skPoint(sketch, "E5.0.62.1", {"position": v(765.83, 45.97) * mm});
            skPoint(sketch, "E5.0.62.2", {"position": v(765.83, 57.76) * mm});
            skPoint(sketch, "E5.0.62.3", {"position": v(765.83, 69.54) * mm});
            skPoint(sketch, "E5.0.62.4", {"position": v(765.83, 81.33) * mm});
            skPoint(sketch, "E5.0.62.5", {"position": v(765.83, 93.11) * mm});
            skPoint(sketch, "E5.0.62.6", {"position": v(765.83, 104.9) * mm});
            skPoint(sketch, "E5.0.62.7", {"position": v(765.83, 116.68) * mm});
            skPoint(sketch, "E5.0.62.8", {"position": v(765.83, 128.47) * mm});
            skPoint(sketch, "E5.0.62.9", {"position": v(765.83, 140.25) * mm});
            skPoint(sketch, "E5.0.62.10", {"position": v(765.83, 152.04) * mm});
            skPoint(sketch, "E5.0.62.11", {"position": v(765.83, 163.82) * mm});
            skPoint(sketch, "E5.0.62.12", {"position": v(765.83, 175.6) * mm});
            skPoint(sketch, "E5.0.62.13", {"position": v(765.83, 187.4) * mm});
            skPoint(sketch, "E5.0.62.14", {"position": v(765.83, 199.18) * mm});
            skPoint(sketch, "E5.0.62.15", {"position": v(765.83, 210.97) * mm});
            skPoint(sketch, "E5.0.62.16", {"position": v(765.83, 222.75) * mm});
            skPoint(sketch, "E5.0.62.17", {"position": v(765.83, 234.54) * mm});
            skPoint(sketch, "E5.0.62.18", {"position": v(765.83, 246.32) * mm});
            skPoint(sketch, "E5.0.62.19", {"position": v(765.83, 258.1) * mm});
            skPoint(sketch, "E5.0.62.20", {"position": v(765.83, 269.9) * mm});
            skPoint(sketch, "E5.0.62.21", {"position": v(765.83, 281.68) * mm});
            skPoint(sketch, "E5.0.62.22", {"position": v(765.83, 293.46) * mm});
            skPoint(sketch, "E5.0.62.23", {"position": v(765.83, 305.25) * mm});
            skPoint(sketch, "E5.0.62.24", {"position": v(765.83, 317.03) * mm});
            skPoint(sketch, "E5.0.62.25", {"position": v(765.83, 328.82) * mm});
            skPoint(sketch, "E5.0.62.26", {"position": v(765.83, 340.6) * mm});
            skPoint(sketch, "E5.0.62.27", {"position": v(765.83, 352.39) * mm});
            skPoint(sketch, "E5.0.62.28", {"position": v(765.83, 364.17) * mm});
            skPoint(sketch, "E5.0.62.29", {"position": v(765.83, 375.96) * mm});
            skPoint(sketch, "E5.0.62.30", {"position": v(765.83, 387.74) * mm});
            skPoint(sketch, "E5.0.62.31", {"position": v(765.83, 399.53) * mm});
            skPoint(sketch, "E5.0.62.32", {"position": v(765.83, 411.31) * mm});
            skPoint(sketch, "E5.0.62.33", {"position": v(765.83, 423.1) * mm});
            skPoint(sketch, "E5.0.62.34", {"position": v(765.83, 434.88) * mm});
            skPoint(sketch, "E5.0.62.35", {"position": v(765.83, 446.67) * mm});
            skPoint(sketch, "E5.0.62.36", {"position": v(765.83, 458.45) * mm});
            skPoint(sketch, "E5.0.62.37", {"position": v(765.83, 470.24) * mm});
            skPoint(sketch, "E5.0.62.38", {"position": v(765.83, 482.02) * mm});
            skPoint(sketch, "E5.0.62.39", {"position": v(765.83, 493.8) * mm});
            skPoint(sketch, "E5.0.62.40", {"position": v(765.83, 505.6) * mm});
            skPoint(sketch, "E5.0.62.41", {"position": v(765.83, 517.38) * mm});
            skPoint(sketch, "E5.0.62.42", {"position": v(765.83, 529.16) * mm});
            skPoint(sketch, "E5.0.62.43", {"position": v(765.83, 540.95) * mm});
            skPoint(sketch, "E5.0.62.44", {"position": v(765.83, 552.73) * mm});
            skPoint(sketch, "E5.0.62.45", {"position": v(765.83, 564.52) * mm});
            skPoint(sketch, "E5.0.62.46", {"position": v(765.83, 576.3) * mm});
            skPoint(sketch, "E5.0.62.47", {"position": v(765.83, 588.09) * mm});
            skPoint(sketch, "E5.0.63.0", {"position": v(777.62, 34.19) * mm});
            skPoint(sketch, "E5.0.63.1", {"position": v(777.62, 45.97) * mm});
            skPoint(sketch, "E5.0.63.2", {"position": v(777.62, 57.76) * mm});
            skPoint(sketch, "E5.0.63.3", {"position": v(777.62, 69.54) * mm});
            skPoint(sketch, "E5.0.63.4", {"position": v(777.62, 81.33) * mm});
            skPoint(sketch, "E5.0.63.5", {"position": v(777.62, 93.11) * mm});
            skPoint(sketch, "E5.0.63.6", {"position": v(777.62, 104.9) * mm});
            skPoint(sketch, "E5.0.63.7", {"position": v(777.62, 116.68) * mm});
            skPoint(sketch, "E5.0.63.8", {"position": v(777.62, 128.47) * mm});
            skPoint(sketch, "E5.0.63.9", {"position": v(777.62, 140.25) * mm});
            skPoint(sketch, "E5.0.63.10", {"position": v(777.62, 152.04) * mm});
            skPoint(sketch, "E5.0.63.11", {"position": v(777.62, 163.82) * mm});
            skPoint(sketch, "E5.0.63.12", {"position": v(777.62, 175.6) * mm});
            skPoint(sketch, "E5.0.63.13", {"position": v(777.62, 187.4) * mm});
            skPoint(sketch, "E5.0.63.14", {"position": v(777.62, 199.18) * mm});
            skPoint(sketch, "E5.0.63.15", {"position": v(777.62, 210.97) * mm});
            skPoint(sketch, "E5.0.63.16", {"position": v(777.62, 222.75) * mm});
            skPoint(sketch, "E5.0.63.17", {"position": v(777.62, 234.54) * mm});
            skPoint(sketch, "E5.0.63.18", {"position": v(777.62, 246.32) * mm});
            skPoint(sketch, "E5.0.63.19", {"position": v(777.62, 258.1) * mm});
            skPoint(sketch, "E5.0.63.20", {"position": v(777.62, 269.9) * mm});
            skPoint(sketch, "E5.0.63.21", {"position": v(777.62, 281.68) * mm});
            skPoint(sketch, "E5.0.63.22", {"position": v(777.62, 293.46) * mm});
            skPoint(sketch, "E5.0.63.23", {"position": v(777.62, 305.25) * mm});
            skPoint(sketch, "E5.0.63.24", {"position": v(777.62, 317.03) * mm});
            skPoint(sketch, "E5.0.63.25", {"position": v(777.62, 328.82) * mm});
            skPoint(sketch, "E5.0.63.26", {"position": v(777.62, 340.6) * mm});
            skPoint(sketch, "E5.0.63.27", {"position": v(777.62, 352.39) * mm});
            skPoint(sketch, "E5.0.63.28", {"position": v(777.62, 364.17) * mm});
            skPoint(sketch, "E5.0.63.29", {"position": v(777.62, 375.96) * mm});
            skPoint(sketch, "E5.0.63.30", {"position": v(777.62, 387.74) * mm});
            skPoint(sketch, "E5.0.63.31", {"position": v(777.62, 399.53) * mm});
            skPoint(sketch, "E5.0.63.32", {"position": v(777.62, 411.31) * mm});
            skPoint(sketch, "E5.0.63.33", {"position": v(777.62, 423.1) * mm});
            skPoint(sketch, "E5.0.63.34", {"position": v(777.62, 434.88) * mm});
            skPoint(sketch, "E5.0.63.35", {"position": v(777.62, 446.67) * mm});
            skPoint(sketch, "E5.0.63.36", {"position": v(777.62, 458.45) * mm});
            skPoint(sketch, "E5.0.63.37", {"position": v(777.62, 470.24) * mm});
            skPoint(sketch, "E5.0.63.38", {"position": v(777.62, 482.02) * mm});
            skPoint(sketch, "E5.0.63.39", {"position": v(777.62, 493.8) * mm});
            skPoint(sketch, "E5.0.63.40", {"position": v(777.62, 505.6) * mm});
            skPoint(sketch, "E5.0.63.41", {"position": v(777.62, 517.38) * mm});
            skPoint(sketch, "E5.0.63.42", {"position": v(777.62, 529.16) * mm});
            skPoint(sketch, "E5.0.63.43", {"position": v(777.62, 540.95) * mm});
            skPoint(sketch, "E5.0.63.44", {"position": v(777.62, 552.73) * mm});
            skPoint(sketch, "E5.0.63.45", {"position": v(777.62, 564.52) * mm});
            skPoint(sketch, "E5.0.63.46", {"position": v(777.62, 576.3) * mm});
            skPoint(sketch, "E5.0.63.47", {"position": v(777.62, 588.09) * mm});
            skSolve(sketch);
        }
        {
            var Q0;
            Q0=makeQuery(id+"F0.imprint","IMPRINT",FACE,{"disambiguationData":[TD([[makeQuery(id+"F0.imprint","IMPRINT",EDGE,{"derivedFrom":sQuery(id+"F0.wireOp",EDGE,"E0.bottom")}),1.0]])]});
            extrude(context, id + "F1", {"entities" : qUnion([Q0]), "depth" : 127 * mm});
        }
    });
